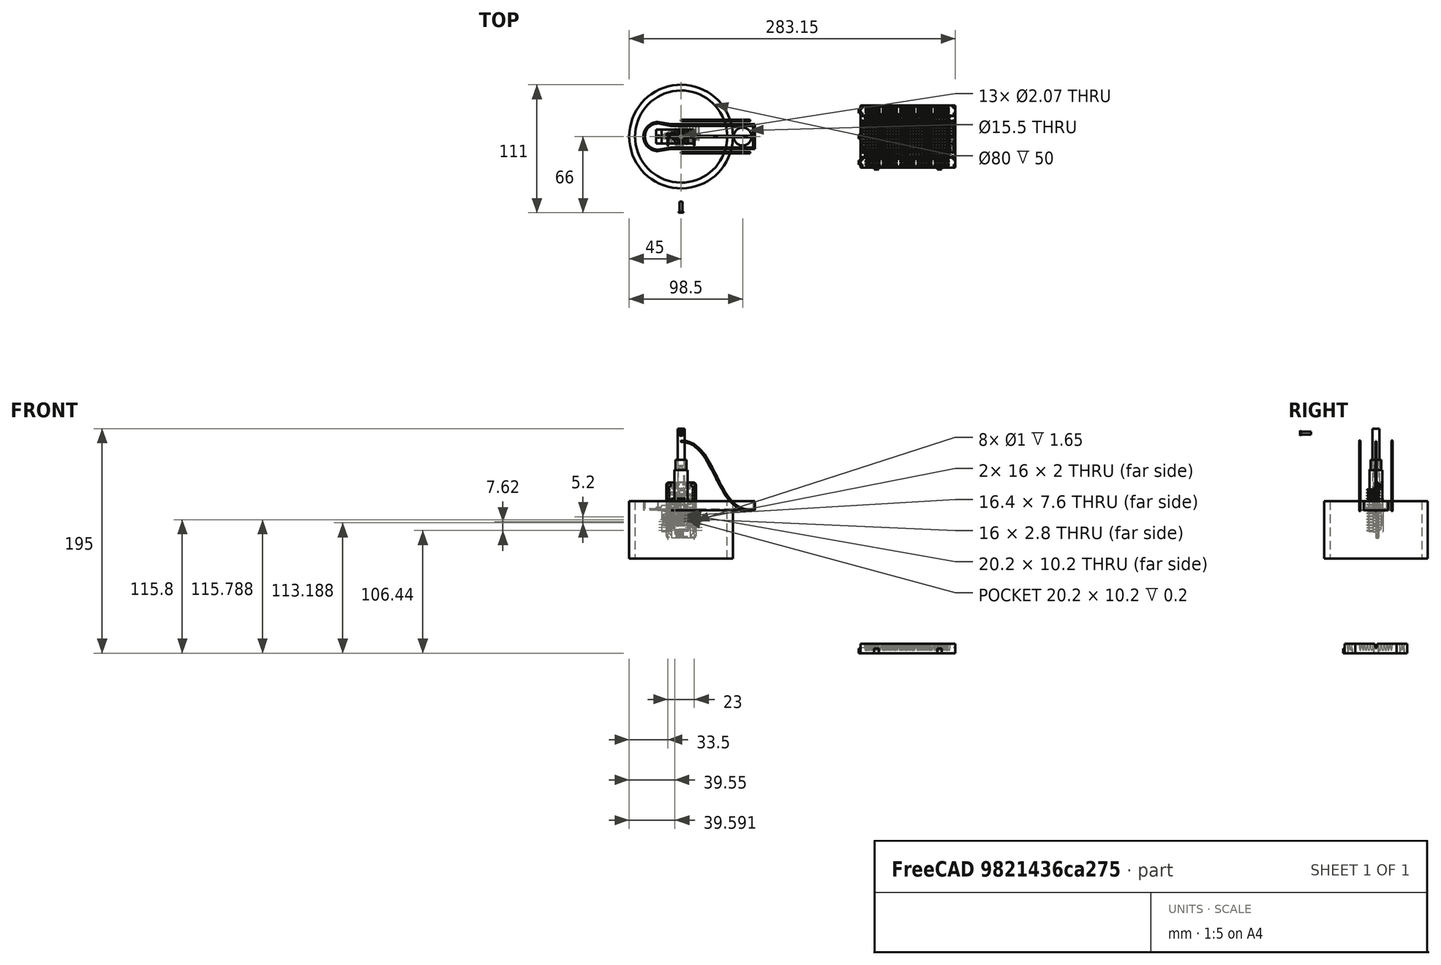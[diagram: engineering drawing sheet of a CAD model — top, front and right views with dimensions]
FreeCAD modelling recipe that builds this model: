
FCSTD DOCUMENT  (FreeCAD 1.0R38641 +678 (Git))
Label: Gems Sorter
License: All rights reserved
LicenseURL: https://en.wikipedia.org/wiki/All_rights_reserved
objects: Part::Feature×123, App::FeaturePython×105, App::Link×104, Sketcher::SketchObject×32, PartDesign::Body×15, PartDesign::Pocket×14, PartDesign::Pad×12, PartDesign::Plane×10, Part::Part2DObjectPython×8, App::Part×5, App::DocumentObjectGroup×5, PartDesign::PolarPattern×3, PartDesign::AdditivePipe×3, Part::FeaturePython×2, App::VarSet×1, PartDesign::Line×1, PartDesign::Thickness×1, PartDesign::Fillet×1, Assembly::JointGroup×1, Assembly::AssemblyObject×1
note: 322 computed .brp shape members not serialized (recipe doc carries the construction recipe); baked Part::Feature solids carry a one-line shape summary decoded from their .brp
EXTERNAL_REF file=Pipe.FCStd obj=Body
EXTERNAL_REF file=Slide Mount.FCStd obj=Cut
EXTERNAL_REF file=Parametric Screw Top Container.FCStd obj=Body001
EXTERNAL_REF file=Parametric Screw Top Container.FCStd obj=Body
EXTERNAL_REF file=testube.FCStd obj=Body
EXTERNAL_REF file=Slide.FCStd obj=Body

FEATURE [App::VarSet] VarSet
  Pipe_thickness = 5
  dowel_dia = 6.2
  fillet_radius = 1.5
  gem_hole_dia = 15.5
  gem_hole_offset = 20
  mdf_thick = 17.5
  mdf_thickness = 7.5
  pipe_OD = 90
  rotation_tolerence = 2.5
  servo_leg_height = 24
  servo_length = 23
  servo_width = 12.3
  shaft_width = 9
  test_tube_dia = 17
  tube_inner_dia = 84.9
FEATURE [Sketcher::SketchObject] Sketch001
  ArcFitTolerance = 1e-06
  AttachmentSupport = -> [XY_Plane001]
  FullyConstrained = true
  MakeInternals = false
  MapMode = 5
  expr: Constraints[2] = VarSet.pipe_OD
  expr: Constraints[3] = VarSet.Pipe_thickness
  sketch-geometry (2):
    g0: Circle CenterX=0 CenterY=0 CenterZ=0 NormalX=0 NormalY=0 NormalZ=1 AngleXU=0 Radius=45
    g1: Circle CenterX=0 CenterY=0 CenterZ=0 NormalX=0 NormalY=0 NormalZ=1 AngleXU=0 Radius=40
  constraints (4):
    c: Coincident(g0,g-1)
    c: Coincident(g1,g0)
    c: Diameter(g0) = 90
    c: Distance(g1,g0) = 5
FEATURE [PartDesign::Pad] Pad001
  Direction = (0,0,1)
  Length = 50
  Length2 = 10
  Profile = -> Sketch001
  ReferenceAxis = -> Sketch001 [N_Axis]
  Refine = true
  Suppressed = false
  Type = 0
FEATURE [PartDesign::Body] Body001  label="Pipe"
  AllowCompound = false
  Group = -> [Sketch001,Pad001]
  Origin = -> Origin001
  Placement = pos=(0,0,-42) rot=(0,0,1;0rad)
  Tip = -> Pad001
FEATURE [Sketcher::SketchObject] Sketch004
  ArcFitTolerance = 1e-06
  AttachmentSupport = -> [XY_Plane002]
  FullyConstrained = true
  MakeInternals = false
  MapMode = 5
  expr: Constraints[0] = VarSet.tube_inner_dia - VarSet.rotation_tolerence
  expr: Constraints[2] = VarSet.gem_hole_offset
  expr: Constraints[3] = VarSet.gem_hole_dia
  sketch-geometry (2):
    g0: Circle CenterX=0 CenterY=0 CenterZ=0 NormalX=0 NormalY=0 NormalZ=1 AngleXU=0 Radius=41.2
    g1: Circle CenterX=0 CenterY=-20 CenterZ=0 NormalX=0 NormalY=0 NormalZ=1 AngleXU=0 Radius=7.75
  constraints (5):
    c: Diameter(g0) = 82.4
    c: PointOnObject(g1,g-2)
    c: Distance(g1,g-1) = 20
    c: Diameter(g1) = 15.5
    c: Coincident(g-1,g0)
FEATURE [PartDesign::Pad] Pad002
  Direction = (0,0,1)
  Length = 7.5
  Length2 = 10
  Profile = -> Sketch004
  ReferenceAxis = -> Sketch004 [N_Axis]
  Refine = true
  Suppressed = false
  Type = 0
  expr: Length = VarSet.mdf_thickness
FEATURE [Sketcher::SketchObject] Sketch006
  ArcFitTolerance = 1e-06
  AttachmentSupport = -> [XY_Plane004]
  FullyConstrained = true
  MakeInternals = false
  MapMode = 5
  expr: Constraints[21] = VarSet.fillet_radius
  expr: Constraints[29] = VarSet.shaft_width
  expr: Constraints[2] = VarSet.gem_hole_dia - 1 mm
  expr: Constraints[3] = VarSet.gem_hole_offset
  expr: Constraints[4] = VarSet.tube_inner_dia - VarSet.rotation_tolerence
  sketch-geometry (13):
    g0: Circle CenterX=0 CenterY=0 CenterZ=0 NormalX=0 NormalY=0 NormalZ=1 AngleXU=0 Radius=41.2
    g1: Circle CenterX=0 CenterY=-20 CenterZ=0 NormalX=0 NormalY=0 NormalZ=1 AngleXU=0 Radius=7.25
    g2: GeomPoint [constr] X=0 Y=0 Z=0
    g3: LineSegment StartX=-7.42462 StartY=-1.06066 StartZ=0 EndX=-1.06066 EndY=-7.42462 EndZ=0
    g4: LineSegment StartX=1.06066 StartY=-7.42462 StartZ=0 EndX=7.42462 EndY=-1.06066 EndZ=0
    g5: LineSegment StartX=7.42462 StartY=1.06066 StartZ=0 EndX=1.06066 EndY=7.42462 EndZ=0
    g6: LineSegment StartX=-1.06066 StartY=7.42462 StartZ=0 EndX=-7.42462 EndY=1.06066 EndZ=0
    g7: ArcOfCircle CenterX=-6.36396 CenterY=0 CenterZ=0 NormalX=0 NormalY=0 NormalZ=1 AngleXU=0 Radius=1.5 StartAngle=2.35619 EndAngle=3.92699
    g8: ArcOfCircle CenterX=0 CenterY=-6.36396 CenterZ=0 NormalX=0 NormalY=0 NormalZ=1 AngleXU=0 Radius=1.5 StartAngle=3.92699 EndAngle=5.49779
    g9: ArcOfCircle CenterX=6.36396 CenterY=1.5e-15 CenterZ=0 NormalX=0 NormalY=0 NormalZ=1 AngleXU=0 Radius=1.5 StartAngle=5.49779 EndAngle=7.06858
    g10: ArcOfCircle CenterX=0 CenterY=6.36396 CenterZ=0 NormalX=0 NormalY=0 NormalZ=1 AngleXU=0 Radius=1.5 StartAngle=0.785398 EndAngle=2.35619
    g11: GeomPoint [constr] X=-8.48528 Y=-5e-16 Z=0
    g12: GeomPoint [constr] X=8.48528 Y=1.3e-15 Z=0
  constraints (30):
    c: Coincident(g0,g-1)
    c: PointOnObject(g1,g-2)
    c: Diameter(g1) = 14.5
    c: Distance(g1,g-1) = 20
    c: Diameter(g0) = 82.4
    c: Coincident(g2,g0)
    c: Tangent(g3,g7) = -1.5708
    c: Tangent(g3,g8) = -1.5708
    c: Tangent(g4,g8) = -1.5708
    c: Tangent(g4,g9) = -1.5708
    c: Tangent(g5,g9) = -1.5708
    c: Tangent(g5,g10) = -1.5708
    c: Tangent(g6,g10) = -1.5708
    c: Tangent(g6,g7) = -1.5708
    c: Equal(g7,g8)
    c: Equal(g8,g9)
    c: Equal(g9,g10)
    c: PointOnObject(g11,g3)
    c: PointOnObject(g11,g6)
    c: PointOnObject(g12,g4)
    c: PointOnObject(g12,g5)
    c: Radius(g8) = 1.5
    c: Equal(g6,g3)
    c: PointOnObject(g10,g-2)
    c: PointOnObject(g8,g-2)
    c: Parallel(g6,g4)
    c: Parallel(g3,g5)
    c: Perpendicular(g5,g6)
    c: PointOnObject(g7,g-1)
    c: Distance(g6,g6) = 9
FEATURE [PartDesign::Pad] Pad004
  Direction = (0,0,1)
  Length = 7.5
  Length2 = 10
  Profile = -> Sketch006
  ReferenceAxis = -> Sketch006 [N_Axis]
  Refine = true
  Suppressed = false
  Type = 0
  expr: Length = VarSet.mdf_thickness
FEATURE [Sketcher::SketchObject] Sketch
  ArcFitTolerance = 1e-06
  AttachmentSupport = -> [XY_Plane]
  FullyConstrained = true
  MakeInternals = false
  MapMode = 5
  expr: Constraints[1] = VarSet.tube_inner_dia
  expr: Constraints[3] = VarSet.dowel_dia + 5 mm
  sketch-geometry (2):
    g0: Circle CenterX=0 CenterY=0 CenterZ=0 NormalX=0 NormalY=0 NormalZ=1 AngleXU=0 Radius=42.45
    g1: Circle CenterX=0 CenterY=0 CenterZ=0 NormalX=0 NormalY=0 NormalZ=1 AngleXU=0 Radius=31.25
  constraints (4):
    c: Coincident(g0,g-1)
    c: Diameter(g0) = 84.9
    c: Coincident(g1,g0)
    c: Distance(g1,g0) = 11.2
FEATURE [PartDesign::Pad] Pad
  Direction = (0,0,1)
  Length = 7.5
  Length2 = 10
  Profile = -> Sketch
  ReferenceAxis = -> Sketch [N_Axis]
  Refine = true
  Suppressed = false
  Type = 0
  expr: Length = VarSet.mdf_thickness
FEATURE [Sketcher::SketchObject] Sketch007
  ArcFitTolerance = 1e-06
  AttachmentSupport = -> [XY_Plane005]
  FullyConstrained = true
  MakeInternals = false
  MapMode = 5
  expr: Constraints[10] = VarSet.gem_hole_offset
  expr: Constraints[5] = VarSet.gem_hole_dia / 2
  expr: Constraints[8] = VarSet.tube_inner_dia / 2
  sketch-geometry (5):
    g0: LineSegment StartX=-33.0518 StartY=-26.638 StartZ=0 EndX=-4 EndY=-26.638 EndZ=0
    g1: LineSegment StartX=33.0518 StartY=-26.638 StartZ=0 EndX=4 EndY=-26.638 EndZ=0
    g2: ArcOfCircle CenterX=1.9e-15 CenterY=-20 CenterZ=0 NormalX=0 NormalY=0 NormalZ=1 AngleXU=0 Radius=7.75 StartAngle=5.25471 EndAngle=10.4532
    g3: ArcOfCircle CenterX=0 CenterY=0 CenterZ=0 NormalX=0 NormalY=0 NormalZ=1 AngleXU=0 Radius=42.45 StartAngle=5.60483 EndAngle=10.1031
    g4: Circle CenterX=0 CenterY=0 CenterZ=0 NormalX=0 NormalY=0 NormalZ=1 AngleXU=0 Radius=9
  constraints (14):
    c: Horizontal(g0)
    c: Horizontal(g1)
    c: Symmetric(g0,g1,g-2)
    c: Coincident(g2,g0)
    c: Coincident(g2,g1)
    c: Radius(g2) = 7.75
    c: Coincident(g3,g-1)
    c: Coincident(g3,g1)
    c: Radius(g3) = 42.45
    c: Coincident(g0,g3)
    c: Distance(g2,g-1) = 20
    c: DistanceX(g0,g1) = 8
    c: Coincident(g4,g3)
    c: Diameter(g4) = 18
FEATURE [PartDesign::Pad] Pad005
  Direction = (0,0,1)
  Length = 17.5
  Length2 = 10
  Profile = -> Sketch007
  ReferenceAxis = -> Sketch007 [N_Axis]
  Refine = true
  Suppressed = false
  Type = 0
  expr: Length = VarSet.mdf_thick
FEATURE [Sketcher::SketchObject] Sketch008
  ArcFitTolerance = 1e-06
  AttachmentSupport = -> [XY_Plane006]
  FullyConstrained = false
  MakeInternals = false
  MapMode = 5
  expr: Constraints[15] = VarSet.gem_hole_offset
  expr: Constraints[16] = VarSet.gem_hole_offset + VarSet.pipe_OD / 2 + VarSet.test_tube_dia + 5 mm
  expr: Constraints[3] = VarSet.tube_inner_dia / 2
  sketch-geometry (6):
    g0: ArcOfCircle CenterX=0 CenterY=0 CenterZ=0 NormalX=0 NormalY=0 NormalZ=1 AngleXU=0 Radius=42.45 StartAngle=1.5708 EndAngle=4.71239
    g1: LineSegment [constr] StartX=2.6e-15 StartY=42.45 StartZ=0 EndX=0 EndY=85.6971 EndZ=0
    g2: LineSegment [constr] StartX=0 StartY=-42.45 StartZ=0 EndX=0 EndY=-85.6971 EndZ=0
    g3: LineSegment StartX=2.6e-15 StartY=42.45 StartZ=0 EndX=27.4414 EndY=72.9268 EndZ=0
    g4: LineSegment StartX=0 StartY=-42.45 StartZ=0 EndX=27.4414 EndY=-72.9268 EndZ=0
    g5: ArcOfCircle CenterX=-20 CenterY=0 CenterZ=0 NormalX=0 NormalY=0 NormalZ=1 AngleXU=0 Radius=87 StartAngle=5.28914 EndAngle=7.27723
  constraints (17):
    c: Coincident(g0,g-1)
    c: PointOnObject(g0,g-2)
    c: PointOnObject(g0,g-2)
    c: Radius(g0) = 42.45
    c: PointOnObject(g1,g-2)
    c: PointOnObject(g2,g-2)
    c: Coincident(g1,g0)
    c: Coincident(g2,g0)
    c: Coincident(g3,g0)
    c: Angle(g3,g1) = 0.733038
    c: Coincident(g4,g0)
    c: Angle(g2,g4) = 0.733038
    c: PointOnObject(g5,g-1)
    c: Coincident(g5,g3)
    c: Coincident(g5,g4)
    c: Distance(g5,g-2) = 20
    c: Radius(g5) = 87
FEATURE [PartDesign::Pad] Pad006
  Direction = (0,0,1)
  Length = 7.5
  Length2 = 10
  Profile = -> Sketch008
  ReferenceAxis = -> Sketch008 [N_Axis]
  Refine = true
  Suppressed = false
  Type = 0
  expr: Length = VarSet.mdf_thickness
FEATURE [PartDesign::Plane] DatumPlane
  AttachmentOffset = pos=(0,0,7.5) rot=(0,0,1;0rad)
  AttachmentSupport = -> [XY_Plane006]
  Length = 134.506
  MapMode = 5
  Placement = pos=(0,0,7.5) rot=(0,0,1;0rad)
  ResizeMode = 0
  Width = 171.101
  expr: .AttachmentOffset.Base.z = VarSet.mdf_thickness
FEATURE [Sketcher::SketchObject] Sketch009
  ArcFitTolerance = 1e-06
  AttachmentSupport = -> [DatumPlane]
  FullyConstrained = true
  MakeInternals = false
  MapMode = 5
  Placement = pos=(0,0,7.5) rot=(0,0,1;0rad)
  expr: Constraints[1] = VarSet.test_tube_dia
  expr: Constraints[2] = VarSet.pipe_OD / 2 + VarSet.test_tube_dia / 2
  sketch-geometry (1):
    g0: Circle CenterX=53.5 CenterY=0 CenterZ=0 NormalX=0 NormalY=0 NormalZ=1 AngleXU=0 Radius=8.5
  constraints (3):
    c: PointOnObject(g0,g-1)
    c: Diameter(g0) = 17
    c: Distance(g0,g-2) = 53.5
FEATURE [PartDesign::Pocket] Pocket
  BaseFeature = -> Pad006
  Direction = (0,0,-1)
  Length = 5
  Length2 = 5
  Profile = -> Sketch009
  ReferenceAxis = -> Sketch009 [N_Axis]
  Refine = true
  Suppressed = false
  Type = 1
FEATURE [PartDesign::Line] DatumLine
  AttacherType = Attacher::AttachEngineLine
  AttachmentOffset = pos=(-20,0,0) rot=(0,0,1;0rad)
  AttachmentSupport = -> [Z_Axis006]
  Length = 20
  MapMode = 29
  Placement = pos=(-20,0,0) rot=(0,0,1;0rad)
  ResizeMode = 0
  expr: .AttachmentOffset.Base.x = -VarSet.gem_hole_offset
FEATURE [PartDesign::PolarPattern] PolarPattern
  Angle = 360
  Axis = -> DatumLine
  BaseFeature = -> Pocket
  Mode = 0
  Occurrences = 22
  Offset = 120
  Originals = -> [Pocket]
  Refine = true
  Suppressed = false
  TransformMode = 0
FEATURE [Sketcher::SketchObject] Sketch010
  ArcFitTolerance = 1e-06
  AttachmentSupport = -> [DatumPlane]
  FullyConstrained = false
  MakeInternals = false
  MapMode = 5
  Placement = pos=(0,0,7.5) rot=(0,0,1;0rad)
  expr: Constraints[1] = VarSet.gem_hole_offset
  expr: Constraints[21] = VarSet.servo_length
  sketch-geometry (9):
    g0: LineSegment [constr] StartX=-20 StartY=14.1317 StartZ=0 EndX=-20 EndY=-18.2085 EndZ=0
    g1: LineSegment StartX=-34 StartY=4.05 StartZ=0 EndX=-34 EndY=-4.05 EndZ=0
    g2: LineSegment StartX=-34 StartY=-4.05 StartZ=0 EndX=-25.9 EndY=-4.05 EndZ=0
    g3: LineSegment StartX=-25.9 StartY=-4.05 StartZ=0 EndX=-25.9 EndY=4.05 EndZ=0
    g4: LineSegment StartX=-25.9 StartY=4.05 StartZ=0 EndX=-34 EndY=4.05 EndZ=0
    g5: LineSegment StartX=-2.9 StartY=4.05 StartZ=0 EndX=-2.9 EndY=-4.05 EndZ=0
    g6: LineSegment StartX=-2.9 StartY=-4.05 StartZ=0 EndX=5.2 EndY=-4.05 EndZ=0
    g7: LineSegment StartX=5.2 StartY=-4.05 StartZ=0 EndX=5.2 EndY=4.05 EndZ=0
    g8: LineSegment StartX=5.2 StartY=4.05 StartZ=0 EndX=-2.9 EndY=4.05 EndZ=0
  constraints (24):
    c: Vertical(g0)
    c: Distance(g-2,g0) = 20
    c: Coincident(g1,g2)
    c: Coincident(g2,g3)
    c: Coincident(g3,g4)
    c: Coincident(g4,g1)
    c: Vertical(g3)
    c: Horizontal(g2)
    c: Horizontal(g4)
    c: Coincident(g5,g6)
    c: Coincident(g6,g7)
    c: Coincident(g7,g8)
    c: Coincident(g8,g5)
    c: Vertical(g7)
    c: Horizontal(g6)
    c: Horizontal(g8)
    c: Equal(g4,g1)
    c: Equal(g1,g8)
    c: Equal(g8,g5)
    c: Symmetric(g1,g1,g-1)
    c: Symmetric(g5,g5,g-1)
    c: Distance(g5,g3) = 23
    c: Distance(g0,g3) = 5.9
    c: DistanceX(g4,g4) = 8.1
FEATURE [PartDesign::Pocket] Pocket001
  BaseFeature = -> PolarPattern
  Direction = (0,0,-1)
  Length = 5
  Length2 = 5
  Profile = -> Sketch010
  ReferenceAxis = -> Sketch010 [N_Axis]
  Refine = true
  Suppressed = false
  Type = 1
FEATURE [PartDesign::Plane] DatumPlane001
  AttachmentOffset = pos=(0,0,7.5) rot=(0,0,1;0rad)
  AttachmentSupport = -> [XY_Plane]
  Length = 101.88
  MapMode = 5
  Placement = pos=(0,0,7.5) rot=(0,0,1;0rad)
  ResizeMode = 0
  Width = 101.88
  expr: .AttachmentOffset.Base.z = VarSet.mdf_thickness
FEATURE [Sketcher::SketchObject] Sketch011
  ArcFitTolerance = 1e-06
  AttachmentSupport = -> [DatumPlane001]
  FullyConstrained = true
  MakeInternals = false
  MapMode = 5
  Placement = pos=(0,0,7.5) rot=(0,0,1;0rad)
  expr: Constraints[17] = VarSet.tube_inner_dia / 2 - 2.5 mm - VarSet.dowel_dia / 2
  expr: Constraints[1] = VarSet.dowel_dia
  expr: Constraints[2] = VarSet.tube_inner_dia / 2 - 2.5 mm - VarSet.dowel_dia / 2
  expr: Constraints[6] = VarSet.tube_inner_dia / 2 - 2.5 mm - VarSet.dowel_dia / 2
  sketch-geometry (8):
    g0: Circle [constr] CenterX=-36.85 CenterY=0 CenterZ=0 NormalX=0 NormalY=0 NormalZ=1 AngleXU=0 Radius=3.1
    g1: Circle CenterX=-31.913 CenterY=18.425 CenterZ=0 NormalX=0 NormalY=0 NormalZ=1 AngleXU=0 Radius=3.1
    g2: Circle CenterX=-31.913 CenterY=-18.425 CenterZ=0 NormalX=0 NormalY=0 NormalZ=1 AngleXU=0 Radius=3.1
    g3: LineSegment [constr] StartX=-31.913 StartY=-18.425 StartZ=0 EndX=0 EndY=0 EndZ=0
    g4: Circle CenterX=-18.425 CenterY=31.913 CenterZ=0 NormalX=0 NormalY=0 NormalZ=1 AngleXU=0 Radius=3.1
    g5: Circle CenterX=-18.425 CenterY=-31.913 CenterZ=0 NormalX=0 NormalY=0 NormalZ=1 AngleXU=0 Radius=3.1
    g6: LineSegment [constr] StartX=-18.425 StartY=31.913 StartZ=0 EndX=0 EndY=-3.6e-15 EndZ=0
    g7: LineSegment [constr] StartX=0 StartY=0 StartZ=0 EndX=-18.425 EndY=-31.913 EndZ=0
  constraints (19):
    c: PointOnObject(g0,g-1)
    c: Diameter(g0) = 6.2
    c: Distance(g0,g-2) = 36.85
    c: Equal(g1,g2)
    c: Equal(g2,g0)
    c: Symmetric(g2,g1,g-1)
    c: Distance(g1,g-1) = 36.85
    c: Coincident(g3,g2)
    c: Coincident(g3,g-1)
    c: Angle(g-1,g3) = 0.523599
    c: Equal(g5,g4)
    c: Equal(g4,g2)
    c: Symmetric(g5,g4,g-1)
    c: Coincident(g6,g4)
    c: Coincident(g6,g3)
    c: Coincident(g7,g3)
    c: Coincident(g7,g5)
    c: Distance(g6,g6) = 36.85
    c: Angle(g6,g-1) = 1.0472
FEATURE [PartDesign::Pocket] Pocket003
  BaseFeature = -> Pad
  Direction = (0,0,-1)
  Length = 5
  Length2 = 5
  Profile = -> Sketch011
  ReferenceAxis = -> Sketch011 [N_Axis]
  Refine = true
  Suppressed = false
  Type = 1
FEATURE [Sketcher::SketchObject] Sketch012
  ArcFitTolerance = 1e-06
  AttachmentSupport = -> [XY_Plane007]
  FullyConstrained = true
  MakeInternals = false
  MapMode = 5
  expr: Constraints[19] = VarSet.mdf_thickness
  expr: Constraints[20] = VarSet.mdf_thickness
  expr: Constraints[21] = VarSet.servo_leg_height
  expr: Constraints[41] = VarSet.fillet_radius
  expr: Constraints[47] = VarSet.mdf_thickness / 2
  sketch-geometry (20):
    g0: LineSegment StartX=0 StartY=0 StartZ=0 EndX=0 EndY=7.5 EndZ=0
    g1: LineSegment StartX=0 StartY=7.5 StartZ=0 EndX=7.5 EndY=7.5 EndZ=0
    g2: LineSegment StartX=7.5 StartY=7.5 StartZ=0 EndX=7.5 EndY=12.0784 EndZ=0
    g3: LineSegment StartX=7.5 StartY=12.0784 StartZ=0 EndX=31.5 EndY=12.0784 EndZ=0
    g4: LineSegment StartX=31.5 StartY=12.0784 StartZ=0 EndX=31.5 EndY=-4.57843 EndZ=0
    g5: LineSegment StartX=31.5 StartY=-4.57843 StartZ=0 EndX=7.5 EndY=-4.57843 EndZ=0
    g6: LineSegment StartX=7.5 StartY=-4.57843 StartZ=0 EndX=7.5 EndY=0 EndZ=0
    g7: LineSegment StartX=7.5 StartY=0 StartZ=0 EndX=0 EndY=0 EndZ=0
    g8: LineSegment StartX=12.5 StartY=6.57843 StartZ=0 EndX=12.5 EndY=0.921573 EndZ=0
    g9: LineSegment StartX=14 StartY=-0.578427 StartZ=0 EndX=19.6569 EndY=-0.578427 EndZ=0
    g10: LineSegment StartX=21.1569 StartY=0.921573 StartZ=0 EndX=21.1569 EndY=6.57843 EndZ=0
    g11: LineSegment StartX=19.6569 StartY=8.07843 StartZ=0 EndX=14 EndY=8.07843 EndZ=0
    g12: ArcOfCircle CenterX=14 CenterY=6.57843 CenterZ=0 NormalX=0 NormalY=0 NormalZ=1 AngleXU=0 Radius=1.5 StartAngle=1.5708 EndAngle=3.14159
    g13: ArcOfCircle CenterX=14 CenterY=0.921573 CenterZ=0 NormalX=0 NormalY=0 NormalZ=1 AngleXU=0 Radius=1.5 StartAngle=3.14159 EndAngle=4.71239
    g14: ArcOfCircle CenterX=19.6569 CenterY=0.921573 CenterZ=0 NormalX=0 NormalY=0 NormalZ=1 AngleXU=0 Radius=1.5 StartAngle=4.71239 EndAngle=6.28319
    g15: ArcOfCircle CenterX=19.6569 CenterY=6.57843 CenterZ=0 NormalX=0 NormalY=0 NormalZ=1 AngleXU=0 Radius=1.5 StartAngle=0 EndAngle=1.5708
    g16: GeomPoint [constr] X=12.5 Y=8.07843 Z=0
    g17: GeomPoint [constr] X=21.1569 Y=-0.578427 Z=0
    g18: LineSegment [constr] StartX=14 StartY=6.57843 StartZ=0 EndX=19.6569 EndY=0.921573 EndZ=0
    g19: LineSegment [constr] StartX=14 StartY=0.921573 StartZ=0 EndX=16.8284 EndY=3.75 EndZ=0
  constraints (51):
    c: Coincident(g0,g-1)
    c: PointOnObject(g0,g-2)
    c: Coincident(g0,g1)
    c: Horizontal(g1)
    c: Coincident(g1,g2)
    c: Vertical(g2)
    c: Coincident(g2,g3)
    c: Coincident(g3,g4)
    c: Vertical(g4)
    c: Coincident(g4,g5)
    c: Horizontal(g5)
    c: Coincident(g5,g6)
    c: PointOnObject(g6,g-1)
    c: Vertical(g6)
    c: Coincident(g6,g7)
    c: Coincident(g7,g0)
    c: Equal(g1,g7)
    c: Equal(g3,g5)
    c: Equal(g2,g6)
    c: DistanceX(g1,g1) = 7.5
    c: Distance(g0,g0) = 7.5
    c: DistanceX(g5,g5) = 24
    c: Tangent(g8,g12) = -1.5708
    c: Tangent(g8,g13) = -1.5708
    c: Tangent(g9,g13) = -1.5708
    c: Tangent(g9,g14) = -1.5708
    c: Tangent(g10,g14) = -1.5708
    c: Tangent(g10,g15) = -1.5708
    c: Tangent(g11,g15) = -1.5708
    c: Tangent(g11,g12) = -1.5708
    c: Vertical(g8)
    c: Vertical(g10)
    c: Horizontal(g9)
    c: Horizontal(g11)
    c: Equal(g12,g13)
    c: Equal(g13,g14)
    c: Equal(g14,g15)
    c: PointOnObject(g16,g8)
    c: PointOnObject(g16,g11)
    c: PointOnObject(g17,g9)
    c: PointOnObject(g17,g10)
    c: Radius(g13) = 1.5
    c: Coincident(g18,g12)
    c: Coincident(g18,g14)
    c: Coincident(g19,g13)
    c: Symmetric(g18,g18,g19)
    c: Equal(g11,g8)
    c: Distance(g19,g-1) = 3.75
    c: Distance(g18,g18) = 8
    c: Distance(g2,g8) = 5
    c: Distance(g5,g9) = 4
FEATURE [PartDesign::Pad] Pad007
  Direction = (0,0,1)
  Length = 7.5
  Length2 = 10
  Profile = -> Sketch012
  ReferenceAxis = -> Sketch012 [N_Axis]
  Refine = true
  Suppressed = false
  Type = 0
  expr: Length = VarSet.mdf_thickness
FEATURE [Sketcher::SketchObject] Sketch013
  ArcFitTolerance = 1e-06
  AttachmentSupport = -> [DatumPlane]
  FullyConstrained = true
  MakeInternals = false
  MapMode = 5
  Placement = pos=(0,0,7.5) rot=(0,0,1;0rad)
  expr: Constraints[5] = VarSet.tube_inner_dia / 2 - 2.5 mm - VarSet.dowel_dia / 2
  expr: Constraints[6] = VarSet.tube_inner_dia / 2 - 2.5 mm - VarSet.dowel_dia / 2
  expr: Constraints[7] = VarSet.dowel_dia
  sketch-geometry (6):
    g0: Circle CenterX=-31.913 CenterY=18.425 CenterZ=0 NormalX=0 NormalY=0 NormalZ=1 AngleXU=0 Radius=3.1
    g1: Circle CenterX=-18.425 CenterY=31.913 CenterZ=0 NormalX=0 NormalY=0 NormalZ=1 AngleXU=0 Radius=3.1
    g2: Circle CenterX=-31.913 CenterY=-18.425 CenterZ=0 NormalX=0 NormalY=0 NormalZ=1 AngleXU=0 Radius=3.1
    g3: Circle CenterX=-18.425 CenterY=-31.913 CenterZ=0 NormalX=0 NormalY=0 NormalZ=1 AngleXU=0 Radius=3.1
    g4: LineSegment [constr] StartX=-31.913 StartY=18.425 StartZ=0 EndX=0 EndY=0 EndZ=0
    g5: LineSegment [constr] StartX=-18.425 StartY=31.913 StartZ=0 EndX=0 EndY=0 EndZ=0
  constraints (14):
    c: Equal(g3,g2)
    c: Equal(g2,g0)
    c: Equal(g0,g1)
    c: Symmetric(g0,g2,g-1)
    c: Symmetric(g1,g3,g-1)
    c: Distance(g2,g-1) = 36.85
    c: Distance(g3,g-1) = 36.85
    c: Diameter(g3) = 6.2
    c: Coincident(g4,g0)
    c: Coincident(g4,g-1)
    c: Coincident(g5,g1)
    c: Coincident(g5,g4)
    c: Angle(g4,g-1) = 0.523599
    c: Angle(g5,g-1) = 1.0472
FEATURE [PartDesign::Pocket] Pocket004
  BaseFeature = -> Pocket001
  Direction = (0,0,-1)
  Length = 5
  Length2 = 5
  Profile = -> Sketch013
  ReferenceAxis = -> Sketch013 [N_Axis]
  Refine = true
  Suppressed = false
  Type = 1
FEATURE [PartDesign::Body] Body006  label="testube_layer"
  AllowCompound = false
  Group = -> [Sketch008,Pad006,DatumPlane,Sketch009,Pocket,DatumLine,PolarPattern,Sketch010,Pocket001,Sketch013,Pocket004]
  Origin = -> Origin006
  Placement = pos=(0,0,-39) rot=(0,0,1;0rad)
  Tip = -> Pocket004
FEATURE [Sketcher::SketchObject] Sketch014
  ArcFitTolerance = 1e-06
  AttachmentSupport = -> [XY_Plane008]
  FullyConstrained = true
  MakeInternals = false
  MapMode = 5
  expr: Constraints[1] = VarSet.dowel_dia - 0.05 mm
  sketch-geometry (1):
    g0: Circle CenterX=0 CenterY=0 CenterZ=0 NormalX=0 NormalY=0 NormalZ=1 AngleXU=0 Radius=3.075
  constraints (2):
    c: Coincident(g0,g-1)
    c: Diameter(g0) = 6.15
FEATURE [PartDesign::Pad] Pad008
  Direction = (0,0,1)
  Length = 71
  Length2 = 10
  Profile = -> Sketch014
  ReferenceAxis = -> Sketch014 [N_Axis]
  Refine = true
  Suppressed = false
  Type = 0
FEATURE [PartDesign::Body] Body008  label="dowel"
  AllowCompound = false
  Group = -> [Sketch014,Pad008]
  Origin = -> Origin008
  Tip = -> Pad008
FEATURE [Sketcher::SketchObject] Sketch015
  ArcFitTolerance = 1e-06
  AttachmentSupport = -> [Pad007]
  ExternalGeometry = -> [Pad007]
  FullyConstrained = false
  MakeInternals = false
  MapMode = 5
  Placement = pos=(31.5,0,0) rot=(0.57735,0.57735,0.57735;2.0944rad)
  sketch-geometry (1):
    g0: Circle CenterX=3.87266 CenterY=2.4 CenterZ=0 NormalX=0 NormalY=0 NormalZ=1 AngleXU=0 Radius=0.75
  constraints (2):
    c: Distance(g0,g-3) = 2.4
    c: Diameter(g0) = 1.5
FEATURE [PartDesign::Pocket] Pocket005
  BaseFeature = -> Pad007
  Direction = (-1,0,0)
  Length = 5
  Length2 = 5
  Profile = -> Sketch015
  ReferenceAxis = -> Sketch015 [N_Axis]
  Refine = true
  Suppressed = false
  Type = 0
FEATURE [PartDesign::Body] Body007  label="sevo_legs"
  AllowCompound = false
  Group = -> [Sketch012,Pad007,Sketch015,Pocket005]
  Origin = -> Origin007
  Placement = pos=(-26,-3,23) rot=(0,1,0;4.71239rad)
  Tip = -> Pocket005
FEATURE [Sketcher::SketchObject] Sketch016
  ArcFitTolerance = 1e-06
  AttachmentSupport = -> [XY_Plane009]
  FullyConstrained = true
  MakeInternals = false
  MapMode = 5
  expr: Constraints[16] = VarSet.gem_hole_dia / 2 + 5 mm
  expr: Constraints[2] = VarSet.gem_hole_dia + 6 mm
  expr: Constraints[5] = VarSet.pipe_OD / 2 + VarSet.test_tube_dia + 2 mm
  expr: Constraints[8] = VarSet.gem_hole_offset
  sketch-geometry (8):
    g0: LineSegment StartX=-8.65743 StartY=10.75 StartZ=0 EndX=64 EndY=10.75 EndZ=0
    g1: LineSegment StartX=64 StartY=10.75 StartZ=0 EndX=64 EndY=-10.75 EndZ=0
    g2: LineSegment StartX=64 StartY=-10.75 StartZ=0 EndX=-8.65743 EndY=-10.75 EndZ=0
    g3: ArcOfCircle CenterX=-20 CenterY=0 CenterZ=0 NormalX=0 NormalY=0 NormalZ=1 AngleXU=0 Radius=12.75 StartAngle=1.5708 EndAngle=4.71239
    g4: LineSegment [constr] StartX=-20 StartY=-12.75 StartZ=0 EndX=-20 EndY=12.75 EndZ=0
    g5: LineSegment StartX=-20 StartY=12.75 StartZ=0 EndX=-8.65743 EndY=10.75 EndZ=0
    g6: LineSegment StartX=-20 StartY=-12.75 StartZ=0 EndX=-8.65743 EndY=-10.75 EndZ=0
    g7: LineSegment [constr] StartX=-8.65743 StartY=10.75 StartZ=0 EndX=-20 EndY=10.75 EndZ=0
  constraints (22):
    c: Coincident(g2,g1)
    c: Coincident(g0,g1)
    c: DistanceY(g1,g1) = 21.5
    c: Symmetric(g0,g1,g-1)
    c: Symmetric(g0,g2,g-1)
    c: Distance(g-2,g1) = 64
    c: Angle(g3) = 3.14159
    c: PointOnObject(g3,g-1)
    c: Distance(g3,g-2) = 20
    c: Coincident(g4,g3)
    c: Coincident(g4,g3)
    c: Vertical(g4)
    c: Coincident(g5,g3)
    c: Coincident(g5,g0)
    c: Coincident(g6,g3)
    c: Coincident(g6,g2)
    c: Radius(g3) = 12.75
    c: Coincident(g7,g0)
    c: PointOnObject(g7,g4)
    c: Horizontal(g7)
    c: Angle(g5,g7) = 0.174533
    c: Horizontal(g0)
FEATURE [PartDesign::Pad] Pad009
  Direction = (0,0,1)
  Length = 8
  Length2 = 10
  Profile = -> Sketch016
  ReferenceAxis = -> Sketch016 [N_Axis]
  Refine = true
  Suppressed = false
  Type = 0
FEATURE [PartDesign::Thickness] Thickness
  Base = -> Pad009 [Face8]
  BaseFeature = -> Pad009
  Intersection = false
  Join = 0
  Mode = 0
  Refine = true
  Reversed = true
  SupportTransform = false
  Suppressed = false
  Value = 1.4
FEATURE [Sketcher::SketchObject] Sketch017
  ArcFitTolerance = 1e-06
  AttachmentSupport = -> [Thickness]
  FullyConstrained = true
  MakeInternals = false
  MapMode = 5
  Placement = pos=(0,0,1.4) rot=(0,0,1;0rad)
  expr: Constraints[1] = VarSet.gem_hole_dia
  expr: Constraints[2] = VarSet.pipe_OD / 2 + VarSet.test_tube_dia / 2
  sketch-geometry (1):
    g0: Circle CenterX=53.5 CenterY=0 CenterZ=0 NormalX=0 NormalY=0 NormalZ=1 AngleXU=0 Radius=7.75
  constraints (3):
    c: PointOnObject(g0,g-1)
    c: Diameter(g0) = 15.5
    c: Distance(g0,g-2) = 53.5
FEATURE [PartDesign::Pocket] Pocket006
  BaseFeature = -> Thickness
  Direction = (0,0,-1)
  Length = 5
  Length2 = 5
  Profile = -> Sketch017
  ReferenceAxis = -> Sketch017 [N_Axis]
  Refine = true
  Suppressed = false
  Type = 1
FEATURE [PartDesign::Body] Body009  label="slide"
  AllowCompound = false
  Group = -> [Sketch016,Pad009,Thickness,Sketch017,Pocket006]
  Origin = -> Origin009
  Tip = -> Pocket006
FEATURE [PartDesign::Fillet] Fillet
  Base = -> Pad005 [Edge5,Edge8,Edge2,Edge1]
  BaseFeature = -> Pad005
  Radius = 1.5
  Refine = true
  SupportTransform = false
  Suppressed = false
  UseAllEdges = false
  expr: Radius = VarSet.fillet_radius
FEATURE [Part::Feature] Part__Feature002  label="shaft"
  shape: bbox 11.25 x 11.25 x 44 mm, 27 faces (baked)
FEATURE [Sketcher::SketchObject] Sketch018
  ArcFitTolerance = 1e-06
  AttachmentSupport = -> [Pad002]
  ExternalGeometry = -> [Pad002]
  FullyConstrained = true
  MakeInternals = false
  MapMode = 5
  Placement = pos=(0,0,7.5) rot=(0,0,1;0rad)
  sketch-geometry (4):
    g0: LineSegment StartX=-1.5 StartY=-33.1727 StartZ=0 EndX=-1.5 EndY=-41.1727 EndZ=0
    g1: LineSegment StartX=1.5 StartY=-41.1727 StartZ=0 EndX=1.5 EndY=-33.1727 EndZ=0
    g2: LineSegment StartX=1.5 StartY=-33.1727 StartZ=0 EndX=-1.5 EndY=-33.1727 EndZ=0
    g3: ArcOfCircle CenterX=0 CenterY=0 CenterZ=0 NormalX=0 NormalY=0 NormalZ=1 AngleXU=0 Radius=41.2 StartAngle=4.67597 EndAngle=4.7488
  constraints (11):
    c: Coincident(g1,g2)
    c: Coincident(g2,g0)
    c: Vertical(g0)
    c: Vertical(g1)
    c: Coincident(g3,g-1)
    c: Coincident(g3,g0)
    c: Coincident(g3,g1)
    c: PointOnObject(g0,g-3)
    c: Symmetric(g0,g1,g-2)
    c: Distance(g2,g2) = 3
    c: DistanceY(g1,g1) = 8
FEATURE [PartDesign::Pocket] Pocket007
  BaseFeature = -> Pad002
  Direction = (0,0,-1)
  Length = 2
  Length2 = 5
  Profile = -> Sketch018
  ReferenceAxis = -> Sketch018 [N_Axis]
  Refine = true
  Suppressed = false
  Type = 0
FEATURE [Sketcher::SketchObject] Sketch019
  ArcFitTolerance = 1e-06
  AttachmentSupport = -> [Pocket007]
  FullyConstrained = true
  MakeInternals = false
  MapMode = 5
  Placement = pos=(0,0,7.5) rot=(0,0,1;0rad)
  sketch-geometry (12):
    g0: LineSegment StartX=-6 StartY=4.5 StartZ=0 EndX=-6 EndY=-4.5 EndZ=0
    g1: LineSegment StartX=-4.5 StartY=-6 StartZ=0 EndX=4.5 EndY=-6 EndZ=0
    g2: LineSegment StartX=6 StartY=-4.5 StartZ=0 EndX=6 EndY=4.5 EndZ=0
    g3: LineSegment StartX=4.5 StartY=6 StartZ=0 EndX=-4.5 EndY=6 EndZ=0
    g4: ArcOfCircle CenterX=-4.5 CenterY=4.5 CenterZ=0 NormalX=0 NormalY=0 NormalZ=1 AngleXU=0 Radius=1.5 StartAngle=1.5708 EndAngle=3.14159
    g5: ArcOfCircle CenterX=-4.5 CenterY=-4.5 CenterZ=0 NormalX=0 NormalY=0 NormalZ=1 AngleXU=0 Radius=1.5 StartAngle=3.14159 EndAngle=4.71239
    g6: ArcOfCircle CenterX=4.5 CenterY=-4.5 CenterZ=0 NormalX=0 NormalY=0 NormalZ=1 AngleXU=0 Radius=1.5 StartAngle=4.71239 EndAngle=6.28319
    g7: ArcOfCircle CenterX=4.5 CenterY=4.5 CenterZ=0 NormalX=0 NormalY=0 NormalZ=1 AngleXU=0 Radius=1.5 StartAngle=0 EndAngle=1.5708
    g8: GeomPoint [constr] X=-6 Y=6 Z=0
    g9: GeomPoint [constr] X=6 Y=-6 Z=0
    g10: LineSegment [constr] StartX=-4.5 StartY=4.5 StartZ=0 EndX=4.5 EndY=-4.5 EndZ=0
    g11: LineSegment [constr] StartX=4.5 StartY=4.5 StartZ=0 EndX=0 EndY=0 EndZ=0
  constraints (27):
    c: Tangent(g0,g4) = -1.5708
    c: Tangent(g0,g5) = -1.5708
    c: Tangent(g1,g5) = -1.5708
    c: Tangent(g1,g6) = -1.5708
    c: Tangent(g2,g6) = -1.5708
    c: Tangent(g2,g7) = -1.5708
    c: Tangent(g3,g7) = -1.5708
    c: Tangent(g3,g4) = -1.5708
    c: Vertical(g0)
    c: Vertical(g2)
    c: Horizontal(g1)
    c: Horizontal(g3)
    c: Equal(g4,g5)
    c: Equal(g5,g6)
    c: Equal(g6,g7)
    c: PointOnObject(g8,g0)
    c: PointOnObject(g8,g3)
    c: PointOnObject(g9,g1)
    c: PointOnObject(g9,g2)
    c: Radius(g4) = 1.5
    c: Distance(g3,g3) = 9
    c: Equal(g3,g2)
    c: Coincident(g10,g4)
    c: Coincident(g10,g6)
    c: Coincident(g11,g7)
    c: Symmetric(g10,g10,g11)
    c: Coincident(g11,g-1)
FEATURE [PartDesign::Pocket] Pocket008
  BaseFeature = -> Pocket007
  Direction = (0,0,-1)
  Length = 4
  Length2 = 5
  Profile = -> Sketch019
  ReferenceAxis = -> Sketch019 [N_Axis]
  Refine = true
  Suppressed = false
  Type = 0
FEATURE [PartDesign::Body] Body002  label="second_layer"
  AllowCompound = false
  Group = -> [Sketch004,Pad002,Sketch018,Pocket007,Sketch019,Pocket008]
  Origin = -> Origin002
  Placement = pos=(0,0,-3) rot=(0,0,1;1.5708rad)
  Tip = -> Pocket008
FEATURE [Sketcher::SketchObject] Sketch020
  ArcFitTolerance = 1e-06
  AttachmentSupport = -> [Pad004]
  ExternalGeometry = -> [Pad004]
  FullyConstrained = true
  MakeInternals = false
  MapMode = 5
  Placement = pos=(0,0,7.5) rot=(0,0,1;0rad)
  sketch-geometry (4):
    g0: LineSegment StartX=22.396 StartY=-24.5173 StartZ=0 EndX=28.0528 EndY=-30.1741 EndZ=0
    g1: LineSegment StartX=24.5173 StartY=-22.396 StartZ=0 EndX=30.1741 EndY=-28.0528 EndZ=0
    g2: LineSegment StartX=24.5173 StartY=-22.396 StartZ=0 EndX=22.396 EndY=-24.5173 EndZ=0
    g3: ArcOfCircle CenterX=0 CenterY=0 CenterZ=0 NormalX=0 NormalY=0 NormalZ=1 AngleXU=0 Radius=41.2 StartAngle=5.46137 EndAngle=5.5342
  constraints (12):
    c: Coincident(g2,g1)
    c: Coincident(g2,g0)
    c: Coincident(g3,g-1)
    c: Coincident(g3,g0)
    c: Parallel(g0,g1)
    c: Equal(g0,g1)
    c: Perpendicular(g0,g2)
    c: PointOnObject(g0,g-3)
    c: Coincident(g1,g3)
    c: Distance(g2,g2) = 3
    c: Distance(g1,g1) = 8
    c: Parallel(g2,g-4)
FEATURE [PartDesign::Pocket] Pocket009
  BaseFeature = -> Pad004
  Direction = (0,0,-1)
  Length = 2
  Length2 = 5
  Profile = -> Sketch020
  ReferenceAxis = -> Sketch020 [N_Axis]
  Refine = true
  Suppressed = false
  Type = 0
FEATURE [PartDesign::Body] Body004  label="first_layer"
  AllowCompound = false
  Group = -> [Sketch006,Pad004,Sketch020,Pocket009]
  Origin = -> Origin004
  Placement = pos=(0,0,23) rot=(0,0,1;0rad)
  Tip = -> Pocket009
FEATURE [Sketcher::SketchObject] Sketch021
  ArcFitTolerance = 1e-06
  AttachmentSupport = -> [XY_Plane012]
  FullyConstrained = true
  MakeInternals = false
  MapMode = 5
  expr: Constraints[1] = VarSet.tube_inner_dia
  expr: Constraints[40] = 12.3 mm + 0.5 mm
  sketch-geometry (18):
    g0: Circle CenterX=0 CenterY=0 CenterZ=0 NormalX=0 NormalY=0 NormalZ=1 AngleXU=0 Radius=42.45
    g1: LineSegment [constr] StartX=0 StartY=0 StartZ=0 EndX=17.475 EndY=30.2676 EndZ=0
    g2: LineSegment [constr] StartX=0 StartY=0 StartZ=0 EndX=17.475 EndY=-30.2676 EndZ=0
    g3: ArcOfCircle CenterX=0 CenterY=0 CenterZ=0 NormalX=0 NormalY=0 NormalZ=1 AngleXU=0 Radius=12.5 StartAngle=5.23599 EndAngle=7.33038
    g4: ArcOfCircle CenterX=0 CenterY=0 CenterZ=0 NormalX=0 NormalY=0 NormalZ=1 AngleXU=0 Radius=34.95 StartAngle=5.23599 EndAngle=7.33038
    g5: LineSegment StartX=6.25 StartY=-10.8253 StartZ=0 EndX=4.07179 EndY=-23.0526 EndZ=0
    g6: LineSegment StartX=17.475 StartY=-30.2676 StartZ=0 EndX=4.07179 EndY=-23.0526 EndZ=0
    g7: LineSegment StartX=17.475 StartY=30.2676 StartZ=0 EndX=4.0718 EndY=23.0526 EndZ=0
    g8: LineSegment StartX=4.0718 StartY=23.0526 StartZ=0 EndX=6.25 EndY=10.8253 EndZ=0
    g9: LineSegment [constr] StartX=11 StartY=-19.0526 StartZ=0 EndX=4.07179 EndY=-23.0526 EndZ=0
    g10: LineSegment [constr] StartX=11 StartY=19.0526 StartZ=0 EndX=4.0718 EndY=23.0526 EndZ=0
    g11: LineSegment StartX=-17.65 StartY=6.4 StartZ=0 EndX=-17.65 EndY=-6.4 EndZ=0
    g12: LineSegment StartX=-17.65 StartY=-6.4 StartZ=0 EndX=5.85 EndY=-6.4 EndZ=0
    g13: LineSegment StartX=5.85 StartY=-6.4 StartZ=0 EndX=5.85 EndY=6.4 EndZ=0
    g14: LineSegment StartX=5.85 StartY=6.4 StartZ=0 EndX=-17.65 EndY=6.4 EndZ=0
    g15: GeomPoint [constr] X=-5.9 Y=0 Z=0
    g16: Circle CenterX=8.25 CenterY=0 CenterZ=0 NormalX=0 NormalY=0 NormalZ=1 AngleXU=0 Radius=0.75
    g17: Circle CenterX=-20.05 CenterY=0 CenterZ=0 NormalX=0 NormalY=0 NormalZ=1 AngleXU=0 Radius=0.75
  constraints (49):
    c: Coincident(g0,g-1)
    c: Diameter(g0) = 84.9
    c: Coincident(g1,g0)
    c: Coincident(g2,g0)
    c: Distance(g2,g2) = 34.95
    c: Angle(g2,g1) = 2.0944
    c: Angle(g1,g-2) = 0.523599
    c: Coincident(g3,g0)
    c: PointOnObject(g3,g1)
    c: PointOnObject(g3,g2)
    c: Diameter(g3) = 25
    c: Coincident(g4,g0)
    c: Coincident(g4,g2)
    c: Coincident(g1,g4)
    c: Coincident(g5,g3)
    c: Coincident(g6,g2)
    c: Coincident(g6,g5)
    c: Coincident(g7,g1)
    c: Coincident(g8,g7)
    c: Coincident(g8,g3)
    c: PointOnObject(g9,g2)
    c: Coincident(g9,g5)
    c: Perpendicular(g2,g9)
    c: PointOnObject(g10,g1)
    c: Coincident(g10,g7)
    c: Distance(g9,g-1) = 22
    c: Distance(g9,g5) = 8
    c: Distance(g10,g7) = 8
    c: Perpendicular(g1,g10)
    c: Distance(g10,g-1) = 22
    c: Coincident(g11,g12)
    c: Coincident(g12,g13)
    c: Coincident(g13,g14)
    c: Coincident(g14,g11)
    c: Vertical(g11)
    c: Vertical(g13)
    c: Horizontal(g12)
    c: Horizontal(g14)
    c: Symmetric(g13,g11,g15)
    c: PointOnObject(g15,g-1)
    c: DistanceY(g11,g11) = 12.8
    c: DistanceX(g14,g14) = 23.5
    c: DistanceX(g15,g-1) = 5.9
    c: Diameter(g16) = 1.5
    c: PointOnObject(g16,g-1)
    c: Diameter(g17) = 1.5
    c: PointOnObject(g17,g-1)
    c: Distance(g17,g11) = 2.4
    c: Distance(g16,g13) = 2.4
FEATURE [PartDesign::Pad] Pad010
  Direction = (0,0,1)
  Length = 17.5
  Length2 = 10
  Profile = -> Sketch021
  ReferenceAxis = -> Sketch021 [N_Axis]
  Refine = true
  Suppressed = false
  Type = 0
  expr: Length = VarSet.mdf_thick
FEATURE [PartDesign::Plane] DatumPlane002
  AttachmentOffset = pos=(0,0,42.45) rot=(0,0,1;0rad)
  AttachmentSupport = -> [YZ_Plane005]
  Length = 80.8428
  MapMode = 5
  Placement = pos=(42.45,0,0) rot=(0.57735,0.57735,0.57735;2.0944rad)
  ResizeMode = 0
  Width = 61.7548
  expr: .AttachmentOffset.Base.z = VarSet.tube_inner_dia / 2
FEATURE [Sketcher::SketchObject] Sketch022
  ArcFitTolerance = 1e-06
  AttachmentSupport = -> [DatumPlane002]
  FullyConstrained = true
  MakeInternals = false
  MapMode = 5
  Placement = pos=(42.45,0,0) rot=(0.57735,0.57735,0.57735;2.0944rad)
  expr: Constraints[2] = VarSet.mdf_thick / 2
  sketch-geometry (1):
    g0: Circle CenterX=0 CenterY=8.75 CenterZ=0 NormalX=0 NormalY=0 NormalZ=1 AngleXU=0 Radius=1.5
  constraints (3):
    c: PointOnObject(g0,g-2)
    c: Diameter(g0) = 3
    c: DistanceY(g-1,g0) = 8.75
FEATURE [PartDesign::Pocket] Pocket010
  BaseFeature = -> Fillet
  Direction = (-1,0,0)
  Length = 5
  Length2 = 5
  Profile = -> Sketch022
  ReferenceAxis = -> Sketch022 [N_Axis]
  Refine = true
  Suppressed = false
  Type = 0
FEATURE [Part::Part2DObjectPython] Shape2DView001  label="testtube-layer-7.3mm"  # Draft 2D object (typed FeaturePython)
  AutoUpdate = true
  Base = -> Body006
  Clip = false
  FuseArch = false
  HiddenLines = false
  InPlace = true
  OnlySolids = false
  Projection = (0,0,1)
  ProjectionMode = 0
  SegmentLength = 0.05
  Tessellation = false
  VisibleOnly = false
FEATURE [Part::Part2DObjectPython] Shape2DView003  label="servo-leg-2-7.3mm"  # Draft 2D object (typed FeaturePython)
  AutoUpdate = true
  Base = -> Body007
  Clip = false
  FuseArch = false
  HiddenLines = false
  InPlace = true
  OnlySolids = false
  Placement = pos=(-75,-9,0) rot=(0,0,1;0rad)
  Projection = (1,0,0)
  ProjectionMode = 0
  SegmentLength = 0.05
  Tessellation = false
  VisibleOnly = false
FEATURE [Part::Part2DObjectPython] Shape2DView005  label="second-layer-7.3mm"  # Draft 2D object (typed FeaturePython)
  AutoUpdate = true
  Base = -> Body002
  Clip = false
  FuseArch = false
  HiddenLines = false
  InPlace = true
  OnlySolids = false
  Placement = pos=(-29,88,0) rot=(0,0,1;0rad)
  Projection = (0,0,1)
  ProjectionMode = 0
  SegmentLength = 0.05
  Tessellation = false
  VisibleOnly = false
FEATURE [Part::Part2DObjectPython] Shape2DView007  label="first-layer-7.3mm"  # Draft 2D object (typed FeaturePython)
  AutoUpdate = true
  Base = -> Body004
  Clip = false
  FuseArch = false
  HiddenLines = false
  InPlace = true
  OnlySolids = false
  Placement = pos=(-117,88,0) rot=(0,0,1;0rad)
  Projection = (0,0,1)
  ProjectionMode = 0
  SegmentLength = 0.05
  Tessellation = false
  VisibleOnly = false
FEATURE [Part::Part2DObjectPython] Shape2DView008  label="servo-leg-1-7.3mm"  # Draft 2D object (typed FeaturePython)
  AutoUpdate = true
  Base = -> Body007
  Clip = false
  FuseArch = false
  HiddenLines = false
  InPlace = true
  OnlySolids = false
  Placement = pos=(-75,13,0) rot=(0,0,1;0rad)
  Projection = (1,0,0)
  ProjectionMode = 0
  SegmentLength = 0.05
  Tessellation = false
  VisibleOnly = false
FEATURE [PartDesign::Plane] DatumPlane003
  AttachmentOffset = pos=(0,0,26.7) rot=(0,0,1;0rad)
  AttachmentSupport = -> [XZ_Plane005]
  Length = 97.9307
  MapMode = 5
  Placement = pos=(0,-26.7,5.9e-15) rot=(1,0,0;1.5708rad)
  ResizeMode = 0
  Width = 63.0307
FEATURE [Sketcher::SketchObject] Sketch023
  ArcFitTolerance = 1e-06
  AttachmentSupport = -> [DatumPlane003]
  FullyConstrained = true
  MakeInternals = false
  MapMode = 5
  Placement = pos=(0,-26.7,5.9e-15) rot=(1,0,0;1.5708rad)
  sketch-geometry (2):
    g0: Circle CenterX=12.5 CenterY=6 CenterZ=0 NormalX=0 NormalY=0 NormalZ=1 AngleXU=0 Radius=0.75
    g1: Circle CenterX=-12.5 CenterY=6 CenterZ=0 NormalX=0 NormalY=0 NormalZ=1 AngleXU=0 Radius=0.75
  constraints (5):
    c: Diameter(g0) = 1.5
    c: Equal(g1,g0)
    c: Symmetric(g1,g0,g-2)
    c: DistanceX(g1,g0) = 25
    c: Distance(g1,g-1) = 6
FEATURE [PartDesign::Pocket] Pocket011
  BaseFeature = -> Pocket010
  Direction = (0,1,-2e-16)
  Length = 10
  Length2 = 5
  Profile = -> Sketch023
  ReferenceAxis = -> Sketch023 [N_Axis]
  Refine = true
  Suppressed = false
  Type = 0
FEATURE [Part::Feature] Part__Feature003  label="3472 v5"
  shape: bbox 31.4 x 11 x 1.6 mm, 71 faces (baked)
FEATURE [Part::Feature] Part__Feature004  label="3472 v006"
  shape: bbox 4 x 4 x 1.6 mm, 4 faces (baked)
FEATURE [Part::Feature] Part__Feature005  label="3472 v007"
  shape: bbox 4 x 4 x 1.6 mm, 4 faces (baked)
FEATURE [Part::Feature] Part__Feature006  label="3472 v008"
  shape: bbox 2 x 3 x 1.3 mm, 10 faces (baked)
FEATURE [Part::Feature] Part__Feature007  label="3472 v009"
  shape: bbox 2 x 3 x 1.3 mm, 10 faces (baked)
FEATURE [Part::Feature] Part__Feature008  label="3472 v010"
  shape: bbox 3 x 2.4 x 1 mm, 30 faces (baked)
FEATURE [Part::Feature] Part__Feature009  label="3472 v011"
  shape: bbox 1.25 x 1.25 x 1.6 mm, 4 faces (baked)
FEATURE [Part::Feature] Part__Feature010  label="3472 v012"
  shape: bbox 1.25 x 1.25 x 1.6 mm, 4 faces (baked)
FEATURE [Part::Feature] Part__Feature011  label="3472 v013"
  shape: bbox 1.25 x 1.25 x 1.6 mm, 4 faces (baked)
FEATURE [Part::Feature] Part__Feature012  label="3472 v014"
  shape: bbox 1.25 x 1.25 x 1.6 mm, 4 faces (baked)
FEATURE [Part::Feature] Part__Feature013  label="3472 v015"
  shape: bbox 1.25 x 1.25 x 1.6 mm, 4 faces (baked)
FEATURE [Part::Feature] Part__Feature014  label="3472 v016"
  shape: bbox 1.25 x 1.25 x 1.6 mm, 4 faces (baked)
FEATURE [Part::Feature] Part__Feature015  label="3472 v017"
  shape: bbox 1.25 x 1.25 x 1.6 mm, 4 faces (baked)
FEATURE [Part::Feature] Part__Feature016  label="3472 v018"
  shape: bbox 0.5894 x 0.95 x 0.05 mm, 8 faces (baked)
FEATURE [Part::Feature] Part__Feature017  label="3472 v019"
  shape: bbox 0.7473 x 0.95 x 0.05 mm, 10 faces (baked)
FEATURE [Part::Feature] Part__Feature018  label="3472 v020"
  shape: bbox 0.5938 x 0.95 x 0.05 mm, 14 faces (baked)
FEATURE [Part::Feature] Part__Feature019  label="3472 v021"
  shape: bbox 0.6806 x 0.9848 x 0.05 mm, 42 faces (baked)
FEATURE [Part::Feature] Part__Feature020  label="3472 v022"
  shape: bbox 0.5894 x 0.95 x 0.05 mm, 8 faces (baked)
FEATURE [Part::Feature] Part__Feature021  label="3472 v023"
  shape: bbox 0.6806 x 0.9848 x 0.05 mm, 42 faces (baked)
FEATURE [Part::Feature] Part__Feature022  label="3472 v024"
  shape: bbox 0.7444 x 0.95 x 0.05 mm, 16 faces (baked)
FEATURE [Part::Feature] Part__Feature023  label="3472 v025"
  shape: bbox 0.6864 x 0.95 x 0.05 mm, 18 faces (baked)
FEATURE [Part::Feature] Part__Feature024  label="3472 v026"
  shape: bbox 0.6763 x 0.95 x 0.05 mm, 20 faces (baked)
FEATURE [Part::Feature] Part__Feature025  label="3472 v027"
  shape: bbox 0.1202 x 0.95 x 0.05 mm, 6 faces (baked)
FEATURE [Part::Feature] Part__Feature026  label="3472 v028"
  shape: bbox 0.7458 x 0.95 x 0.05 mm, 14 faces (baked)
FEATURE [Part::Feature] Part__Feature027  label="3472 v029"
  shape: bbox 0.6763 x 0.95 x 0.05 mm, 20 faces (baked)
FEATURE [Part::Feature] Part__Feature028  label="3472 v030"
  shape: bbox 0.7212 x 0.9848 x 0.05 mm, 34 faces (baked)
FEATURE [Part::Feature] Part__Feature029  label="3472 v031"
  shape: bbox 0.6676 x 0.9587 x 0.05 mm, 42 faces (baked)
FEATURE [Part::Feature] Part__Feature030  label="3472 v032"
  shape: bbox 0.6676 x 0.9587 x 0.05 mm, 42 faces (baked)
FEATURE [Part::Feature] Part__Feature031  label="3472 v033"
  shape: bbox 0.7082 x 0.9848 x 0.05 mm, 28 faces (baked)
FEATURE [Part::Feature] Part__Feature032  label="3472 v034"
  shape: bbox 0.6748 x 0.95 x 0.05 mm, 16 faces (baked)
FEATURE [Part::Feature] Part__Feature033  label="3472 v035"
  shape: bbox 0.7762 x 0.95 x 0.05 mm, 18 faces (baked)
FEATURE [Part::Feature] Part__Feature034  label="3472 v036"
  shape: bbox 0.6314 x 0.95 x 0.05 mm, 20 faces (baked)
FEATURE [Part::Feature] Part__Feature035  label="3472 v037"
  shape: bbox 0.6024 x 0.95 x 0.05 mm, 14 faces (baked)
FEATURE [Part::Feature] Part__Feature036  label="3472 v038"
  shape: bbox 0.6748 x 0.95 x 0.05 mm, 16 faces (baked)
FEATURE [Part::Feature] Part__Feature037  label="3472 v039"
  shape: bbox 0.6951 x 0.7386 x 0.05 mm, 34 faces (baked)
FEATURE [Part::Feature] Part__Feature038  label="3472 v040"
  shape: bbox 0.6227 x 0.7212 x 0.05 mm, 21 faces (baked)
FEATURE [Part::Feature] Part__Feature039  label="3472 v041"
  shape: bbox 0.6806 x 0.9848 x 0.05 mm, 42 faces (baked)
FEATURE [Part::Feature] Part__Feature040  label="3472 v042"
  shape: bbox 0.6198 x 0.7212 x 0.05 mm, 19 faces (baked)
FEATURE [Part::Feature] Part__Feature041  label="3472 v043"
  shape: bbox 0.7473 x 0.95 x 0.05 mm, 10 faces (baked)
FEATURE [Part::Feature] Part__Feature042  label="3472 v044"
  shape: bbox 0.6951 x 0.7386 x 0.05 mm, 34 faces (baked)
FEATURE [Part::Feature] Part__Feature043  label="3472 v045"
  shape: bbox 0.656 x 0.9413 x 0.05 mm, 27 faces (baked)
FEATURE [Part::Feature] Part__Feature044  label="3472 v046"
  shape: bbox 0.7328 x 0.9239 x 0.05 mm, 21 faces (baked)
FEATURE [Part::Feature] Part__Feature045  label="3472 v047"
  shape: bbox 0.6806 x 0.9848 x 0.05 mm, 42 faces (baked)
FEATURE [Part::Feature] Part__Feature046  label="3472 v048"
  shape: bbox 0.7082 x 0.9848 x 0.05 mm, 28 faces (baked)
FEATURE [Part::Feature] Part__Feature047  label="3472 v049"
  shape: bbox 0.6676 x 0.9587 x 0.05 mm, 42 faces (baked)
FEATURE [Part::Feature] Part__Feature048  label="3472 v050"
  shape: bbox 0.6691 x 0.9239 x 0.05 mm, 15 faces (baked)
FEATURE [Part::Feature] Part__Feature049  label="3472 v051"
  shape: bbox 0.7082 x 0.9848 x 0.05 mm, 28 faces (baked)
FEATURE [Part::Feature] Part__Feature050  label="3472 v052"
  shape: bbox 0.6705 x 1.048 x 0.05 mm, 15 faces (baked)
FEATURE [Part::Feature] Part__Feature051  label="3472 v053"
  shape: bbox 0.6951 x 0.7386 x 0.05 mm, 34 faces (baked)
FEATURE [Part::Feature] Part__Feature052  label="3472 v054"
  shape: bbox 0.5662 x 0.7212 x 0.05 mm, 17 faces (baked)
FEATURE [Part::Feature] Part__Feature053  label="3472 v055"
  shape: bbox 0.6806 x 0.7386 x 0.05 mm, 31 faces (baked)
FEATURE [Part::Feature] Part__Feature054  label="3472 v056"
  shape: bbox 0.6589 x 0.7386 x 0.05 mm, 36 faces (baked)
FEATURE [Part::Feature] Part__Feature055  label="3472 v057"
  shape: bbox 0.5662 x 0.7212 x 0.05 mm, 17 faces (baked)
FEATURE [Part::Feature] Part__Feature056  label="3472 v058"
  shape: bbox 0.121 x 0.0995 x 0.01 mm, 6 faces (baked)
FEATURE [Part::Feature] Part__Feature057  label="3472 v059"
  shape: bbox 0.121 x 0.0995 x 0.01 mm, 6 faces (baked)
FEATURE [Part::Feature] Part__Feature058  label="3472 v060"
  shape: bbox 0.121 x 0.0995 x 0.01 mm, 6 faces (baked)
FEATURE [Part::Feature] Part__Feature059  label="3472 v061"
  shape: bbox 0.123 x 0.1015 x 0.01 mm, 6 faces (baked)
FEATURE [Part::Feature] Part__Feature060  label="3472 v062"
  shape: bbox 0.121 x 0.0995 x 0.01 mm, 6 faces (baked)
FEATURE [Part::Feature] Part__Feature061  label="3472 v063"
  shape: bbox 0.121 x 0.0995 x 0.01 mm, 6 faces (baked)
FEATURE [Part::Feature] Part__Feature062  label="3472 v064"
  shape: bbox 0.121 x 0.0995 x 0.01 mm, 6 faces (baked)
FEATURE [Part::Feature] Part__Feature063  label="3472 v065"
  shape: bbox 0.121 x 0.0995 x 0.01 mm, 6 faces (baked)
FEATURE [Part::Feature] Part__Feature064  label="3472 v066"
  shape: bbox 0.121 x 0.0995 x 0.01 mm, 6 faces (baked)
FEATURE [Part::Feature] Part__Feature065  label="3472 v067"
  shape: bbox 0.121 x 0.0995 x 0.01 mm, 6 faces (baked)
FEATURE [Part::Feature] Part__Feature066  label="3472 v068"
  shape: bbox 0.121 x 0.0995 x 0.01 mm, 6 faces (baked)
FEATURE [Part::Feature] Part__Feature067  label="3472 v069"
  shape: bbox 0.121 x 0.0995 x 0.01 mm, 6 faces (baked)
FEATURE [Part::Feature] Part__Feature068  label="3472 v070"
  shape: bbox 0.5938 x 0.95 x 0.05 mm, 14 faces (baked)
FEATURE [Part::Feature] Part__Feature069  label="3472 v071"
  shape: bbox 0.6748 x 0.95 x 0.05 mm, 16 faces (baked)
FEATURE [Part::Feature] Part__Feature070  label="3472 v072"
  shape: bbox 0.6314 x 0.95 x 0.05 mm, 20 faces (baked)
FEATURE [Part::Feature] Part__Feature071  label="3472 v073"
  shape: bbox 0.7444 x 0.95 x 0.05 mm, 16 faces (baked)
FEATURE [Part::Feature] Part__Feature072  label="3472 v074"
  shape: bbox 0.5894 x 0.95 x 0.05 mm, 8 faces (baked)
FEATURE [Part::Feature] Part__Feature073  label="3472 v075"
  shape: bbox 0.6806 x 0.9848 x 0.05 mm, 42 faces (baked)
FEATURE [Part::Feature] Part__Feature074  label="3472 v076"
  shape: bbox 0.6806 x 0.9848 x 0.05 mm, 42 faces (baked)
FEATURE [Part::Feature] Part__Feature075  label="3472 v077"
  shape: bbox 0.7473 x 0.95 x 0.05 mm, 10 faces (baked)
FEATURE [Part::Feature] Part__Feature076  label="3472 v078"
  shape: bbox 0.5938 x 0.95 x 0.05 mm, 14 faces (baked)
FEATURE [Part::Feature] Part__Feature077  label="3472 v079"
  shape: bbox 0.5894 x 0.95 x 0.05 mm, 8 faces (baked)
FEATURE [Part::Feature] Part__Feature078  label="3472 v080"
  shape: bbox 0.6024 x 0.95 x 0.05 mm, 14 faces (baked)
FEATURE [Part::Feature] Part__Feature079  label="3472 v081"
  shape: bbox 0.6748 x 0.95 x 0.05 mm, 16 faces (baked)
FEATURE [Part::Feature] Part__Feature080  label="3472 v082"
  shape: bbox 0.6314 x 0.95 x 0.05 mm, 20 faces (baked)
FEATURE [Part::Feature] Part__Feature081  label="3472 v083"
  shape: bbox 0.6748 x 0.95 x 0.05 mm, 16 faces (baked)
FEATURE [Part::Feature] Part__Feature082  label="3472 v084"
  shape: bbox 0.7762 x 0.95 x 0.05 mm, 18 faces (baked)
FEATURE [Part::Feature] Part__Feature083  label="3472 v085"
  shape: bbox 0.7082 x 0.9848 x 0.05 mm, 28 faces (baked)
FEATURE [Part::Feature] Part__Feature084  label="3472 v086"
  shape: bbox 0.6676 x 0.9587 x 0.05 mm, 42 faces (baked)
FEATURE [Part::Feature] Part__Feature085  label="3472 v087"
  shape: bbox 0.6676 x 0.9587 x 0.05 mm, 42 faces (baked)
FEATURE [Part::Feature] Part__Feature086  label="3472 v088"
  shape: bbox 0.6951 x 0.9848 x 0.05 mm, 34 faces (baked)
FEATURE [Part::Feature] Part__Feature087  label="3472 v089"
  shape: bbox 0.7444 x 0.95 x 0.05 mm, 16 faces (baked)
FEATURE [Part::Feature] Part__Feature088  label="3472 v090"
  shape: bbox 0.6314 x 0.95 x 0.05 mm, 20 faces (baked)
FEATURE [Part::Feature] Part__Feature089  label="3472 v091"
  shape: bbox 0.8 x 1.6 x 0.65 mm, 10 faces (baked)
FEATURE [Part::Feature] Part__Feature090  label="3472 v092"
  shape: bbox 0.8 x 1.6 x 0.65 mm, 10 faces (baked)
FEATURE [Part::Feature] Part__Feature091  label="3472 v093"
  shape: bbox 1.6 x 0.8 x 0.65 mm, 10 faces (baked)
FEATURE [Part::Feature] Part__Feature092  label="3472 v094"
  shape: bbox 0.8 x 1.6 x 0.65 mm, 10 faces (baked)
FEATURE [Part::Feature] Part__Feature093  label="3472 v095"
  shape: bbox 2.7 x 3 x 1 mm, 22 faces (baked)
FEATURE [Part::Feature] Part__Feature094  label="3472 v096"
  shape: bbox 3 x 2.5 x 1 mm, 22 faces (baked)
FEATURE [Part::Feature] Part__Feature095  label="3472 v097"
  shape: bbox 1.6 x 0.8 x 0.65 mm, 10 faces (baked)
FEATURE [Part::Feature] Part__Feature096  label="3472 v098"
  shape: bbox 1.6 x 0.8 x 0.65 mm, 10 faces (baked)
FEATURE [Part::Feature] Part__Feature097  label="3472 v099"
  shape: bbox 0.8 x 1.6 x 0.65 mm, 10 faces (baked)
FEATURE [Part::Feature] Part__Feature098  label="3472 v100"
  shape: bbox 2 x 0.8 x 1.05 mm, 10 faces (baked)
FEATURE [Part::Feature] Part__Feature099  label="3472 v101"
  shape: bbox 2 x 0.8 x 1.05 mm, 10 faces (baked)
FEATURE [Part::Feature] Part__Feature100  label="3472 v102"
  shape: bbox 3.45 x 3 x 1 mm, 30 faces (baked)
FEATURE [Part::Feature] Part__Feature101  label="3472 v103"
  shape: bbox 3 x 2.5 x 1 mm, 22 faces (baked)
FEATURE [Part::Feature] Part__Feature102  label="3472 v104"
  shape: bbox 2 x 0.8 x 1.05 mm, 10 faces (baked)
FEATURE [App::Part] _472_v5  label="color-sensor"
  Group = -> [Part__Feature003,Part__Feature004,Part__Feature005,Part__Feature006,Part__Feature007,Part__Feature008,Part__Feature009,Part__Feature010,Part__Feature011,Part__Feature012,Part__Feature013,Part__Feature014,Part__Feature015,Part__Feature016,Part__Feature017,Part__Feature018,Part__Feature019,Part__Feature020,Part__Feature021,Part__Feature022,Part__Feature023,Part__Feature024,Part__Feature025,+77 more]
  Origin = -> Origin013
FEATURE [PartDesign::Plane] DatumPlane004
  AttachmentOffset = pos=(0,0,42.45) rot=(0,0,1;0rad)
  AttachmentSupport = -> [XZ_Plane]
  Length = 97.9307
  MapMode = 5
  Placement = pos=(0,-42.45,9.4e-15) rot=(1,0,0;1.5708rad)
  ResizeMode = 0
  Width = 63.0307
  expr: .AttachmentOffset.Base.z = VarSet.tube_inner_dia / 2
FEATURE [Sketcher::SketchObject] Sketch024
  ArcFitTolerance = 1e-06
  AttachmentSupport = -> [DatumPlane004]
  FullyConstrained = true
  MakeInternals = false
  MapMode = 5
  Placement = pos=(0,-42.45,9.4e-15) rot=(1,0,0;1.5708rad)
  expr: Constraints[2] = VarSet.mdf_thickness / 2
  sketch-geometry (1):
    g0: Circle CenterX=0 CenterY=3.75 CenterZ=0 NormalX=0 NormalY=0 NormalZ=1 AngleXU=0 Radius=1
  constraints (3):
    c: Diameter(g0) = 2
    c: PointOnObject(g0,g-2)
    c: Distance(g0,g-1) = 3.75
FEATURE [PartDesign::Pocket] Pocket012
  BaseFeature = -> Pocket003
  Direction = (0,1,-2e-16)
  Length = 6
  Length2 = 5
  Profile = -> Sketch024
  ReferenceAxis = -> Sketch024 [N_Axis]
  Refine = true
  Suppressed = false
  Type = 0
FEATURE [PartDesign::PolarPattern] PolarPattern001
  Angle = 180
  Axis = -> Z_Axis
  BaseFeature = -> Pocket012
  Mode = 0
  Occurrences = 3
  Offset = 120
  Originals = -> [Pocket012]
  Refine = true
  Reversed = true
  Suppressed = false
  TransformMode = 0
FEATURE [PartDesign::Body] Body  label="ring_spacer"
  AllowCompound = false
  Group = -> [Sketch,Pad,DatumPlane001,Sketch011,Pocket003,DatumPlane004,Sketch024,Pocket012,PolarPattern001]
  Origin = -> Origin
  Placement = pos=(0,0,-12) rot=(0,0,1;0rad)
  Tip = -> PolarPattern001
FEATURE [Part::Part2DObjectPython] Shape2DView004  label="ring-spacer-7.3mm"  # Draft 2D object (typed FeaturePython)
  AutoUpdate = true
  Base = -> Body
  Clip = false
  FuseArch = false
  HiddenLines = false
  InPlace = true
  OnlySolids = false
  Placement = pos=(-89,0,0) rot=(0,0,1;0rad)
  Projection = (0,0,1)
  ProjectionMode = 0
  SegmentLength = 0.05
  Tessellation = false
  VisibleOnly = false
FEATURE [App::DocumentObjectGroup] Group001  label="7.3mm"
  Group = -> [Shape2DView003,Shape2DView004,Shape2DView005,Shape2DView007,Shape2DView001,Shape2DView008]
FEATURE [PartDesign::Plane] DatumPlane005
  AttachmentOffset = pos=(0,0,42.45) rot=(0,0,1;0rad)
  AttachmentSupport = -> [YZ_Plane012]
  Length = 97.8895
  MapMode = 5
  Placement = pos=(42.45,0,0) rot=(0.57735,0.57735,0.57735;2.0944rad)
  ResizeMode = 0
  Width = 63.0278
  expr: .AttachmentOffset.Base.z = VarSet.tube_inner_dia / 2
FEATURE [Sketcher::SketchObject] Sketch025
  ArcFitTolerance = 1e-06
  AttachmentSupport = -> [DatumPlane005]
  FullyConstrained = true
  MakeInternals = false
  MapMode = 5
  Placement = pos=(42.45,0,0) rot=(0.57735,0.57735,0.57735;2.0944rad)
  expr: Constraints[2] = VarSet.mdf_thick / 2
  sketch-geometry (1):
    g0: Circle CenterX=0 CenterY=8.75 CenterZ=0 NormalX=0 NormalY=0 NormalZ=1 AngleXU=0 Radius=1
  constraints (3):
    c: Diameter(g0) = 2
    c: PointOnObject(g0,g-2)
    c: Distance(g0,g-1) = 8.75
FEATURE [PartDesign::Pocket] Pocket013
  BaseFeature = -> Pad010
  Direction = (-1,0,0)
  Length = 5
  Length2 = 5
  Profile = -> Sketch025
  ReferenceAxis = -> Sketch025 [N_Axis]
  Refine = true
  Suppressed = false
  Type = 0
FEATURE [PartDesign::PolarPattern] PolarPattern002
  Angle = 180
  Axis = -> Z_Axis012
  BaseFeature = -> Pocket013
  Mode = 0
  Occurrences = 3
  Offset = 120
  Originals = -> [Pocket013]
  Refine = true
  Suppressed = false
  TransformMode = 0
FEATURE [PartDesign::Body] Body010  label="top_layer"
  AllowCompound = false
  Group = -> [Sketch021,Pad010,DatumPlane005,Sketch025,Pocket013,PolarPattern002]
  Origin = -> Origin012
  Tip = -> PolarPattern002
FEATURE [Part::Part2DObjectPython] Shape2DView  label="top-layer-17mm"  # Draft 2D object (typed FeaturePython)
  AutoUpdate = true
  Base = -> Body010
  Clip = false
  FuseArch = false
  HiddenLines = false
  InPlace = true
  OnlySolids = false
  Projection = (0,0,1)
  ProjectionMode = 0
  SegmentLength = 0.05
  Tessellation = false
  VisibleOnly = false
FEATURE [Part::FeaturePython] Screw001  label="#3x3/8in-Screw"  # WARN: FeaturePython — macro-defined, semantics opaque (R4)
  Diameter = 4
  Invert = false
  LeftHanded = false
  Length = 4
  LengthCustom = 9.525
  MatchOuter = false
  OffsetAngle = 0
  Placement = pos=(0,-66,67) rot=(1,0,0;1.5708rad)
  Thread = false
  Type = 25
FEATURE [Part::FeaturePython] Screw  label="#2x1/4in-Screw"  # WARN: FeaturePython — macro-defined, semantics opaque (R4)
  Diameter = 3
  Invert = false
  LeftHanded = false
  Length = 0
  LengthCustom = 6.35
  MatchOuter = false
  OffsetAngle = 0
  Thread = false
  Type = 15
FEATURE [App::DocumentObjectGroup] Group004  label="Screws"
  Group = -> [Screw,Screw001]
FEATURE [Part::Feature] Part__Feature114  label="1x7 Male Pin Header"
  shape: bbox 0.64 x 13.54 x 0.64 mm, 14 faces (baked)
FEATURE [Part::Feature] Part__Feature115  label="1x7 Male Pin Header001"
  shape: bbox 0.64 x 13.54 x 0.64 mm, 14 faces (baked)
FEATURE [Part::Feature] Part__Feature116  label="1x7 Male Pin Header002"
  shape: bbox 0.64 x 13.54 x 0.64 mm, 14 faces (baked)
FEATURE [Part::Feature] Part__Feature117  label="1x7 Male Pin Header003"
  shape: bbox 0.64 x 13.54 x 0.64 mm, 14 faces (baked)
FEATURE [Part::Feature] Part__Feature118  label="1x7 Male Pin Header004"
  shape: bbox 0.64 x 13.54 x 0.64 mm, 14 faces (baked)
FEATURE [Part::Feature] Part__Feature119  label="1x7 Male Pin Header005"
  shape: bbox 0.64 x 13.54 x 0.64 mm, 14 faces (baked)
FEATURE [Part::Feature] Part__Feature120  label="1x7 Male Pin Header006"
  shape: bbox 0.64 x 13.54 x 0.64 mm, 14 faces (baked)
FEATURE [Part::Feature] Part__Feature121  label="1x7 Male Pin Header007"
  shape: bbox 17.79 x 2.54 x 2.5 mm, 176 faces (baked)
FEATURE [App::Part] _x7_Male_Pin_Header  label="1x7 Male Pin Header008"
  Group = -> [Part__Feature114,Part__Feature115,Part__Feature116,Part__Feature117,Part__Feature118,Part__Feature119,Part__Feature120,Part__Feature121]
  Origin = -> Origin015
FEATURE [Part::Feature] Part__Feature122  label="axe"
  shape: bbox 4.9 x 4.9 x 14.45 mm, 124 faces (baked)
FEATURE [Part::Feature] Part__Feature123  label="base001"
  shape: bbox 32.3 x 12.2 x 28.5 mm, 43 faces (baked)
FEATURE [Part::Feature] Part__Feature124  label="etiquette"
  shape: bbox 20 x 0.2 x 10 mm, 340 faces (baked)
FEATURE [Part::Feature] Part__Feature125  label="Tube"
  Placement = pos=(5.4,0,-13.3) rot=(0,1,0;1.5708rad)
  shape: bbox 3 x 1.2 x 1.2 mm, 4 faces (baked)
FEATURE [Part::Feature] Part__Feature126  label="Cylindre"
  Placement = pos=(5.4,0,-13.3) rot=(0,1,0;1.5708rad)
  shape: bbox 4 x 0.4 x 0.4 mm, 3 faces (baked)
FEATURE [Part::Feature] Part__Feature127  label="Tube001"
  Placement = pos=(5.4,-1.2,-13.3) rot=(0,1,0;1.5708rad)
  shape: bbox 3 x 1.2 x 1.2 mm, 4 faces (baked)
FEATURE [Part::Feature] Part__Feature128  label="Tube002"
  Placement = pos=(5.4,1.2,-13.3) rot=(0,1,0;1.5708rad)
  shape: bbox 3 x 1.2 x 1.2 mm, 4 faces (baked)
FEATURE [Part::Feature] Part__Feature129  label="etiquette001"
  Placement = pos=(-10.8,1e-15,0) rot=(0,0,1;3.14159rad)
  shape: bbox 20 x 0.2 x 10 mm, 340 faces (baked)
FEATURE [Part::Feature] Part__Feature130  label="Cylindre001"
  Placement = pos=(5.4,1.2,-13.3) rot=(0,1,0;1.5708rad)
  shape: bbox 4 x 0.4 x 0.4 mm, 3 faces (baked)
FEATURE [Part::Feature] Part__Feature131  label="Cylindre002"
  Placement = pos=(5.4,-1.2,-13.3) rot=(0,1,0;1.5708rad)
  shape: bbox 4 x 0.4 x 0.4 mm, 3 faces (baked)
FEATURE [App::Part] M90S_ali
  Group = -> [Part__Feature122,Part__Feature123,Part__Feature124,Part__Feature125,Part__Feature126,Part__Feature127,Part__Feature128,Part__Feature129,Part__Feature130,Part__Feature131]
  Origin = -> Origin017
FEATURE [App::Link] Body011  label="001_Body"
  LinkPlacement = pos=(0,0,0) rot=(1,0,0;3.14159rad)
  LinkedObject = -> <external Pipe.FCStd>#Body
  Placement = pos=(0,0,0) rot=(1,0,0;3.14159rad)
FEATURE [App::FeaturePython] GroundedJoint  # Assembly grounded joint (typed FeaturePython)
  ObjectToGround = -> Body011
  Placement = pos=(0,0,0) rot=(1,0,0;3.14159rad)
FEATURE [App::Link] ring_spacer  label="002_ring_spacer001"
  LinkPlacement = pos=(0,0,-60) rot=(0,0,1;3.14159rad)
  LinkedObject = -> Body
  Placement = pos=(0,0,-60) rot=(0,0,1;3.14159rad)
FEATURE [App::FeaturePython] Joint  label="Fixed"  # Assembly joint (typed FeaturePython)
  Activated = true
  AngleMax = 0
  AngleMin = 0
  Detach1 = false
  Detach2 = false
  Distance = 0
  Distance2 = 0
  EnableAngleMax = false
  EnableAngleMin = false
  EnableLengthMax = false
  EnableLengthMin = false
  JointType = 0 (Fixed)
  LengthMax = 0
  LengthMin = 0
  Offset2 = pos=(0,0,0) rot=(0,0,1;3.14159rad)
  Placement2 = pos=(0,0,60) rot=(0,0,1;3.14159rad)
  Reference1 = -> Assembly [ring_spacer.Edge3,ring_spacer.Edge3]
  Reference2 = -> Assembly [Body011.Edge11,Body011.Edge11]
FEATURE [App::Link] _3x3_8in_Screw  label="003_#3x3/8in-Screw001"
  LinkPlacement = pos=(6.6e-15,-45.975,-56.25) rot=(0.57735,-0.57735,0.57735;2.0944rad)
  LinkedObject = -> Screw001
  Placement = pos=(6.6e-15,-45.975,-56.25) rot=(0.57735,-0.57735,0.57735;2.0944rad)
FEATURE [App::Link] _3x3_8in_Screw001  label="004_#3x3/8in-Screw002"
  LinkPlacement = pos=(45.975,6.3e-15,-56.25) rot=(0.707107,0,0.707107;3.14159rad)
  LinkedObject = -> Screw001
  Placement = pos=(45.975,6.3e-15,-56.25) rot=(0.707107,0,0.707107;3.14159rad)
FEATURE [App::Link] _3x3_8in_Screw002  label="005_#3x3/8in-Screw003"
  LinkPlacement = pos=(-5.9e-15,45.975,-56.25) rot=(-0.57735,-0.57735,-0.57735;2.0944rad)
  LinkedObject = -> Screw001
  Placement = pos=(-5.9e-15,45.975,-56.25) rot=(-0.57735,-0.57735,-0.57735;2.0944rad)
FEATURE [App::FeaturePython] Joint001  label="Fixed001"  # Assembly joint (typed FeaturePython)
  Activated = true
  AngleMax = 0
  AngleMin = 0
  Detach1 = false
  Detach2 = false
  Distance = 0
  Distance2 = 0
  EnableAngleMax = false
  EnableAngleMin = false
  EnableLengthMax = false
  EnableLengthMin = false
  JointType = 0 (Fixed)
  LengthMax = 0
  LengthMin = 0
  Placement1 = pos=(0,3.2e-15,-9.525) rot=(0,0,1;0rad)
  Placement2 = pos=(-4e-16,36.45,3.75) rot=(0.57735,-0.57735,0.57735;2.0944rad)
  Reference1 = -> Assembly [_3x3_8in_Screw.Edge1,_3x3_8in_Screw.Edge1]
  Reference2 = -> Assembly [ring_spacer.Face12,ring_spacer.Face12]
FEATURE [App::FeaturePython] Joint002  label="Fixed002"  # Assembly joint (typed FeaturePython)
  Activated = true
  AngleMax = 0
  AngleMin = 0
  Detach1 = false
  Detach2 = false
  Distance = 0
  Distance2 = 0
  EnableAngleMax = false
  EnableAngleMin = false
  EnableLengthMax = false
  EnableLengthMin = false
  JointType = 0 (Fixed)
  LengthMax = 0
  LengthMin = 0
  Placement1 = pos=(0,0,-9.525) rot=(0,0,1;0rad)
  Placement2 = pos=(-36.45,-6e-16,3.75) rot=(-0.707107,0,-0.707107;3.14159rad)
  Reference1 = -> Assembly [_3x3_8in_Screw001.Edge1,_3x3_8in_Screw001.Edge1]
  Reference2 = -> Assembly [ring_spacer.Face13,ring_spacer.Face13]
FEATURE [App::FeaturePython] Joint003  label="Fixed003"  # Assembly joint (typed FeaturePython)
  Activated = true
  AngleMax = 0
  AngleMin = 0
  Detach1 = false
  Detach2 = false
  Distance = 0
  Distance2 = 0
  EnableAngleMax = false
  EnableAngleMin = false
  EnableLengthMax = false
  EnableLengthMin = false
  JointType = 0 (Fixed)
  LengthMax = 0
  LengthMin = 0
  Placement1 = pos=(0,-36.45,3.75) rot=(-0.57735,-0.57735,-0.57735;2.0944rad)
  Placement2 = pos=(0,-1.1e-15,-9.525) rot=(0,0,1;0rad)
  Reference1 = -> Assembly [ring_spacer.Face14,ring_spacer.Edge1]
  Reference2 = -> Assembly [_3x3_8in_Screw002.Edge1,_3x3_8in_Screw002.Edge1]
FEATURE [App::Link] second_layer  label="006_second_layer001"
  LinkPlacement = pos=(0,0,-52.5) rot=(0,0,1;1.5708rad)
  LinkedObject = -> Body002
  Placement = pos=(0,0,-52.5) rot=(0,0,1;1.5708rad)
FEATURE [App::FeaturePython] Joint004  label="Fixed004"  # Assembly joint (typed FeaturePython)
  Activated = true
  AngleMax = 0
  AngleMin = 0
  Detach1 = false
  Detach2 = false
  Distance = 0
  Distance2 = 0
  EnableAngleMax = false
  EnableAngleMin = false
  EnableLengthMax = false
  EnableLengthMin = false
  JointType = 0 (Fixed)
  LengthMax = 0
  LengthMin = 0
  Offset2 = pos=(0,0,-7.5) rot=(0,0,-1;1.5708rad)
  Placement2 = pos=(0,0,52.5) rot=(0,0,-1;1.5708rad)
  Reference1 = -> Assembly [second_layer.Edge1,second_layer.Edge1]
  Reference2 = -> Assembly [Body011.Edge11,Body011.Edge11]
FEATURE [PartDesign::Plane] DatumPlane006
  AttachmentOffset = pos=(0,0,-42.45) rot=(0,0,1;0rad)
  AttachmentSupport = -> [YZ_Plane005]
  Length = 80.8428
  MapMode = 5
  Placement = pos=(-42.45,0,0) rot=(0.57735,0.57735,0.57735;2.0944rad)
  ResizeMode = 0
  Width = 61.7548
FEATURE [Sketcher::SketchObject] Sketch026
  ArcFitTolerance = 1e-06
  AttachmentSupport = -> [DatumPlane006]
  FullyConstrained = true
  MakeInternals = false
  MapMode = 5
  Placement = pos=(-42.45,0,0) rot=(0.57735,0.57735,0.57735;2.0944rad)
  expr: Constraints[2] = VarSet.mdf_thick / 2
  sketch-geometry (1):
    g0: Circle CenterX=0 CenterY=8.75 CenterZ=0 NormalX=0 NormalY=0 NormalZ=1 AngleXU=0 Radius=1.5
  constraints (3):
    c: PointOnObject(g0,g-2)
    c: Diameter(g0) = 3
    c: Distance(g0,g-1) = 8.75
FEATURE [PartDesign::Pocket] Pocket014
  BaseFeature = -> Pocket011
  Direction = (-1,0,0)
  Length = 5
  Length2 = 5
  Profile = -> Sketch026
  ReferenceAxis = -> Sketch026 [N_Axis]
  Refine = true
  Reversed = true
  Suppressed = false
  Type = 0
FEATURE [PartDesign::Body] Body005  label="color_sensor_layer"
  AllowCompound = false
  Group = -> [Sketch007,Pad005,Fillet,DatumPlane002,Sketch022,Pocket010,DatumPlane003,Sketch023,Pocket011,DatumPlane006,Sketch026,Pocket014]
  Origin = -> Origin005
  Placement = pos=(0,0,8) rot=(0,0,1;0rad)
  Tip = -> Pocket014
FEATURE [Part::Part2DObjectPython] Shape2DView006  label="color-sensor-layer-17mm"  # Draft 2D object (typed FeaturePython)
  AutoUpdate = true
  Base = -> Body005
  Clip = false
  FuseArch = false
  HiddenLines = false
  InPlace = true
  OnlySolids = false
  Placement = pos=(0,74,0) rot=(0,0,1;0rad)
  Projection = (0,0,1)
  ProjectionMode = 0
  SegmentLength = 0.05
  Tessellation = false
  VisibleOnly = false
FEATURE [App::DocumentObjectGroup] Group002  label="17mm"
  Group = -> [Shape2DView006,Shape2DView]
FEATURE [App::DocumentObjectGroup] Group  label="mdf-cuts"
  Group = -> [Group001,Group002]
FEATURE [App::Link] color_sensor_layer  label="007_color_sensor_layer001"
  LinkPlacement = pos=(0,0,-44) rot=(0,0,1;1.5708rad)
  LinkedObject = -> Body005
  Placement = pos=(0,0,-44) rot=(0,0,1;1.5708rad)
FEATURE [App::FeaturePython] Joint005  label="Fixed005"  # Assembly joint (typed FeaturePython)
  Activated = true
  AngleMax = 0
  AngleMin = 0
  Detach1 = false
  Detach2 = false
  Distance = 0
  Distance2 = 0
  EnableAngleMax = false
  EnableAngleMin = false
  EnableLengthMax = false
  EnableLengthMin = false
  JointType = 0 (Fixed)
  LengthMax = 0
  LengthMin = 0
  Offset2 = pos=(0,0,-16) rot=(0,0,-1;1.5708rad)
  Placement2 = pos=(0,0,44) rot=(0,0,-1;1.5708rad)
  Reference1 = -> Assembly [color_sensor_layer.Edge1,color_sensor_layer.Edge1]
  Reference2 = -> Assembly [Body011.Edge11,Body011.Edge11]
FEATURE [App::Link] color_sensor  label="008_color-sensor001"
  LinkPlacement = pos=(27.438,-0.2,-38) rot=(-0.57735,0.57735,0.57735;4.18879rad)
  LinkedObject = -> _472_v5
  Placement = pos=(27.438,-0.2,-38) rot=(-0.57735,0.57735,0.57735;4.18879rad)
FEATURE [App::Link] _x7_Male_Pin_Header008  label="009_1x7 Male Pin Header009"
  LinkPlacement = pos=(28.238,-7.82,-42) rot=(0.707107,0.707107,0;3.14159rad)
  LinkedObject = -> _x7_Male_Pin_Header
  Placement = pos=(28.238,-7.82,-42) rot=(0.707107,0.707107,0;3.14159rad)
FEATURE [App::Link] _3x3_8in_Screw003  label="010_#3x3/8in-Screw004"
  LinkPlacement = pos=(29.225,-12.5,-38) rot=(0.707107,0,0.707107;3.14159rad)
  LinkedObject = -> Screw001
  Placement = pos=(29.225,-12.5,-38) rot=(0.707107,0,0.707107;3.14159rad)
FEATURE [App::Link] _3x3_8in_Screw004  label="011_#3x3/8in-Screw005"
  LinkPlacement = pos=(29.225,12.5,-38) rot=(0.707107,0,0.707107;3.14159rad)
  LinkedObject = -> Screw001
  Placement = pos=(29.225,12.5,-38) rot=(0.707107,0,0.707107;3.14159rad)
FEATURE [App::Link] _3x3_8in_Screw005  label="012_#3x3/8in-Screw006"
  LinkPlacement = pos=(-1.08e-14,-46.975,-35.25) rot=(-0.57735,0.57735,-0.57735;4.18879rad)
  LinkedObject = -> Screw001
  Placement = pos=(-1.08e-14,-46.975,-35.25) rot=(-0.57735,0.57735,-0.57735;4.18879rad)
FEATURE [App::FeaturePython] Joint006  label="Fixed006"  # Assembly joint (typed FeaturePython)
  Activated = true
  AngleMax = 0
  AngleMin = 0
  Detach1 = false
  Detach2 = false
  Distance = 0
  Distance2 = 0
  EnableAngleMax = false
  EnableAngleMin = false
  EnableLengthMax = false
  EnableLengthMin = false
  JointType = 0 (Fixed)
  LengthMax = 0
  LengthMin = 0
  Offset2 = pos=(0,0,0) rot=(0,0,1;3.14159rad)
  Placement1 = pos=(-12.7,0,0.8) rot=(1,0,0;3.14159rad)
  Placement2 = pos=(12.5,-26.638,6) rot=(0,-0.707107,0.707107;3.14159rad)
  Reference1 = -> Assembly [color_sensor.Part__Feature004.Edge4,color_sensor.Part__Feature004.Edge4]
  Reference2 = -> Assembly [color_sensor_layer.Edge34,color_sensor_layer.Edge34]
FEATURE [App::FeaturePython] Joint007  label="Fixed007"  # Assembly joint (typed FeaturePython)
  Activated = true
  AngleMax = 0
  AngleMin = 0
  Detach1 = false
  Detach2 = false
  Distance = 0
  Distance2 = 0
  EnableAngleMax = false
  EnableAngleMin = false
  EnableLengthMax = false
  EnableLengthMin = false
  JointType = 0 (Fixed)
  LengthMax = 0
  LengthMin = 0
  Offset2 = pos=(0,0,-3) rot=(0,0,1;0rad)
  Placement1 = pos=(0,-1.8e-15,-9.525) rot=(0,0,1;0rad)
  Placement2 = pos=(-12.5,-19.7,6) rot=(-0.57735,-0.57735,-0.57735;2.0944rad)
  Reference1 = -> Assembly [_3x3_8in_Screw003.Edge1,_3x3_8in_Screw003.Edge1]
  Reference2 = -> Assembly [color_sensor_layer.Face19,color_sensor_layer.Face19]
FEATURE [App::FeaturePython] Joint008  label="Fixed008"  # Assembly joint (typed FeaturePython)
  Activated = true
  AngleMax = 0
  AngleMin = 0
  Detach1 = false
  Detach2 = false
  Distance = 0
  Distance2 = 0
  EnableAngleMax = false
  EnableAngleMin = false
  EnableLengthMax = false
  EnableLengthMin = false
  JointType = 0 (Fixed)
  LengthMax = 0
  LengthMin = 0
  Offset2 = pos=(0,0,-3) rot=(0,0,1;0rad)
  Placement1 = pos=(7.1e-15,-1.8e-15,-9.525) rot=(0,0,1;0rad)
  Placement2 = pos=(12.5,-19.7,6) rot=(-0.57735,-0.57735,-0.57735;2.0944rad)
  Reference1 = -> Assembly [_3x3_8in_Screw004.Edge1,_3x3_8in_Screw004.Edge1]
  Reference2 = -> Assembly [color_sensor_layer.Face18,color_sensor_layer.Face18]
FEATURE [App::FeaturePython] Joint009  label="Fixed009"  # Assembly joint (typed FeaturePython)
  Activated = true
  AngleMax = 0
  AngleMin = 0
  Detach1 = false
  Detach2 = false
  Distance = 0
  Distance2 = 0
  EnableAngleMax = false
  EnableAngleMin = false
  EnableLengthMax = false
  EnableLengthMin = false
  JointType = 0 (Fixed)
  LengthMax = 0
  LengthMin = 0
  Offset2 = pos=(0,0,3) rot=(0,0,1;1.5708rad)
  Placement1 = pos=(7.62,-3,1e-16) rot=(0.57735,0.57735,0.57735;4.18879rad)
  Placement2 = pos=(1.1e-15,-4,2.2) rot=(0,0,1;4.71239rad)
  Reference1 = -> Assembly [_x7_Male_Pin_Header008.Part__Feature117.Face6,_x7_Male_Pin_Header008.Part__Feature117.Face6]
  Reference2 = -> Assembly [color_sensor.Part__Feature011.Edge3,color_sensor.Part__Feature011.Edge3]
FEATURE [App::FeaturePython] Joint010  label="Fixed010"  # Assembly joint (typed FeaturePython)
  Activated = true
  AngleMax = 0
  AngleMin = 0
  Detach1 = false
  Detach2 = false
  Distance = 0
  Distance2 = 0
  EnableAngleMax = false
  EnableAngleMin = false
  EnableLengthMax = false
  EnableLengthMin = false
  JointType = 0 (Fixed)
  LengthMax = 0
  LengthMin = 0
  Placement1 = pos=(0,2.1e-15,-9.525) rot=(0,0,1;0rad)
  Placement2 = pos=(-37.45,3e-16,8.75) rot=(0.707107,0,0.707107;3.14159rad)
  Reference1 = -> Assembly [_3x3_8in_Screw005.Edge1,_3x3_8in_Screw005.Edge1]
  Reference2 = -> Assembly [color_sensor_layer.Face15,color_sensor_layer.Face15]
FEATURE [App::Link] _3x3_8in_Screw006  label="013_#3x3/8in-Screw007"
  LinkPlacement = pos=(1.03e-14,46.975,-35.25) rot=(0.57735,0.57735,0.57735;4.18879rad)
  LinkedObject = -> Screw001
  Placement = pos=(1.03e-14,46.975,-35.25) rot=(0.57735,0.57735,0.57735;4.18879rad)
FEATURE [App::FeaturePython] Joint011  label="Fixed011"  # Assembly joint (typed FeaturePython)
  Activated = true
  AngleMax = 0
  AngleMin = 0
  Detach1 = false
  Detach2 = false
  Distance = 0
  Distance2 = 0
  EnableAngleMax = false
  EnableAngleMin = false
  EnableLengthMax = false
  EnableLengthMin = false
  JointType = 0 (Fixed)
  LengthMax = 0
  LengthMin = 0
  Placement1 = pos=(0,-2.1e-15,-9.525) rot=(0,0,1;0rad)
  Placement2 = pos=(37.45,1e-16,8.75) rot=(0.707107,0,0.707107;3.14159rad)
  Reference1 = -> Assembly [_3x3_8in_Screw006.Edge1,_3x3_8in_Screw006.Edge1]
  Reference2 = -> Assembly [color_sensor_layer.Face14,color_sensor_layer.Face14]
FEATURE [App::Link] first_layer  label="014_first_layer001"
  LinkPlacement = pos=(0,0,-26) rot=(0,0,1;0.785398rad)
  LinkedObject = -> Body004
  Placement = pos=(0,0,-26) rot=(0,0,1;0.785398rad)
FEATURE [App::FeaturePython] Joint012  label="Fixed012"  # Assembly joint (typed FeaturePython)
  Activated = true
  AngleMax = 0
  AngleMin = 0
  Detach1 = false
  Detach2 = false
  Distance = 0
  Distance2 = 0
  EnableAngleMax = false
  EnableAngleMin = false
  EnableLengthMax = false
  EnableLengthMin = false
  JointType = 0 (Fixed)
  LengthMax = 0
  LengthMin = 0
  Offset2 = pos=(0,0,-34) rot=(0,0,-1;0.785398rad)
  Placement2 = pos=(0,0,26) rot=(0,0,-1;0.785398rad)
  Reference1 = -> Assembly [first_layer.Edge1,first_layer.Edge1]
  Reference2 = -> Assembly [Body011.Edge11,Body011.Edge11]
FEATURE [App::Link] shaft  label="015_shaft001"
  LinkPlacement = pos=(-3.57e-14,2.714e-13,-49) rot=(0,0,1;1.5708rad)
  LinkedObject = -> Part__Feature002
  Placement = pos=(-3.57e-14,2.714e-13,-49) rot=(0,0,1;1.5708rad)
FEATURE [App::Link] M90S_ali001  label="016_M90S_ali001"
  LinkPlacement = pos=(-3.57e-14,2.714e-13,5.2) rot=(-0.707107,0.707107,0;3.14159rad)
  LinkedObject = -> M90S_ali
  Placement = pos=(-3.57e-14,2.714e-13,5.2) rot=(-0.707107,0.707107,0;3.14159rad)
FEATURE [App::FeaturePython] Joint013  label="Fixed013"  # Assembly joint (typed FeaturePython)
  Activated = true
  AngleMax = 0
  AngleMin = 0
  Detach1 = false
  Detach2 = false
  Distance = 0
  Distance2 = 0
  EnableAngleMax = false
  EnableAngleMin = false
  EnableLengthMax = false
  EnableLengthMin = false
  JointType = 0 (Fixed)
  LengthMax = 0
  LengthMin = 0
  Placement1 = pos=(0,0,0) rot=(1,0,0;3.14159rad)
  Placement2 = pos=(2.714e-13,3.57e-14,3.5) rot=(0,0,1;0rad)
  Reference1 = -> Assembly [shaft.Edge3,shaft.Edge3]
  Reference2 = -> Assembly [second_layer.Face17,second_layer.Face17]
FEATURE [App::FeaturePython] Joint014  label="Fixed014"  # Assembly joint (typed FeaturePython)
  Activated = true
  AngleMax = 0
  AngleMin = 0
  Detach1 = false
  Detach2 = false
  Distance = 0
  Distance2 = 0
  EnableAngleMax = false
  EnableAngleMin = false
  EnableLengthMax = false
  EnableLengthMin = false
  JointType = 0 (Fixed)
  LengthMax = 0
  LengthMin = 0
  Offset2 = pos=(0,0,0) rot=(0,0,1;3.14159rad)
  Placement1 = pos=(0,0,10.2) rot=(0,0,1;0rad)
  Placement2 = pos=(0,0,44) rot=(0,0,1;3.14159rad)
  Reference1 = -> Assembly [M90S_ali001.Part__Feature123.Edge60,M90S_ali001.Part__Feature123.Edge60]
  Reference2 = -> Assembly [shaft.Edge54,shaft.Edge54]
FEATURE [App::Link] top_layer  label="017_top_layer001"
  LinkPlacement = pos=(-3.58e-14,-0.3,-15) rot=(0,0,1;4.71239rad)
  LinkedObject = -> Body010
  Placement = pos=(-3.58e-14,-0.3,-15) rot=(0,0,1;4.71239rad)
FEATURE [App::FeaturePython] Joint015  label="Fixed015"  # Assembly joint (typed FeaturePython)
  Activated = true
  AngleMax = 0
  AngleMin = 0
  Detach1 = false
  Detach2 = false
  Distance = 0
  Distance2 = 0
  EnableAngleMax = false
  EnableAngleMin = false
  EnableLengthMax = false
  EnableLengthMin = false
  JointType = 0 (Fixed)
  LengthMax = 0
  LengthMin = 0
  Placement1 = pos=(8.55,0,2.7) rot=(0,0,1;0rad)
  Placement2 = pos=(8.25,0,17.5) rot=(0,0,1;0rad)
  Reference1 = -> Assembly [M90S_ali001.Part__Feature123.Edge7,M90S_ali001.Part__Feature123.Edge7]
  Reference2 = -> Assembly [top_layer.Edge27,top_layer.Edge27]
FEATURE [App::Link] _3x3_8in_Screw007  label="018_#3x3/8in-Screw008"
  LinkPlacement = pos=(-1.95e-14,46.675,-6.25) rot=(0.57735,0.57735,0.57735;4.18879rad)
  LinkedObject = -> Screw001
  Placement = pos=(-1.95e-14,46.675,-6.25) rot=(0.57735,0.57735,0.57735;4.18879rad)
FEATURE [App::Link] _3x3_8in_Screw008  label="019_#3x3/8in-Screw009"
  LinkPlacement = pos=(46.975,-0.3,-6.25) rot=(0.707107,0,0.707107;3.14159rad)
  LinkedObject = -> Screw001
  Placement = pos=(46.975,-0.3,-6.25) rot=(0.707107,0,0.707107;3.14159rad)
FEATURE [App::Link] _2x1_4in_Screw  label="020_#2x1/4in-Screw001"
  LinkPlacement = pos=(-3.87e-14,-8.55,6.69239) rot=(0,0,1;4.71239rad)
  LinkedObject = -> Screw
  Placement = pos=(-3.87e-14,-8.55,6.69239) rot=(0,0,1;4.71239rad)
FEATURE [App::Link] _2x1_4in_Screw001  label="021_#2x1/4in-Screw002"
  LinkPlacement = pos=(-2.9e-14,19.45,6.69239) rot=(0,0,1;4.71239rad)
  LinkedObject = -> Screw
  Placement = pos=(-2.9e-14,19.45,6.69239) rot=(0,0,1;4.71239rad)
FEATURE [App::FeaturePython] Joint016  label="Fixed016"  # Assembly joint (typed FeaturePython)
  Activated = true
  AngleMax = 0
  AngleMin = 0
  Detach1 = false
  Detach2 = false
  Distance = 0
  Distance2 = 0
  EnableAngleMax = false
  EnableAngleMin = false
  EnableLengthMax = false
  EnableLengthMin = false
  JointType = 0 (Fixed)
  LengthMax = 0
  LengthMin = 0
  Placement1 = pos=(0,0,-1.49239) rot=(0,0,1;0rad)
  Placement2 = pos=(8.55,0,0) rot=(0,0,1;0rad)
  Reference1 = -> Assembly [_2x1_4in_Screw.Edge6,_2x1_4in_Screw.Edge6]
  Reference2 = -> Assembly [M90S_ali001.Part__Feature123.Edge5,M90S_ali001.Part__Feature123.Edge5]
FEATURE [App::FeaturePython] Joint017  label="Fixed017"  # Assembly joint (typed FeaturePython)
  Activated = true
  AngleMax = 0
  AngleMin = 0
  Detach1 = false
  Detach2 = false
  Distance = 0
  Distance2 = 0
  EnableAngleMax = false
  EnableAngleMin = false
  EnableLengthMax = false
  EnableLengthMin = false
  JointType = 0 (Fixed)
  LengthMax = 0
  LengthMin = 0
  Placement1 = pos=(0,0,-1.49239) rot=(0,0,1;0rad)
  Placement2 = pos=(-19.45,0,0) rot=(0,0,1;0rad)
  Reference1 = -> Assembly [_2x1_4in_Screw001.Edge6,_2x1_4in_Screw001.Edge6]
  Reference2 = -> Assembly [M90S_ali001.Part__Feature123.Edge66,M90S_ali001.Part__Feature123.Edge66]
FEATURE [App::FeaturePython] Joint018  label="Fixed018"  # Assembly joint (typed FeaturePython)
  Activated = true
  AngleMax = 0
  AngleMin = 0
  Detach1 = false
  Detach2 = false
  Distance = 0
  Distance2 = 0
  EnableAngleMax = false
  EnableAngleMin = false
  EnableLengthMax = false
  EnableLengthMin = false
  JointType = 0 (Fixed)
  LengthMax = 0
  LengthMin = 0
  Placement1 = pos=(-9e-16,0,-9.525) rot=(0,0,1;0rad)
  Placement2 = pos=(1e-16,37.45,8.75) rot=(-0.57735,-0.57735,-0.57735;2.0944rad)
  Reference1 = -> Assembly [_3x3_8in_Screw008.Edge1,_3x3_8in_Screw008.Edge1]
  Reference2 = -> Assembly [top_layer.Face20,top_layer.Face20]
FEATURE [App::FeaturePython] Joint019  label="Fixed019"  # Assembly joint (typed FeaturePython)
  Activated = true
  AngleMax = 0
  AngleMin = 0
  Detach1 = false
  Detach2 = false
  Distance = 0
  Distance2 = 0
  EnableAngleMax = false
  EnableAngleMin = false
  EnableLengthMax = false
  EnableLengthMin = false
  JointType = 0 (Fixed)
  LengthMax = 0
  LengthMin = 0
  Placement1 = pos=(0,0,-9.525) rot=(0,0,1;0rad)
  Placement2 = pos=(-37.45,0,8.75) rot=(0,-1,0;1.5708rad)
  Reference1 = -> Assembly [_3x3_8in_Screw007.Edge1,_3x3_8in_Screw007.Edge1]
  Reference2 = -> Assembly [top_layer.Face21,top_layer.Face21]
FEATURE [App::Link] dowel  label="022_dowel001"
  LinkPlacement = pos=(18.425,-31.913,-123.5) rot=(0,0,1;3.14159rad)
  LinkedObject = -> Body008
  Placement = pos=(18.425,-31.913,-123.5) rot=(0,0,1;3.14159rad)
FEATURE [App::Link] dowel001  label="023_dowel002"
  LinkPlacement = pos=(31.913,-18.425,-123.5) rot=(0,0,1;3.14159rad)
  LinkedObject = -> Body008
  Placement = pos=(31.913,-18.425,-123.5) rot=(0,0,1;3.14159rad)
FEATURE [App::Link] dowel002  label="024_dowel003"
  LinkPlacement = pos=(31.913,18.425,-123.5) rot=(0,0,1;3.14159rad)
  LinkedObject = -> Body008
  Placement = pos=(31.913,18.425,-123.5) rot=(0,0,1;3.14159rad)
FEATURE [App::Link] dowel003  label="025_dowel004"
  LinkPlacement = pos=(18.425,31.913,-123.5) rot=(0,0,1;3.14159rad)
  LinkedObject = -> Body008
  Placement = pos=(18.425,31.913,-123.5) rot=(0,0,1;3.14159rad)
FEATURE [App::Link] testube_layer  label="026_testube_layer001"
  LinkPlacement = pos=(1.42e-14,-1.61e-14,-123.5) rot=(0,0,1;3.14159rad)
  LinkedObject = -> Body006
  Placement = pos=(1.42e-14,-1.61e-14,-123.5) rot=(0,0,1;3.14159rad)
FEATURE [App::Link] sevo_legs  label="027_sevo_legs001"
  LinkPlacement = pos=(26.25,3.75,-123) rot=(0.707107,0,0.707107;3.14159rad)
  LinkedObject = -> Body007
  Placement = pos=(26.25,3.75,-123) rot=(0.707107,0,0.707107;3.14159rad)
FEATURE [App::Link] sevo_legs001  label="028_sevo_legs002"
  LinkPlacement = pos=(2.75,-3.75,-123) rot=(0,-1,0;1.5708rad)
  LinkedObject = -> Body007
  Placement = pos=(2.75,-3.75,-123) rot=(0,-1,0;1.5708rad)
FEATURE [App::Link] M90S_ali002  label="029_M90S_ali002"
  LinkPlacement = pos=(20.1,-0.122661,-91.5) rot=(0,0,1;0rad)
  LinkedObject = -> M90S_ali
  Placement = pos=(20.1,-0.122661,-91.5) rot=(0,0,1;0rad)
FEATURE [App::FeaturePython] Joint020  label="Fixed020"  # Assembly joint (typed FeaturePython)
  Activated = true
  AngleMax = 0
  AngleMin = 0
  Detach1 = false
  Detach2 = false
  Distance = 0
  Distance2 = 0
  EnableAngleMax = false
  EnableAngleMin = false
  EnableLengthMax = false
  EnableLengthMin = false
  JointType = 0 (Fixed)
  LengthMax = 0
  LengthMin = 0
  Placement1 = pos=(0,0,71) rot=(0,0,1;0rad)
  Placement2 = pos=(-18.425,31.913,7.5) rot=(0,0,1;0rad)
  Reference1 = -> Assembly [dowel.Edge3,dowel.Edge3]
  Reference2 = -> Assembly [ring_spacer.Edge16,ring_spacer.Edge16]
FEATURE [App::FeaturePython] Joint021  label="Fixed021"  # Assembly joint (typed FeaturePython)
  Activated = true
  AngleMax = 0
  AngleMin = 0
  Detach1 = false
  Detach2 = false
  Distance = 0
  Distance2 = 0
  EnableAngleMax = false
  EnableAngleMin = false
  EnableLengthMax = false
  EnableLengthMin = false
  JointType = 0 (Fixed)
  LengthMax = 0
  LengthMin = 0
  Placement1 = pos=(0,0,71) rot=(0,0,1;0rad)
  Placement2 = pos=(-31.913,18.425,7.5) rot=(0,0,1;0rad)
  Reference1 = -> Assembly [dowel001.Edge3,dowel001.Edge3]
  Reference2 = -> Assembly [ring_spacer.Edge15,ring_spacer.Edge15]
FEATURE [App::FeaturePython] Joint022  label="Fixed022"  # Assembly joint (typed FeaturePython)
  Activated = true
  AngleMax = 0
  AngleMin = 0
  Detach1 = false
  Detach2 = false
  Distance = 0
  Distance2 = 0
  EnableAngleMax = false
  EnableAngleMin = false
  EnableLengthMax = false
  EnableLengthMin = false
  JointType = 0 (Fixed)
  LengthMax = 0
  LengthMin = 0
  Placement1 = pos=(0,0,71) rot=(0,0,1;0rad)
  Placement2 = pos=(-31.913,-18.425,7.5) rot=(0,0,1;0rad)
  Reference1 = -> Assembly [dowel002.Edge3,dowel002.Edge3]
  Reference2 = -> Assembly [ring_spacer.Edge13,ring_spacer.Edge13]
FEATURE [App::FeaturePython] Joint023  label="Fixed023"  # Assembly joint (typed FeaturePython)
  Activated = true
  AngleMax = 0
  AngleMin = 0
  Detach1 = false
  Detach2 = false
  Distance = 0
  Distance2 = 0
  EnableAngleMax = false
  EnableAngleMin = false
  EnableLengthMax = false
  EnableLengthMin = false
  JointType = 0 (Fixed)
  LengthMax = 0
  LengthMin = 0
  Placement1 = pos=(0,0,71) rot=(0,0,1;0rad)
  Placement2 = pos=(-18.425,-31.913,7.5) rot=(0,0,1;0rad)
  Reference1 = -> Assembly [dowel003.Edge3,dowel003.Edge3]
  Reference2 = -> Assembly [ring_spacer.Edge14,ring_spacer.Edge14]
FEATURE [App::FeaturePython] Joint024  label="Fixed024"  # Assembly joint (typed FeaturePython)
  Activated = true
  AngleMax = 0
  AngleMin = 0
  Detach1 = false
  Detach2 = false
  Distance = 0
  Distance2 = 0
  EnableAngleMax = false
  EnableAngleMin = false
  EnableLengthMax = false
  EnableLengthMin = false
  JointType = 0 (Fixed)
  LengthMax = 0
  LengthMin = 0
  Placement2 = pos=(-18.425,-31.913,0) rot=(0,0,1;0rad)
  Reference1 = -> Assembly [dowel003.Edge2,dowel003.Edge2]
  Reference2 = -> Assembly [testube_layer.Edge13,testube_layer.Edge13]
FEATURE [App::FeaturePython] Joint025  label="Fixed025"  # Assembly joint (typed FeaturePython)
  Activated = true
  AngleMax = 0
  AngleMin = 0
  Detach1 = false
  Detach2 = false
  Distance = 0
  Distance2 = 0
  EnableAngleMax = false
  EnableAngleMin = false
  EnableLengthMax = false
  EnableLengthMin = false
  JointType = 0 (Fixed)
  LengthMax = 0
  LengthMin = 0
  Offset1 = pos=(0,30,0) rot=(0,0,1;0rad)
  Offset2 = pos=(0,0,-7) rot=(0,0,1;1.5708rad)
  Placement1 = pos=(0,3.75,-26.25) rot=(0.57735,0.57735,-0.57735;4.18879rad)
  Placement2 = pos=(0,0,0.5) rot=(0,0,1;1.5708rad)
  Reference1 = -> Assembly [sevo_legs.Face1,sevo_legs.Face1]
  Reference2 = -> Assembly [testube_layer.Edge4,testube_layer.Edge4]
FEATURE [App::FeaturePython] Joint026  label="Fixed026"  # Assembly joint (typed FeaturePython)
  Activated = true
  AngleMax = 0
  AngleMin = 0
  Detach1 = false
  Detach2 = false
  Distance = 0
  Distance2 = 0
  EnableAngleMax = false
  EnableAngleMin = false
  EnableLengthMax = false
  EnableLengthMin = false
  JointType = 0 (Fixed)
  LengthMax = 0
  LengthMin = 0
  Offset1 = pos=(0,1,0) rot=(0,0,1;0rad)
  Offset2 = pos=(0,0,-7) rot=(0,0,-1;1.5708rad)
  Placement1 = pos=(0,3.75,2.75) rot=(0.57735,0.57735,-0.57735;4.18879rad)
  Placement2 = pos=(0,0,0.5) rot=(0,0,-1;1.5708rad)
  Reference1 = -> Assembly [sevo_legs001.Face1,sevo_legs001.Face1]
  Reference2 = -> Assembly [testube_layer.Edge4,testube_layer.Edge4]
FEATURE [App::FeaturePython] Joint027  label="Fixed027"  # Assembly joint (typed FeaturePython)
  Activated = true
  AngleMax = 0
  AngleMin = 0
  Detach1 = false
  Detach2 = false
  Distance = 0
  Distance2 = 0
  EnableAngleMax = false
  EnableAngleMin = false
  EnableLengthMax = false
  EnableLengthMin = false
  JointType = 0 (Fixed)
  LengthMax = 0
  LengthMin = 0
  Offset2 = pos=(0,0,0) rot=(0,0,1;1.5708rad)
  Placement1 = pos=(8.55,0,0) rot=(0,0,1;0rad)
  Placement2 = pos=(31.5,3.87266,2.4) rot=(-0.707107,0,-0.707107;3.14159rad)
  Reference1 = -> Assembly [M90S_ali002.Part__Feature123.Edge5,M90S_ali002.Part__Feature123.Edge5]
  Reference2 = -> Assembly [sevo_legs.Edge41,sevo_legs.Edge41]
FEATURE [App::Link] _2x1_4in_Screw002  label="030_#2x1/4in-Screw003"
  LinkPlacement = pos=(28.65,-0.122661,-87.3076) rot=(0,0,1;0rad)
  LinkedObject = -> Screw
  Placement = pos=(28.65,-0.122661,-87.3076) rot=(0,0,1;0rad)
FEATURE [App::Link] _2x1_4in_Screw003  label="031_#2x1/4in-Screw004"
  LinkPlacement = pos=(0.65,-0.122661,-87.3076) rot=(0,0,1;0rad)
  LinkedObject = -> Screw
  Placement = pos=(0.65,-0.122661,-87.3076) rot=(0,0,1;0rad)
FEATURE [App::FeaturePython] Joint028  label="Fixed028"  # Assembly joint (typed FeaturePython)
  Activated = true
  AngleMax = 0
  AngleMin = 0
  Detach1 = false
  Detach2 = false
  Distance = 0
  Distance2 = 0
  EnableAngleMax = false
  EnableAngleMin = false
  EnableLengthMax = false
  EnableLengthMin = false
  JointType = 0 (Fixed)
  LengthMax = 0
  LengthMin = 0
  Placement1 = pos=(0,0,-1.49239) rot=(0,0,1;0rad)
  Placement2 = pos=(8.55,0,2.7) rot=(0,0,1;0rad)
  Reference1 = -> Assembly [_2x1_4in_Screw002.Edge6,_2x1_4in_Screw002.Edge6]
  Reference2 = -> Assembly [M90S_ali002.Part__Feature123.Edge7,M90S_ali002.Part__Feature123.Edge7]
FEATURE [App::FeaturePython] Joint029  label="Fixed029"  # Assembly joint (typed FeaturePython)
  Activated = true
  AngleMax = 0
  AngleMin = 0
  Detach1 = false
  Detach2 = false
  Distance = 0
  Distance2 = 0
  EnableAngleMax = false
  EnableAngleMin = false
  EnableLengthMax = false
  EnableLengthMin = false
  JointType = 0 (Fixed)
  LengthMax = 0
  LengthMin = 0
  Placement1 = pos=(0,0,-1.49239) rot=(0,0,1;0rad)
  Placement2 = pos=(-19.45,0,2.7) rot=(0,0,1;0rad)
  Reference1 = -> Assembly [_2x1_4in_Screw003.Edge6,_2x1_4in_Screw003.Edge6]
  Reference2 = -> Assembly [M90S_ali002.Part__Feature123.Edge75,M90S_ali002.Part__Feature123.Edge75]
FEATURE [App::Link] Cut  label="032_Cut"
  LinkPlacement = pos=(20.1,-8.12266,-78.3) rot=(0,0.707107,0.707107;3.14159rad)
  LinkedObject = -> <external Slide Mount.FCStd>#Cut
  Placement = pos=(20.1,-8.12266,-78.3) rot=(0,0.707107,0.707107;3.14159rad)
FEATURE [App::FeaturePython] Joint030  label="Fixed030"  # Assembly joint (typed FeaturePython)
  Activated = true
  AngleMax = 0
  AngleMin = 0
  Detach1 = false
  Detach2 = false
  Distance = 0
  Distance2 = 0
  EnableAngleMax = false
  EnableAngleMin = false
  EnableLengthMax = false
  EnableLengthMin = false
  JointType = 0 (Fixed)
  LengthMax = 0
  LengthMin = 0
  Offset2 = pos=(0,0,4) rot=(0,0,1;3.14159rad)
  Placement1 = pos=(0,1,8) rot=(1,0,0;1.5708rad)
  Placement2 = pos=(0,0,14.2) rot=(0,0,1;3.14159rad)
  Reference1 = -> Assembly [Cut.Edge18,Cut.Edge18]
  Reference2 = -> Assembly [M90S_ali002.Part__Feature123.Edge60,M90S_ali002.Part__Feature123.Edge60]
FEATURE [Sketcher::SketchObject] Sketch027
  ArcFitTolerance = 1e-06
  AttachmentSupport = -> [XY_Plane018]
  FullyConstrained = true
  MakeInternals = false
  MapMode = 5
  sketch-geometry (5):
    g0: LineSegment StartX=-5 StartY=-7.5 StartZ=0 EndX=5 EndY=-7.5 EndZ=0
    g1: LineSegment StartX=5 StartY=-7.5 StartZ=0 EndX=5 EndY=7.5 EndZ=0
    g2: LineSegment StartX=5 StartY=7.5 StartZ=0 EndX=-5 EndY=7.5 EndZ=0
    g3: LineSegment StartX=-5 StartY=7.5 StartZ=0 EndX=-5 EndY=-7.5 EndZ=0
    g4: GeomPoint [constr] X=0 Y=0 Z=0
  constraints (12):
    c: Coincident(g0,g1)
    c: Coincident(g1,g2)
    c: Coincident(g2,g3)
    c: Coincident(g3,g0)
    c: Horizontal(g0)
    c: Horizontal(g2)
    c: Vertical(g1)
    c: Vertical(g3)
    c: Symmetric(g2,g0,g4)
    c: Distance(g1,g3) = 10
    c: Distance(g0,g2) = 15
    c: Coincident(g4,g-1)
FEATURE [PartDesign::Pad] Pad011
  Direction = (0,0,1)
  Length = 1
  Length2 = 10
  Profile = -> Sketch027
  ReferenceAxis = -> Sketch027 [N_Axis]
  Refine = true
  Suppressed = false
  Type = 0
FEATURE [PartDesign::Body] Body012  label="3m-foam"
  AllowCompound = false
  Group = -> [Sketch027,Pad011]
  Origin = -> Origin018
  Tip = -> Pad011
FEATURE [Sketcher::SketchObject] Sketch028
  ArcFitTolerance = 1e-06
  AttachmentSupport = -> [XY_Plane019]
  FullyConstrained = true
  MakeInternals = false
  MapMode = 5
  sketch-geometry (5):
    g0: LineSegment StartX=-5 StartY=-7.5 StartZ=0 EndX=5 EndY=-7.5 EndZ=0
    g1: LineSegment StartX=5 StartY=-7.5 StartZ=0 EndX=5 EndY=7.5 EndZ=0
    g2: LineSegment StartX=5 StartY=7.5 StartZ=0 EndX=-5 EndY=7.5 EndZ=0
    g3: LineSegment StartX=-5 StartY=7.5 StartZ=0 EndX=-5 EndY=-7.5 EndZ=0
    g4: GeomPoint [constr] X=0 Y=0 Z=0
  constraints (12):
    c: Coincident(g0,g1)
    c: Coincident(g1,g2)
    c: Coincident(g2,g3)
    c: Coincident(g3,g0)
    c: Horizontal(g0)
    c: Horizontal(g2)
    c: Vertical(g1)
    c: Vertical(g3)
    c: Symmetric(g2,g0,g4)
    c: Distance(g1,g3) = 10
    c: Distance(g0,g2) = 15
    c: Coincident(g4,g-1)
FEATURE [PartDesign::Pad] Pad012
  Direction = (0,0,1)
  Length = 0.2
  Length2 = 10
  Profile = -> Sketch028
  ReferenceAxis = -> Sketch028 [N_Axis]
  Refine = true
  Suppressed = false
  Type = 0
FEATURE [PartDesign::Body] Body013  label="3m-sticker"
  AllowCompound = false
  Group = -> [Sketch028,Pad012]
  Origin = -> Origin019
  Tip = -> Pad012
FEATURE [App::FeaturePython] Joint033  label="Fixed033"  # Assembly joint (typed FeaturePython)
  Activated = true
  AngleMax = 0
  AngleMin = 0
  Detach1 = false
  Detach2 = false
  Distance = 0
  Distance2 = 0
  EnableAngleMax = false
  EnableAngleMin = false
  EnableLengthMax = false
  EnableLengthMin = false
  JointType = 0 (Fixed)
  LengthMax = 0
  LengthMin = 0
FEATURE [App::Link] _m_sticker  label="033_3m-sticker001"
  LinkPlacement = pos=(3.30094,-0.122661,-78.0842) rot=(0.701112,-0.701112,0.129943;3.40003rad)
  LinkedObject = -> Body013
  Placement = pos=(3.30094,-0.122661,-78.0842) rot=(0.701112,-0.701112,0.129943;3.40003rad)
FEATURE [App::Link] _m_foam  label="034_3m-foam001"
  LinkPlacement = pos=(3.37262,-0.122661,-78.2709) rot=(0.701112,-0.701112,0.129943;3.40003rad)
  LinkedObject = -> Body012
  Placement = pos=(3.37262,-0.122661,-78.2709) rot=(0.701112,-0.701112,0.129943;3.40003rad)
FEATURE [App::FeaturePython] Joint034  label="Fixed034"  # Assembly joint (typed FeaturePython)
  Activated = true
  AngleMax = 0
  AngleMin = 0
  Detach1 = false
  Detach2 = false
  Distance = 0
  Distance2 = 0
  EnableAngleMax = false
  EnableAngleMin = false
  EnableLengthMax = false
  EnableLengthMin = false
  JointType = 0 (Fixed)
  LengthMax = 0
  LengthMin = 0
  Offset2 = pos=(0,0,0) rot=(0,0,1;1.5708rad)
  Placement1 = pos=(0,0,1) rot=(0,0,1;0rad)
  Placement2 = pos=(16.369,-0.904496,8) rot=(-0.492841,0.717088,0.492841;1.89739rad)
  Reference1 = -> Assembly [_m_foam.Face6,_m_foam.Face6]
  Reference2 = -> Assembly [Cut.Face2,Cut.Face2]
FEATURE [App::FeaturePython] Joint035  label="Fixed035"  # Assembly joint (typed FeaturePython)
  Activated = true
  AngleMax = 0
  AngleMin = 0
  Detach1 = false
  Detach2 = false
  Distance = 0
  Distance2 = 0
  EnableAngleMax = false
  EnableAngleMin = false
  EnableLengthMax = false
  EnableLengthMin = false
  JointType = 0 (Fixed)
  LengthMax = 0
  LengthMin = 0
  Placement1 = pos=(0,-3.6e-15,0.2) rot=(0,0,1;0rad)
  Reference1 = -> Assembly [_m_sticker.Face6,_m_sticker.Face6]
  Reference2 = -> Assembly [_m_foam.Face5,_m_foam.Face5]
FEATURE [App::Link] _m_sticker001  label="035_3m-sticker002"
  LinkPlacement = pos=(1.59e-14,-1.18e-14,-123.7) rot=(0,0,1;4.71239rad)
  LinkedObject = -> Body013
  Placement = pos=(1.59e-14,-1.18e-14,-123.7) rot=(0,0,1;4.71239rad)
FEATURE [App::Link] _m_foam001  label="036_3m-foam002"
  LinkPlacement = pos=(1.59e-14,-1.16e-14,-124.7) rot=(0,0,1;4.71239rad)
  LinkedObject = -> Body012
  Placement = pos=(1.59e-14,-1.16e-14,-124.7) rot=(0,0,1;4.71239rad)
FEATURE [App::Link] Cap  label="037_Cap"
  LinkPlacement = pos=(1.58e-14,-1.17e-14,-228.7) rot=(0,0,1;1.5708rad)
  LinkedObject = -> <external Parametric Screw Top Container.FCStd>#Body001
  Placement = pos=(1.58e-14,-1.17e-14,-228.7) rot=(0,0,1;1.5708rad)
FEATURE [App::Link] Base  label="038_Base"
  LinkPlacement = pos=(1.56e-14,-1.17e-14,-228.7) rot=(0,0,1;1.5708rad)
  LinkedObject = -> <external Parametric Screw Top Container.FCStd>#Body
  Placement = pos=(1.56e-14,-1.17e-14,-228.7) rot=(0,0,1;1.5708rad)
FEATURE [App::FeaturePython] Joint036  label="Fixed036"  # Assembly joint (typed FeaturePython)
  Activated = true
  AngleMax = 0
  AngleMin = 0
  Detach1 = false
  Detach2 = false
  Distance = 0
  Distance2 = 0
  EnableAngleMax = false
  EnableAngleMin = false
  EnableLengthMax = false
  EnableLengthMin = false
  JointType = 0 (Fixed)
  LengthMax = 0
  LengthMin = 0
  Offset1 = pos=(0,20,0) rot=(0,0,1;0rad)
  Offset2 = pos=(0,0,0) rot=(0,0,1;1.5708rad)
  Placement1 = pos=(1e-16,20,0.2) rot=(0,0,1;0rad)
  Placement2 = pos=(-20,0,0) rot=(0,0,1;1.5708rad)
  Reference1 = -> Assembly [_m_sticker001.Face6,_m_sticker001.Face6]
  Reference2 = -> Assembly [testube_layer.Face4,testube_layer.Edge4]
FEATURE [App::FeaturePython] Joint037  label="Fixed037"  # Assembly joint (typed FeaturePython)
  Activated = true
  AngleMax = 0
  AngleMin = 0
  Detach1 = false
  Detach2 = false
  Distance = 0
  Distance2 = 0
  EnableAngleMax = false
  EnableAngleMin = false
  EnableLengthMax = false
  EnableLengthMin = false
  JointType = 0 (Fixed)
  LengthMax = 0
  LengthMin = 0
  Placement1 = pos=(0,-3e-16,1) rot=(0,0,1;0rad)
  Placement2 = pos=(1e-16,-3e-16,0) rot=(0,0,1;0rad)
  Reference1 = -> Assembly [_m_foam001.Face6,_m_foam001.Face6]
  Reference2 = -> Assembly [_m_sticker001.Face5,_m_sticker001.Face5]
FEATURE [App::FeaturePython] Joint038  label="Fixed038"  # Assembly joint (typed FeaturePython)
  Activated = true
  AngleMax = 0
  AngleMin = 0
  Detach1 = false
  Detach2 = false
  Distance = 0
  Distance2 = 0
  EnableAngleMax = false
  EnableAngleMin = false
  EnableLengthMax = false
  EnableLengthMin = false
  JointType = 0 (Fixed)
  LengthMax = 0
  LengthMin = 0
  Placement1 = pos=(0,2.31e-14,104) rot=(0,0,-1;3.14159rad)
  Placement2 = pos=(0,-3e-16,0) rot=(0,0,1;0rad)
  Reference1 = -> Assembly [Cap.Face68,Cap.Edge1]
  Reference2 = -> Assembly [_m_foam001.Face5,_m_foam001.Face5]
FEATURE [App::FeaturePython] Joint039  label="Fixed039"  # Assembly joint (typed FeaturePython)
  Activated = true
  AngleMax = 0
  AngleMin = 0
  Detach1 = false
  Detach2 = false
  Distance = 0
  Distance2 = 0
  EnableAngleMax = false
  EnableAngleMin = false
  EnableLengthMax = false
  EnableLengthMin = false
  JointType = 0 (Fixed)
  LengthMax = 0
  LengthMin = 0
  Placement1 = pos=(0,0,102) rot=(0,0,1;0rad)
  Placement2 = pos=(0,2.27e-14,102) rot=(1,0,0;3.14159rad)
  Reference1 = -> Assembly [Base.Edge179,Base.Edge179]
  Reference2 = -> Assembly [Cap.Face1,Cap.Edge1]
FEATURE [App::Link] testube  label="039_testube"
  LinkPlacement = pos=(-28.1323,-55.5476,-210) rot=(0,0,1;3.99839rad)
  LinkedObject = -> <external testube.FCStd>#Body
  Placement = pos=(-28.1323,-55.5476,-210) rot=(0,0,1;3.99839rad)
FEATURE [App::Link] testube001  label="040_testube001"
  LinkPlacement = pos=(-41.8321,-39.7371,-210) rot=(0,0,1;3.71279rad)
  LinkedObject = -> <external testube.FCStd>#Body
  Placement = pos=(-41.8321,-39.7371,-210) rot=(0,0,1;3.71279rad)
FEATURE [App::Link] testube002  label="041_testube002"
  LinkPlacement = pos=(-50.5227,-20.7073,-210) rot=(0,0,1;3.42719rad)
  LinkedObject = -> <external testube.FCStd>#Body
  Placement = pos=(-50.5227,-20.7073,-210) rot=(0,0,1;3.42719rad)
FEATURE [App::Link] testube003  label="042_testube003"
  LinkPlacement = pos=(-53.5,-2.25e-14,-210) rot=(0,0,1;3.14159rad)
  LinkedObject = -> <external testube.FCStd>#Body
  Placement = pos=(-53.5,-2.25e-14,-210) rot=(0,0,1;3.14159rad)
FEATURE [App::Link] testube004  label="043_testube004"
  LinkPlacement = pos=(-50.5227,20.7073,-210) rot=(0,0,1;2.85599rad)
  LinkedObject = -> <external testube.FCStd>#Body
  Placement = pos=(-50.5227,20.7073,-210) rot=(0,0,1;2.85599rad)
FEATURE [App::Link] testube005  label="044_testube005"
  LinkPlacement = pos=(-41.8321,39.7371,-210) rot=(0,0,1;2.57039rad)
  LinkedObject = -> <external testube.FCStd>#Body
  Placement = pos=(-41.8321,39.7371,-210) rot=(0,0,1;2.57039rad)
FEATURE [App::Link] testube006  label="045_testube006"
  LinkPlacement = pos=(-28.1323,55.5476,-210) rot=(0,0,1;2.28479rad)
  LinkedObject = -> <external testube.FCStd>#Body
  Placement = pos=(-28.1323,55.5476,-210) rot=(0,0,1;2.28479rad)
FEATURE [App::FeaturePython] Joint040  label="Fixed040"  # Assembly joint (typed FeaturePython)
  Activated = true
  AngleMax = 0
  AngleMin = 0
  Detach1 = false
  Detach2 = false
  Distance = 0
  Distance2 = 0
  EnableAngleMax = false
  EnableAngleMin = false
  EnableLengthMax = false
  EnableLengthMin = false
  JointType = 0 (Fixed)
  LengthMax = 0
  LengthMin = 0
  Placement1 = pos=(28.1323,55.5476,7.5) rot=(0,0,1;0.856798rad)
  Placement2 = pos=(7.1e-15,2.49e-14,94) rot=(1,0,0;3.14159rad)
  Reference1 = -> Assembly [testube_layer.Edge49,testube_layer.Edge49]
  Reference2 = -> Assembly [testube.Edge11,testube.Edge11]
FEATURE [App::FeaturePython] Joint041  label="Fixed041"  # Assembly joint (typed FeaturePython)
  Activated = true
  AngleMax = 0
  AngleMin = 0
  Detach1 = false
  Detach2 = false
  Distance = 0
  Distance2 = 0
  EnableAngleMax = false
  EnableAngleMin = false
  EnableLengthMax = false
  EnableLengthMin = false
  JointType = 0 (Fixed)
  LengthMax = 0
  LengthMin = 0
  Placement1 = pos=(0,2.49e-14,94) rot=(1,0,0;3.14159rad)
  Placement2 = pos=(41.8321,39.7371,7.5) rot=(0,0,1;0.571199rad)
  Reference1 = -> Assembly [testube001.Edge11,testube001.Edge11]
  Reference2 = -> Assembly [testube_layer.Edge50,testube_layer.Edge50]
FEATURE [App::FeaturePython] Joint042  label="Fixed042"  # Assembly joint (typed FeaturePython)
  Activated = true
  AngleMax = 0
  AngleMin = 0
  Detach1 = false
  Detach2 = false
  Distance = 0
  Distance2 = 0
  EnableAngleMax = false
  EnableAngleMin = false
  EnableLengthMax = false
  EnableLengthMin = false
  JointType = 0 (Fixed)
  LengthMax = 0
  LengthMin = 0
  Placement1 = pos=(50.5227,20.7073,7.5) rot=(0,0,1;0.285599rad)
  Placement2 = pos=(7.1e-15,2.49e-14,94) rot=(1,0,0;3.14159rad)
  Reference1 = -> Assembly [testube_layer.Edge48,testube_layer.Edge48]
  Reference2 = -> Assembly [testube002.Edge11,testube002.Edge11]
FEATURE [App::FeaturePython] Joint043  label="Fixed043"  # Assembly joint (typed FeaturePython)
  Activated = true
  AngleMax = 0
  AngleMin = 0
  Detach1 = false
  Detach2 = false
  Distance = 0
  Distance2 = 0
  EnableAngleMax = false
  EnableAngleMin = false
  EnableLengthMax = false
  EnableLengthMin = false
  JointType = 0 (Fixed)
  LengthMax = 0
  LengthMin = 0
  Placement1 = pos=(0,2.09e-14,94) rot=(1,0,0;3.14159rad)
  Placement2 = pos=(53.5,0,7.5) rot=(0,0,1;0rad)
  Reference1 = -> Assembly [testube003.Edge11,testube003.Edge11]
  Reference2 = -> Assembly [testube_layer.Edge47,testube_layer.Edge47]
FEATURE [App::FeaturePython] Joint044  label="Fixed044"  # Assembly joint (typed FeaturePython)
  Activated = true
  AngleMax = 0
  AngleMin = 0
  Detach1 = false
  Detach2 = false
  Distance = 0
  Distance2 = 0
  EnableAngleMax = false
  EnableAngleMin = false
  EnableLengthMax = false
  EnableLengthMin = false
  JointType = 0 (Fixed)
  LengthMax = 0
  LengthMin = 0
  Placement1 = pos=(50.5227,-20.7073,7.5) rot=(0,0,-1;0.285599rad)
  Placement2 = pos=(7.1e-15,2.31e-14,94) rot=(1,0,0;3.14159rad)
  Reference1 = -> Assembly [testube_layer.Edge36,testube_layer.Edge36]
  Reference2 = -> Assembly [testube004.Edge11,testube004.Edge11]
FEATURE [App::FeaturePython] Joint045  label="Fixed045"  # Assembly joint (typed FeaturePython)
  Activated = true
  AngleMax = 0
  AngleMin = 0
  Detach1 = false
  Detach2 = false
  Distance = 0
  Distance2 = 0
  EnableAngleMax = false
  EnableAngleMin = false
  EnableLengthMax = false
  EnableLengthMin = false
  JointType = 0 (Fixed)
  LengthMax = 0
  LengthMin = 0
  Placement1 = pos=(7.1e-15,2.13e-14,94) rot=(1,0,0;3.14159rad)
  Placement2 = pos=(41.8321,-39.7371,7.5) rot=(0,0,-1;0.571199rad)
  Reference1 = -> Assembly [testube005.Edge11,testube005.Edge11]
  Reference2 = -> Assembly [testube_layer.Edge35,testube_layer.Edge35]
FEATURE [App::FeaturePython] Joint046  label="Fixed046"  # Assembly joint (typed FeaturePython)
  Activated = true
  AngleMax = 0
  AngleMin = 0
  Detach1 = false
  Detach2 = false
  Distance = 0
  Distance2 = 0
  EnableAngleMax = false
  EnableAngleMin = false
  EnableLengthMax = false
  EnableLengthMin = false
  JointType = 0 (Fixed)
  LengthMax = 0
  LengthMin = 0
  Placement1 = pos=(28.1323,-55.5476,7.5) rot=(0,0,-1;0.856798rad)
  Placement2 = pos=(0,2.49e-14,94) rot=(1,0,0;3.14159rad)
  Reference1 = -> Assembly [testube_layer.Edge34,testube_layer.Edge34]
  Reference2 = -> Assembly [testube006.Edge11,testube006.Edge11]
FEATURE [App::Link] Body014  label="046_Body014"
  LinkPlacement = pos=(-53.0325,-0.122661,-99.7086) rot=(-0.182236,0,0.983255;3.14159rad)
  LinkedObject = -> <external Slide.FCStd>#Body
  Placement = pos=(-53.0325,-0.122661,-99.7086) rot=(-0.182236,0,0.983255;3.14159rad)
FEATURE [App::FeaturePython] Joint047  label="Fixed047"  # Assembly joint (typed FeaturePython)
  Activated = true
  AngleMax = 0
  AngleMin = 0
  Detach1 = false
  Detach2 = false
  Distance = 0
  Distance2 = 0
  EnableAngleMax = false
  EnableAngleMin = false
  EnableLengthMax = false
  EnableLengthMin = false
  JointType = 0 (Fixed)
  LengthMax = 0
  LengthMin = 0
  Offset1 = pos=(0,10,0) rot=(0,0,1;0rad)
  Offset2 = pos=(0,0,0) rot=(0,0,1;1.5708rad)
  Placement1 = pos=(0,10,-3e-16) rot=(0,0,1;0rad)
  Placement2 = pos=(-50.3413,-4.8e-15,-1.42e-14) rot=(0,0,1;1.5708rad)
  Reference1 = -> Assembly [_m_sticker.Face5,_m_sticker.Face5]
  Reference2 = -> Assembly [Body014.Face5,Body014.Face5]
FEATURE [Part::Feature] Part__Feature177  label="Default"
  shape: bbox 0.65 x 18.8 x 0.65 mm, 14 faces (baked)
FEATURE [App::Part] Pin
  Group = -> [Part__Feature177]
  Origin = -> Origin024
FEATURE [Part::Feature] Part__Feature178  label="Header"
  shape: bbox 2.5 x 14.1 x 2.5 mm, 42 faces (baked)
FEATURE [App::Part] Socket
  Group = -> [Part__Feature178]
  Origin = -> Origin025
FEATURE [Part::Feature] Part__Feature179  label="BreadBoard"
  Placement = pos=(197,-2.75e-14,-124) rot=(1,0,0;1.5708rad)
  shape: bbox 83.8 x 55.5 x 8.01 mm, 3672 faces, 3 solids (baked)
FEATURE [Part::Feature] Part__Feature  label="+++ ESP8266 NodeMCU Board +++"
  shape: bbox 25.71 x 12.52 x 48.5 mm, 4079 faces, 35 solids (baked)
FEATURE [App::DocumentObjectGroup] Group003  label="STL-parts"
  Group = -> [_472_v5,_x7_Male_Pin_Header,M90S_ali,Pin,Socket,Part__Feature179,Part__Feature]
FEATURE [Sketcher::SketchObject] Sketch029
  ArcFitTolerance = 1e-06
  AttachmentSupport = -> [XZ_Plane027]
  FullyConstrained = true
  MakeInternals = false
  MapMode = 5
  Placement = pos=(0,0,0) rot=(1,0,0;1.5708rad)
  sketch-geometry (7):
    g0-g3: Circle [constr] x4 (B-spline internal-alignment scaffolding for g4; pole/knot coordinates omitted)
    g4: BSplineCurve PolesCount=4 KnotsCount=2 Degree=3 IsPeriodic=0
    g5: GeomPoint [constr] X=0 Y=60 Z=0
    g6: GeomPoint [constr] X=60 Y=0 Z=0
  constraints (14):
    c: Weight(g0) = 1
    c: Equal(g0,g1)
    c: Equal(g0,g2)
    c: Equal(g0,g3)
    c: InternalAlignment(g0-g3 -> g4) x4
    c: InternalAlignment(g5,g4)
    c: InternalAlignment(g6,g4)
    c: PointOnObject(g0,g-2)
    c: PointOnObject(g2,g-1)
    c: DistanceX(g-1,g4) = 60
    c: Symmetric(g-1,g4,g2)
    c: Vertical(g1,g2)
    c: DistanceY(g-1,g4) = 60
    c: Horizontal(g1,g4)
FEATURE [PartDesign::Plane] DatumPlane007
  AttachmentOffset = pos=(0,0,60) rot=(0,0,1;0rad)
  AttachmentSupport = -> [YZ_Plane027]
  Length = 63.084
  MapMode = 5
  Placement = pos=(60,0,0) rot=(0.57735,0.57735,0.57735;2.0944rad)
  ResizeMode = 0
  Width = 98.6796
FEATURE [Sketcher::SketchObject] Sketch030
  ArcFitTolerance = 1e-06
  AttachmentSupport = -> [DatumPlane007]
  FullyConstrained = true
  MakeInternals = false
  MapMode = 5
  Placement = pos=(60,0,0) rot=(0.57735,0.57735,0.57735;2.0944rad)
  sketch-geometry (1):
    g0: Circle CenterX=0 CenterY=0 CenterZ=0 NormalX=0 NormalY=0 NormalZ=1 AngleXU=0 Radius=0.6
  constraints (2):
    c: Coincident(g0,g-1)
    c: Diameter(g0) = 1.2
FEATURE [PartDesign::AdditivePipe] AdditivePipe
  AuxilleryCurvelinear = true
  AuxillerySpineTangent = false
  Binormal = (0,0,0)
  Mode = 0
  Placement = pos=(60,0,0) rot=(0.57735,0.57735,0.57735;2.0944rad)
  Profile = -> Sketch030
  Refine = true
  Spine = -> Sketch029 [Edge1]
  SpineTangent = false
  Suppressed = false
  Transformation = 0
  Transition = 0
FEATURE [PartDesign::Body] Body016  label="wire-red"
  AllowCompound = false
  Group = -> [Sketch029,DatumPlane007,Sketch030,AdditivePipe]
  Origin = -> Origin027
  Placement = pos=(0,-14,0) rot=(0,0,1;0rad)
  Tip = -> AdditivePipe
FEATURE [PartDesign::Plane] DatumPlane008
  AttachmentOffset = pos=(0,0,60) rot=(0,0,1;0rad)
  AttachmentSupport = -> [YZ_Plane028]
  Length = 63.084
  MapMode = 5
  Placement = pos=(60,0,0) rot=(0.57735,0.57735,0.57735;2.0944rad)
  ResizeMode = 0
  Width = 98.6796
FEATURE [Sketcher::SketchObject] Sketch031
  ArcFitTolerance = 1e-06
  AttachmentSupport = -> [XZ_Plane028]
  FullyConstrained = true
  MakeInternals = false
  MapMode = 5
  Placement = pos=(0,0,0) rot=(1,0,0;1.5708rad)
  sketch-geometry (7):
    g0-g3: Circle [constr] x4 (B-spline internal-alignment scaffolding for g4; pole/knot coordinates omitted)
    g4: BSplineCurve PolesCount=4 KnotsCount=2 Degree=3 IsPeriodic=0
    g5: GeomPoint [constr] X=0 Y=60 Z=0
    g6: GeomPoint [constr] X=60 Y=0 Z=0
  constraints (14):
    c: Weight(g0) = 1
    c: Equal(g0,g1)
    c: Equal(g0,g2)
    c: Equal(g0,g3)
    c: InternalAlignment(g0-g3 -> g4) x4
    c: InternalAlignment(g5,g4)
    c: InternalAlignment(g6,g4)
    c: PointOnObject(g0,g-2)
    c: PointOnObject(g2,g-1)
    c: DistanceX(g-1,g4) = 60
    c: Symmetric(g-1,g4,g2)
    c: Vertical(g1,g2)
    c: DistanceY(g-1,g4) = 60
    c: Horizontal(g1,g4)
FEATURE [Sketcher::SketchObject] Sketch032
  ArcFitTolerance = 1e-06
  AttachmentSupport = -> [DatumPlane008]
  FullyConstrained = true
  MakeInternals = false
  MapMode = 5
  Placement = pos=(60,0,0) rot=(0.57735,0.57735,0.57735;2.0944rad)
  sketch-geometry (1):
    g0: Circle CenterX=0 CenterY=0 CenterZ=0 NormalX=0 NormalY=0 NormalZ=1 AngleXU=0 Radius=0.6
  constraints (2):
    c: Coincident(g0,g-1)
    c: Diameter(g0) = 1.2
FEATURE [PartDesign::AdditivePipe] AdditivePipe001
  AuxilleryCurvelinear = true
  AuxillerySpineTangent = false
  Binormal = (0,0,0)
  Mode = 0
  Placement = pos=(60,0,0) rot=(0.57735,0.57735,0.57735;2.0944rad)
  Profile = -> Sketch032
  Refine = true
  Spine = -> Sketch031 [Edge1]
  SpineTangent = false
  Suppressed = false
  Transformation = 0
  Transition = 0
FEATURE [PartDesign::Body] Body017  label="wire-brown"
  AllowCompound = false
  Group = -> [Sketch031,DatumPlane008,Sketch032,AdditivePipe001]
  Origin = -> Origin028
  Tip = -> AdditivePipe001
FEATURE [PartDesign::Plane] DatumPlane009
  AttachmentOffset = pos=(0,0,60) rot=(0,0,1;0rad)
  AttachmentSupport = -> [YZ_Plane029]
  Length = 63.084
  MapMode = 5
  Placement = pos=(60,0,0) rot=(0.57735,0.57735,0.57735;2.0944rad)
  ResizeMode = 0
  Width = 98.6796
FEATURE [Sketcher::SketchObject] Sketch033
  ArcFitTolerance = 1e-06
  AttachmentSupport = -> [XZ_Plane029]
  FullyConstrained = true
  MakeInternals = false
  MapMode = 5
  Placement = pos=(0,0,0) rot=(1,0,0;1.5708rad)
  sketch-geometry (7):
    g0-g3: Circle [constr] x4 (B-spline internal-alignment scaffolding for g4; pole/knot coordinates omitted)
    g4: BSplineCurve PolesCount=4 KnotsCount=2 Degree=3 IsPeriodic=0
    g5: GeomPoint [constr] X=0 Y=60 Z=0
    g6: GeomPoint [constr] X=60 Y=0 Z=0
  constraints (14):
    c: Weight(g0) = 1
    c: Equal(g0,g1)
    c: Equal(g0,g2)
    c: Equal(g0,g3)
    c: InternalAlignment(g0-g3 -> g4) x4
    c: InternalAlignment(g5,g4)
    c: InternalAlignment(g6,g4)
    c: PointOnObject(g0,g-2)
    c: PointOnObject(g2,g-1)
    c: DistanceX(g-1,g4) = 60
    c: Symmetric(g-1,g4,g2)
    c: Vertical(g1,g2)
    c: DistanceY(g-1,g4) = 60
    c: Horizontal(g1,g4)
FEATURE [Sketcher::SketchObject] Sketch034
  ArcFitTolerance = 1e-06
  AttachmentSupport = -> [DatumPlane009]
  FullyConstrained = true
  MakeInternals = false
  MapMode = 5
  Placement = pos=(60,0,0) rot=(0.57735,0.57735,0.57735;2.0944rad)
  sketch-geometry (1):
    g0: Circle CenterX=0 CenterY=0 CenterZ=0 NormalX=0 NormalY=0 NormalZ=1 AngleXU=0 Radius=0.6
  constraints (2):
    c: Coincident(g0,g-1)
    c: Diameter(g0) = 1.2
FEATURE [PartDesign::AdditivePipe] AdditivePipe002
  AuxilleryCurvelinear = true
  AuxillerySpineTangent = false
  Binormal = (0,0,0)
  Mode = 0
  Placement = pos=(60,0,0) rot=(0.57735,0.57735,0.57735;2.0944rad)
  Profile = -> Sketch034
  Refine = true
  Spine = -> Sketch033 [Edge1]
  SpineTangent = false
  Suppressed = false
  Transformation = 0
  Transition = 0
FEATURE [PartDesign::Body] Body018  label="wire-orange"
  AllowCompound = false
  Group = -> [Sketch033,DatumPlane009,Sketch034,AdditivePipe002]
  Origin = -> Origin029
  Placement = pos=(0,14,0) rot=(0,0,1;0rad)
  Tip = -> AdditivePipe002
FEATURE [App::Link] wire_orange  label="047_wire-orange001"
  LinkPlacement = pos=(88.5,1.07734,-104.8) rot=(0,1,0;3.14159rad)
  LinkedObject = -> Body018
  Placement = pos=(88.5,1.07734,-104.8) rot=(0,1,0;3.14159rad)
FEATURE [App::Link] wire_red  label="048_wire-red001"
  LinkPlacement = pos=(28.5,-0.122661,-164.8) rot=(0,0,1;0rad)
  LinkedObject = -> Body016
  Placement = pos=(28.5,-0.122661,-164.8) rot=(0,0,1;0rad)
FEATURE [App::Link] wire_brown  label="049_wire-brown001"
  LinkPlacement = pos=(28.5,-1.32266,-164.8) rot=(0,0,1;0rad)
  LinkedObject = -> Body017
  Placement = pos=(28.5,-1.32266,-164.8) rot=(0,0,1;0rad)
FEATURE [App::Link] Socket001  label="050_Socket001"
  LinkPlacement = pos=(91.55,-2.64766,-164.475) rot=(0,0,-1;1.5708rad)
  LinkedObject = -> Socket
  Placement = pos=(91.55,-2.64766,-164.475) rot=(0,0,-1;1.5708rad)
FEATURE [App::Link] Socket002  label="051_Socket002"
  LinkPlacement = pos=(91.55,-0.447661,-164.475) rot=(0,0,1;4.71239rad)
  LinkedObject = -> Socket
  Placement = pos=(91.55,-0.447661,-164.475) rot=(0,0,1;4.71239rad)
FEATURE [App::Link] Socket003  label="052_Socket003"
  LinkPlacement = pos=(91.55,1.75234,-164.475) rot=(0,0,1;4.71239rad)
  LinkedObject = -> Socket
  Placement = pos=(91.55,1.75234,-164.475) rot=(0,0,1;4.71239rad)
FEATURE [App::FeaturePython] Joint048  label="Fixed048"  # Assembly joint (typed FeaturePython)
  Activated = true
  AngleMax = 0
  AngleMin = 0
  Detach1 = false
  Detach2 = false
  Distance = 0
  Distance2 = 0
  EnableAngleMax = false
  EnableAngleMin = false
  EnableLengthMax = false
  EnableLengthMin = false
  JointType = 0 (Fixed)
  LengthMax = 0
  LengthMin = 0
  Offset2 = pos=(0,0,0) rot=(0,0,1;1.5708rad)
  Placement1 = pos=(60,0,0) rot=(0.57735,0.57735,0.57735;2.0944rad)
  Placement2 = pos=(0,0,3) rot=(0,0,1;1.5708rad)
  Reference1 = -> Assembly [wire_orange.Edge3,wire_orange.Edge3]
  Reference2 = -> Assembly [M90S_ali002.Part__Feature128.Edge1,M90S_ali002.Part__Feature128.Edge1]
FEATURE [App::FeaturePython] Joint049  label="Fixed049"  # Assembly joint (typed FeaturePython)
  Activated = true
  AngleMax = 0
  AngleMin = 0
  Detach1 = false
  Detach2 = false
  Distance = 0
  Distance2 = 0
  EnableAngleMax = false
  EnableAngleMin = false
  EnableLengthMax = false
  EnableLengthMin = false
  JointType = 0 (Fixed)
  LengthMax = 0
  LengthMin = 0
  Offset2 = pos=(0,0,0) rot=(0,0,1;1.5708rad)
  Placement1 = pos=(7.1e-15,2e-14,60) rot=(0.57735,0.57735,0.57735;2.0944rad)
  Placement2 = pos=(0,0,3) rot=(0,0,1;1.5708rad)
  Reference1 = -> Assembly [wire_red.Edge1,wire_red.Edge1]
  Reference2 = -> Assembly [M90S_ali002.Part__Feature125.Edge1,M90S_ali002.Part__Feature125.Edge1]
FEATURE [App::FeaturePython] Joint050  label="Fixed050"  # Assembly joint (typed FeaturePython)
  Activated = true
  AngleMax = 0
  AngleMin = 0
  Detach1 = false
  Detach2 = false
  Distance = 0
  Distance2 = 0
  EnableAngleMax = false
  EnableAngleMin = false
  EnableLengthMax = false
  EnableLengthMin = false
  JointType = 0 (Fixed)
  LengthMax = 0
  LengthMin = 0
  Offset2 = pos=(0,0,0) rot=(0,0,-1;1.5708rad)
  Placement1 = pos=(0,0,3) rot=(0,0,1;0rad)
  Placement2 = pos=(7.1e-15,2e-14,60) rot=(0,1,0;1.5708rad)
  Reference1 = -> Assembly [M90S_ali002.Part__Feature127.Edge1,M90S_ali002.Part__Feature127.Edge1]
  Reference2 = -> Assembly [wire_brown.Edge1,wire_brown.Edge1]
FEATURE [App::FeaturePython] Joint051  label="Fixed051"  # Assembly joint (typed FeaturePython)
  Activated = true
  AngleMax = 0
  AngleMin = 0
  Detach1 = false
  Detach2 = false
  Distance = 0
  Distance2 = 0
  EnableAngleMax = false
  EnableAngleMin = false
  EnableLengthMax = false
  EnableLengthMin = false
  JointType = 0 (Fixed)
  LengthMax = 0
  LengthMin = 0
  Offset1 = pos=(0,-1,0) rot=(0,0,1;0rad)
  Offset2 = pos=(0,0,0) rot=(0,0,1;1.5708rad)
  Placement1 = pos=(-1.325,-3.05,-0.325) rot=(0.57735,0.57735,0.57735;4.18879rad)
  Placement2 = pos=(60,0,0) rot=(0.707107,0,0.707107;3.14159rad)
  Reference1 = -> Assembly [Socket001.Part__Feature178.Edge16,Socket001.Part__Feature178.Vertex6]
  Reference2 = -> Assembly [wire_brown.Edge3,wire_brown.Edge3]
FEATURE [App::FeaturePython] Joint052  label="Fixed052"  # Assembly joint (typed FeaturePython)
  Activated = true
  AngleMax = 0
  AngleMin = 0
  Detach1 = false
  Detach2 = false
  Distance = 0
  Distance2 = 0
  EnableAngleMax = false
  EnableAngleMin = false
  EnableLengthMax = false
  EnableLengthMin = false
  JointType = 0 (Fixed)
  LengthMax = 0
  LengthMin = 0
  Offset2 = pos=(0,0,0) rot=(0,0,1;1.5708rad)
  Placement1 = pos=(-0.325,-3.05,-0.325) rot=(0.57735,0.57735,0.57735;4.18879rad)
  Placement2 = pos=(60,0,0) rot=(0.707107,0,0.707107;3.14159rad)
  Reference1 = -> Assembly [Socket002.Part__Feature178.Edge16,Socket002.Part__Feature178.Vertex6]
  Reference2 = -> Assembly [wire_red.Edge3,wire_red.Edge3]
FEATURE [App::FeaturePython] Joint053  label="Fixed053"  # Assembly joint (typed FeaturePython)
  Activated = true
  AngleMax = 0
  AngleMin = 0
  Detach1 = false
  Detach2 = false
  Distance = 0
  Distance2 = 0
  EnableAngleMax = false
  EnableAngleMin = false
  EnableLengthMax = false
  EnableLengthMin = false
  JointType = 0 (Fixed)
  LengthMax = 0
  LengthMin = 0
  Offset1 = pos=(1,0,0) rot=(0,0,1;0rad)
  Offset2 = pos=(0,0,0) rot=(0,0,-1;1.5708rad)
  Placement1 = pos=(-1e-16,1,60) rot=(0.57735,0.57735,0.57735;2.0944rad)
  Placement2 = pos=(-0.325,-3.05,-0.325) rot=(0,0.707107,0.707107;3.14159rad)
  Reference1 = -> Assembly [wire_orange.Edge1,wire_orange.Edge1]
  Reference2 = -> Assembly [Socket003.Part__Feature178.Edge16,Socket003.Part__Feature178.Vertex6]
FEATURE [App::Link] wire_orange001  label="053_wire-orange002"
  LinkPlacement = pos=(58.8,-8.4,18.5) rot=(-0.57735,0.57735,0.57735;4.18879rad)
  LinkedObject = -> Body018
  Placement = pos=(58.8,-8.4,18.5) rot=(-0.57735,0.57735,0.57735;4.18879rad)
FEATURE [App::Link] wire_red001  label="054_wire-red002"
  LinkPlacement = pos=(60,-8.4,18.5) rot=(-0.57735,0.57735,0.57735;4.18879rad)
  LinkedObject = -> Body016
  Placement = pos=(60,-8.4,18.5) rot=(-0.57735,0.57735,0.57735;4.18879rad)
FEATURE [App::Link] wire_brown001  label="055_wire-brown002"
  LinkPlacement = pos=(61.2,-8.4,18.5) rot=(-0.57735,0.57735,0.57735;4.18879rad)
  LinkedObject = -> Body017
  Placement = pos=(61.2,-8.4,18.5) rot=(-0.57735,0.57735,0.57735;4.18879rad)
FEATURE [App::FeaturePython] Joint054  label="Fixed054"  # Assembly joint (typed FeaturePython)
  Activated = true
  AngleMax = 0
  AngleMin = 0
  Detach1 = false
  Detach2 = false
  Distance = 0
  Distance2 = 0
  EnableAngleMax = false
  EnableAngleMin = false
  EnableLengthMax = false
  EnableLengthMin = false
  JointType = 0 (Fixed)
  LengthMax = 0
  LengthMin = 0
  Placement1 = pos=(1.07e-14,2.13e-14,60) rot=(-0.57735,-0.57735,-0.57735;4.18879rad)
  Placement2 = pos=(0,0,3) rot=(0,0,1;0rad)
  Reference1 = -> Assembly [wire_orange001.Edge1,wire_orange001.Edge1]
  Reference2 = -> Assembly [M90S_ali001.Part__Feature128.Edge1,M90S_ali001.Part__Feature128.Edge1]
FEATURE [App::FeaturePython] Joint055  label="Fixed055"  # Assembly joint (typed FeaturePython)
  Activated = true
  AngleMax = 0
  AngleMin = 0
  Detach1 = false
  Detach2 = false
  Distance = 0
  Distance2 = 0
  EnableAngleMax = false
  EnableAngleMin = false
  EnableLengthMax = false
  EnableLengthMin = false
  JointType = 0 (Fixed)
  LengthMax = 0
  LengthMin = 0
  Placement1 = pos=(0,0,3) rot=(0,0,1;0rad)
  Placement2 = pos=(1.07e-14,2.13e-14,60) rot=(-0.57735,-0.57735,-0.57735;4.18879rad)
  Reference1 = -> Assembly [M90S_ali001.Part__Feature125.Edge1,M90S_ali001.Part__Feature125.Edge1]
  Reference2 = -> Assembly [wire_red001.Edge1,wire_red001.Edge1]
FEATURE [App::FeaturePython] Joint056  label="Fixed056"  # Assembly joint (typed FeaturePython)
  Activated = true
  AngleMax = 0
  AngleMin = 0
  Detach1 = false
  Detach2 = false
  Distance = 0
  Distance2 = 0
  EnableAngleMax = false
  EnableAngleMin = false
  EnableLengthMax = false
  EnableLengthMin = false
  JointType = 0 (Fixed)
  LengthMax = 0
  LengthMin = 0
  Placement1 = pos=(0,0,3) rot=(0,0,1;0rad)
  Placement2 = pos=(1.24e-14,2.13e-14,60) rot=(-0.57735,-0.57735,-0.57735;4.18879rad)
  Reference1 = -> Assembly [M90S_ali001.Part__Feature127.Edge1,M90S_ali001.Part__Feature127.Edge1]
  Reference2 = -> Assembly [wire_brown001.Edge1,wire_brown001.Edge1]
FEATURE [App::Link] Socket004  label="056_Socket004"
  LinkPlacement = pos=(57.475,-71.45,18.825) rot=(0,0,1;3.14159rad)
  LinkedObject = -> Socket
  Placement = pos=(57.475,-71.45,18.825) rot=(0,0,1;3.14159rad)
FEATURE [App::Link] Socket005  label="057_Socket005"
  LinkPlacement = pos=(59.675,-71.45,18.825) rot=(0,0,1;3.14159rad)
  LinkedObject = -> Socket
  Placement = pos=(59.675,-71.45,18.825) rot=(0,0,1;3.14159rad)
FEATURE [App::Link] Socket006  label="058_Socket006"
  LinkPlacement = pos=(61.875,-71.45,18.825) rot=(0,0,1;3.14159rad)
  LinkedObject = -> Socket
  Placement = pos=(61.875,-71.45,18.825) rot=(0,0,1;3.14159rad)
FEATURE [App::FeaturePython] Joint057  label="Fixed057"  # Assembly joint (typed FeaturePython)
  Activated = true
  AngleMax = 0
  AngleMin = 0
  Detach1 = false
  Detach2 = false
  Distance = 0
  Distance2 = 0
  EnableAngleMax = false
  EnableAngleMin = false
  EnableLengthMax = false
  EnableLengthMin = false
  JointType = 0 (Fixed)
  LengthMax = 0
  LengthMin = 0
  Offset1 = pos=(0,1,0) rot=(0,0,1;0rad)
  Placement1 = pos=(60,1e-16,1) rot=(-0.57735,-0.57735,-0.57735;4.18879rad)
  Placement2 = pos=(-0.325,-3.05,-0.325) rot=(0.57735,0.57735,0.57735;4.18879rad)
  Reference1 = -> Assembly [wire_orange001.Edge3,wire_orange001.Edge3]
  Reference2 = -> Assembly [Socket004.Part__Feature178.Edge16,Socket004.Part__Feature178.Vertex6]
FEATURE [App::FeaturePython] Joint058  label="Fixed058"  # Assembly joint (typed FeaturePython)
  Activated = true
  AngleMax = 0
  AngleMin = 0
  Detach1 = false
  Detach2 = false
  Distance = 0
  Distance2 = 0
  EnableAngleMax = false
  EnableAngleMin = false
  EnableLengthMax = false
  EnableLengthMin = false
  JointType = 0 (Fixed)
  LengthMax = 0
  LengthMin = 0
  Placement1 = pos=(60,0,-7.1e-15) rot=(-0.57735,-0.57735,-0.57735;4.18879rad)
  Placement2 = pos=(-0.325,-3.05,-0.325) rot=(0.57735,0.57735,0.57735;4.18879rad)
  Reference1 = -> Assembly [wire_red001.Edge3,wire_red001.Edge3]
  Reference2 = -> Assembly [Socket005.Part__Feature178.Edge16,Socket005.Part__Feature178.Vertex6]
FEATURE [App::FeaturePython] Joint059  label="Fixed059"  # Assembly joint (typed FeaturePython)
  Activated = true
  AngleMax = 0
  AngleMin = 0
  Detach1 = false
  Detach2 = false
  Distance = 0
  Distance2 = 0
  EnableAngleMax = false
  EnableAngleMin = false
  EnableLengthMax = false
  EnableLengthMin = false
  JointType = 0 (Fixed)
  LengthMax = 0
  LengthMin = 0
  Offset1 = pos=(0,-1,0) rot=(0,0,1;0rad)
  Placement1 = pos=(60,0,-1) rot=(-0.57735,-0.57735,-0.57735;4.18879rad)
  Placement2 = pos=(-0.325,-3.05,-0.325) rot=(0.57735,0.57735,0.57735;4.18879rad)
  Reference1 = -> Assembly [wire_brown001.Edge3,wire_brown001.Edge3]
  Reference2 = -> Assembly [Socket006.Part__Feature178.Edge16,Socket006.Part__Feature178.Vertex6]
FEATURE [App::Link] BreadBoard  label="059_BreadBoard001"
  LinkPlacement = pos=(150,-0.0800073,-228.7) rot=(-0.57735,0.57735,0.57735;4.18879rad)
  LinkedObject = -> Part__Feature179
  Placement = pos=(150,-0.0800073,-228.7) rot=(-0.57735,0.57735,0.57735;4.18879rad)
FEATURE [App::Link] ____ESP8266_NodeMCU_Board____  label="060_+++ ESP8266 NodeMCU Board +++001"
  LinkPlacement = pos=(150,-18.21,-218.3) rot=(1,0,0;1.5708rad)
  LinkedObject = -> Part__Feature
  Placement = pos=(150,-18.21,-218.3) rot=(1,0,0;1.5708rad)
FEATURE [App::Link] Pin001  label="061_Pin001"
  LinkPlacement = pos=(163.5,-3.43001,-216.8) rot=(-0.57735,0.57735,0.57735;4.18879rad)
  LinkedObject = -> Pin
  Placement = pos=(163.5,-3.43001,-216.8) rot=(-0.57735,0.57735,0.57735;4.18879rad)
FEATURE [App::Link] Socket007  label="062_Socket007"
  LinkPlacement = pos=(163.5,-3.43001,-213.85) rot=(0.57735,-0.57735,0.57735;4.18879rad)
  LinkedObject = -> Socket
  Placement = pos=(163.5,-3.43001,-213.85) rot=(0.57735,-0.57735,0.57735;4.18879rad)
FEATURE [App::Link] Socket008  label="063_Socket008"
  LinkPlacement = pos=(163.5,-5.93001,-213.85) rot=(-0.57735,0.57735,-0.57735;2.0944rad)
  LinkedObject = -> Socket
  Placement = pos=(163.5,-5.93001,-213.85) rot=(-0.57735,0.57735,-0.57735;2.0944rad)
FEATURE [App::Link] Pin002  label="064_Pin002"
  LinkPlacement = pos=(163.5,-5.93001,-216.8) rot=(0.57735,-0.57735,-0.57735;2.0944rad)
  LinkedObject = -> Pin
  Placement = pos=(163.5,-5.93001,-216.8) rot=(0.57735,-0.57735,-0.57735;2.0944rad)
FEATURE [App::Link] Socket009  label="065_Socket009"
  LinkPlacement = pos=(163.5,-20.93,-213.85) rot=(-0.57735,0.57735,-0.57735;2.0944rad)
  LinkedObject = -> Socket
  Placement = pos=(163.5,-20.93,-213.85) rot=(-0.57735,0.57735,-0.57735;2.0944rad)
FEATURE [App::Link] Pin003  label="066_Pin003"
  LinkPlacement = pos=(163.5,-20.93,-216.8) rot=(0.57735,-0.57735,-0.57735;2.0944rad)
  LinkedObject = -> Pin
  Placement = pos=(163.5,-20.93,-216.8) rot=(0.57735,-0.57735,-0.57735;2.0944rad)
FEATURE [App::FeaturePython] Joint060  label="Fixed060"  # Assembly joint (typed FeaturePython)
  Activated = true
  AngleMax = 0
  AngleMin = 0
  Detach1 = false
  Detach2 = false
  Distance = 0
  Distance2 = 0
  EnableAngleMax = false
  EnableAngleMin = false
  EnableLengthMax = false
  EnableLengthMin = false
  JointType = 0 (Fixed)
  LengthMax = 0
  LengthMin = 0
  Offset1 = pos=(150,0,0) rot=(0,0,1;0rad)
  Offset2 = pos=(0,0,0) rot=(0,0,1;1.5708rad)
  Placement1 = pos=(-0.0800073,1.67e-14,150) rot=(-0.57735,-0.57735,-0.57735;2.0944rad)
  Placement2 = pos=(0,-2e-16,0) rot=(0,0,1;1.5708rad)
  Reference1 = -> Assembly [BreadBoard.Face2130,BreadBoard.Face2130]
  Reference2 = -> Assembly [Base.Face13,Base.Face13]
FEATURE [App::FeaturePython] Joint061  label="Fixed061"  # Assembly joint (typed FeaturePython)
  Activated = true
  AngleMax = 0
  AngleMin = 0
  Detach1 = false
  Detach2 = false
  Distance = 0
  Distance2 = 0
  EnableAngleMax = false
  EnableAngleMin = false
  EnableLengthMax = false
  EnableLengthMin = false
  JointType = 0 (Fixed)
  LengthMax = 0
  LengthMin = 0
  Offset1 = pos=(0.5,0,0) rot=(0,0,1;0rad)
  Placement1 = pos=(35.85,2.5,11.5) rot=(-0.57735,-0.57735,-0.57735;2.0944rad)
  Placement2 = pos=(-11.5,-7.9,17.72) rot=(0,0.707107,0.707107;3.14159rad)
  Reference1 = -> Assembly [BreadBoard.Face899,BreadBoard.Face899]
  Reference2 = -> Assembly [____ESP8266_NodeMCU_Board____.Face959,____ESP8266_NodeMCU_Board____.Face959]
FEATURE [App::FeaturePython] Joint062  label="Fixed062"  # Assembly joint (typed FeaturePython)
  Activated = true
  AngleMax = 0
  AngleMin = 0
  Detach1 = false
  Detach2 = false
  Distance = 0
  Distance2 = 0
  EnableAngleMax = false
  EnableAngleMin = false
  EnableLengthMax = false
  EnableLengthMin = false
  JointType = 0 (Fixed)
  LengthMax = 0
  LengthMin = 0
  Placement1 = pos=(3.35,2.5,-13.5) rot=(0.57735,-0.57735,-0.57735;4.18879rad)
  Placement2 = pos=(0,-9.4,0) rot=(-0.57735,0.57735,0.57735;2.0944rad)
  Reference1 = -> Assembly [BreadBoard.Face680,BreadBoard.Face680]
  Reference2 = -> Assembly [Pin001.Part__Feature177.Face10,Pin001.Part__Feature177.Face10]
FEATURE [App::FeaturePython] Joint063  label="Fixed063"  # Assembly joint (typed FeaturePython)
  Activated = true
  AngleMax = 0
  AngleMin = 0
  Detach1 = false
  Detach2 = false
  Distance = 0
  Distance2 = 0
  EnableAngleMax = false
  EnableAngleMin = false
  EnableLengthMax = false
  EnableLengthMin = false
  JointType = 0 (Fixed)
  LengthMax = 0
  LengthMin = 0
  Offset2 = pos=(0,0,13) rot=(0,0,1;3.14159rad)
  Placement1 = pos=(0.325,7.05,0.325) rot=(-0.57735,-0.57735,0.57735;4.18879rad)
  Placement2 = pos=(0.325,-4.1,-0.325) rot=(-0.57735,0.57735,-0.57735;4.18879rad)
  Reference1 = -> Assembly [Socket007.Part__Feature178.Face11,Socket007.Part__Feature178.Vertex52]
  Reference2 = -> Assembly [Pin001.Part__Feature177.Edge2,Pin001.Part__Feature177.Vertex3]
FEATURE [App::FeaturePython] Joint064  label="Fixed064"  # Assembly joint (typed FeaturePython)
  Activated = true
  AngleMax = 0
  AngleMin = 0
  Detach1 = false
  Detach2 = false
  Distance = 0
  Distance2 = 0
  EnableAngleMax = false
  EnableAngleMin = false
  EnableLengthMax = false
  EnableLengthMin = false
  JointType = 0 (Fixed)
  LengthMax = 0
  LengthMin = 0
  Placement1 = pos=(0,-9.4,0) rot=(-0.57735,0.57735,0.57735;2.0944rad)
  Placement2 = pos=(5.85,2.5,-13.5) rot=(0.57735,-0.57735,-0.57735;4.18879rad)
  Reference1 = -> Assembly [Pin002.Part__Feature177.Face10,Pin002.Part__Feature177.Face10]
  Reference2 = -> Assembly [BreadBoard.Face686,BreadBoard.Face686]
FEATURE [App::FeaturePython] Joint065  label="Fixed065"  # Assembly joint (typed FeaturePython)
  Activated = true
  AngleMax = 0
  AngleMin = 0
  Detach1 = false
  Detach2 = false
  Distance = 0
  Distance2 = 0
  EnableAngleMax = false
  EnableAngleMin = false
  EnableLengthMax = false
  EnableLengthMin = false
  JointType = 0 (Fixed)
  LengthMax = 0
  LengthMin = 0
  Offset2 = pos=(0,0,13) rot=(0,0,1;3.14159rad)
  Placement1 = pos=(0.325,8.9,-0.325) rot=(-0.57735,-0.57735,0.57735;4.18879rad)
  Placement2 = pos=(0.325,-5.95,0.325) rot=(-0.57735,0.57735,-0.57735;4.18879rad)
  Reference1 = -> Assembly [Pin002.Part__Feature177.Edge2,Pin002.Part__Feature177.Vertex3]
  Reference2 = -> Assembly [Socket008.Part__Feature178.Face11,Socket008.Part__Feature178.Vertex52]
FEATURE [App::FeaturePython] Joint066  label="Fixed066"  # Assembly joint (typed FeaturePython)
  Activated = true
  AngleMax = 0
  AngleMin = 0
  Detach1 = false
  Detach2 = false
  Distance = 0
  Distance2 = 0
  EnableAngleMax = false
  EnableAngleMin = false
  EnableLengthMax = false
  EnableLengthMin = false
  JointType = 0 (Fixed)
  LengthMax = 0
  LengthMin = 0
  Placement1 = pos=(20.85,2.5,-13.5) rot=(0.57735,-0.57735,-0.57735;4.18879rad)
  Placement2 = pos=(0,-9.4,0) rot=(-0.57735,0.57735,0.57735;2.0944rad)
  Reference1 = -> Assembly [BreadBoard.Face648,BreadBoard.Face648]
  Reference2 = -> Assembly [Pin003.Part__Feature177.Face10,Pin003.Part__Feature177.Face10]
FEATURE [App::FeaturePython] Joint067  label="Fixed067"  # Assembly joint (typed FeaturePython)
  Activated = true
  AngleMax = 0
  AngleMin = 0
  Detach1 = false
  Detach2 = false
  Distance = 0
  Distance2 = 0
  EnableAngleMax = false
  EnableAngleMin = false
  EnableLengthMax = false
  EnableLengthMin = false
  JointType = 0 (Fixed)
  LengthMax = 0
  LengthMin = 0
  Offset2 = pos=(0,0,13) rot=(0,0,1;3.14159rad)
  Placement1 = pos=(0.325,7.05,0.325) rot=(-0.57735,-0.57735,0.57735;4.18879rad)
  Placement2 = pos=(0.325,-4.1,-0.325) rot=(-0.57735,0.57735,-0.57735;4.18879rad)
  Reference1 = -> Assembly [Socket009.Part__Feature178.Face11,Socket009.Part__Feature178.Vertex52]
  Reference2 = -> Assembly [Pin003.Part__Feature177.Edge2,Pin003.Part__Feature177.Vertex3]
FEATURE [App::Link] Socket010  label="067_Socket010"
  LinkPlacement = pos=(163.5,-18.43,-213.85) rot=(-0.57735,0.57735,-0.57735;2.0944rad)
  LinkedObject = -> Socket
  Placement = pos=(163.5,-18.43,-213.85) rot=(-0.57735,0.57735,-0.57735;2.0944rad)
FEATURE [App::Link] Pin004  label="068_Pin004"
  LinkPlacement = pos=(163.5,-18.43,-216.8) rot=(0.57735,-0.57735,-0.57735;2.0944rad)
  LinkedObject = -> Pin
  Placement = pos=(163.5,-18.43,-216.8) rot=(0.57735,-0.57735,-0.57735;2.0944rad)
FEATURE [App::FeaturePython] Joint068  label="Fixed068"  # Assembly joint (typed FeaturePython)
  Activated = true
  AngleMax = 0
  AngleMin = 0
  Detach1 = false
  Detach2 = false
  Distance = 0
  Distance2 = 0
  EnableAngleMax = false
  EnableAngleMin = false
  EnableLengthMax = false
  EnableLengthMin = false
  JointType = 0 (Fixed)
  LengthMax = 0
  LengthMin = 0
  Placement1 = pos=(0,-9.4,0) rot=(-0.57735,0.57735,0.57735;2.0944rad)
  Placement2 = pos=(18.35,2.5,-13.5) rot=(0.57735,-0.57735,-0.57735;4.18879rad)
  Reference1 = -> Assembly [Pin004.Part__Feature177.Face10,Pin004.Part__Feature177.Face10]
  Reference2 = -> Assembly [BreadBoard.Face651,BreadBoard.Face651]
FEATURE [App::FeaturePython] Joint069  label="Fixed069"  # Assembly joint (typed FeaturePython)
  Activated = true
  AngleMax = 0
  AngleMin = 0
  Detach1 = false
  Detach2 = false
  Distance = 0
  Distance2 = 0
  EnableAngleMax = false
  EnableAngleMin = false
  EnableLengthMax = false
  EnableLengthMin = false
  JointType = 0 (Fixed)
  LengthMax = 0
  LengthMin = 0
  Offset2 = pos=(0,0,13) rot=(0,0,1;3.14159rad)
  Placement1 = pos=(0.325,8.9,-0.325) rot=(-0.57735,-0.57735,0.57735;4.18879rad)
  Placement2 = pos=(0.325,-5.95,0.325) rot=(-0.57735,0.57735,-0.57735;4.18879rad)
  Reference1 = -> Assembly [Pin004.Part__Feature177.Edge2,Pin004.Part__Feature177.Vertex3]
  Reference2 = -> Assembly [Socket010.Part__Feature178.Face11,Socket010.Part__Feature178.Vertex52]
FEATURE [App::Link] Pin005  label="069_Pin005"
  LinkPlacement = pos=(136.5,-35.93,-216.8) rot=(0.57735,0.57735,0.57735;2.0944rad)
  LinkedObject = -> Pin
  Placement = pos=(136.5,-35.93,-216.8) rot=(0.57735,0.57735,0.57735;2.0944rad)
FEATURE [App::FeaturePython] Joint070  label="Fixed070"  # Assembly joint (typed FeaturePython)
  Activated = true
  AngleMax = 0
  AngleMin = 0
  Detach1 = false
  Detach2 = false
  Distance = 0
  Distance2 = 0
  EnableAngleMax = false
  EnableAngleMin = false
  EnableLengthMax = false
  EnableLengthMin = false
  JointType = 0 (Fixed)
  LengthMax = 0
  LengthMin = 0
  Placement1 = pos=(0,-9.4,0) rot=(-0.57735,0.57735,0.57735;2.0944rad)
  Placement2 = pos=(35.85,2.5,13.5) rot=(-0.57735,-0.57735,-0.57735;2.0944rad)
  Reference1 = -> Assembly [Pin005.Part__Feature177.Face10,Pin005.Part__Feature177.Face10]
  Reference2 = -> Assembly [BreadBoard.Face902,BreadBoard.Face902]
FEATURE [App::Link] Socket011  label="070_Socket011"
  LinkPlacement = pos=(136.5,-35.93,-213.85) rot=(-0.57735,-0.57735,0.57735;2.0944rad)
  LinkedObject = -> Socket
  Placement = pos=(136.5,-35.93,-213.85) rot=(-0.57735,-0.57735,0.57735;2.0944rad)
FEATURE [App::FeaturePython] Joint071  label="Fixed071"  # Assembly joint (typed FeaturePython)
  Activated = true
  AngleMax = 0
  AngleMin = 0
  Detach1 = false
  Detach2 = false
  Distance = 0
  Distance2 = 0
  EnableAngleMax = false
  EnableAngleMin = false
  EnableLengthMax = false
  EnableLengthMin = false
  JointType = 0 (Fixed)
  LengthMax = 0
  LengthMin = 0
  Offset2 = pos=(0,0,13) rot=(0,0,1;3.14159rad)
  Placement1 = pos=(0.325,8.9,-0.325) rot=(-0.57735,-0.57735,0.57735;4.18879rad)
  Placement2 = pos=(0.325,-5.95,0.325) rot=(-0.57735,0.57735,-0.57735;4.18879rad)
  Reference1 = -> Assembly [Pin005.Part__Feature177.Edge2,Pin005.Part__Feature177.Vertex3]
  Reference2 = -> Assembly [Socket011.Part__Feature178.Face11,Socket011.Part__Feature178.Vertex52]
FEATURE [App::Link] Pin006  label="071_Pin006"
  LinkPlacement = pos=(136.5,-33.43,-216.8) rot=(0.57735,0.57735,0.57735;2.0944rad)
  LinkedObject = -> Pin
  Placement = pos=(136.5,-33.43,-216.8) rot=(0.57735,0.57735,0.57735;2.0944rad)
FEATURE [App::Link] Socket012  label="072_Socket012"
  LinkPlacement = pos=(136.5,-33.43,-213.85) rot=(-0.57735,-0.57735,0.57735;2.0944rad)
  LinkedObject = -> Socket
  Placement = pos=(136.5,-33.43,-213.85) rot=(-0.57735,-0.57735,0.57735;2.0944rad)
FEATURE [App::FeaturePython] Joint072  label="Fixed072"  # Assembly joint (typed FeaturePython)
  Activated = true
  AngleMax = 0
  AngleMin = 0
  Detach1 = false
  Detach2 = false
  Distance = 0
  Distance2 = 0
  EnableAngleMax = false
  EnableAngleMin = false
  EnableLengthMax = false
  EnableLengthMin = false
  JointType = 0 (Fixed)
  LengthMax = 0
  LengthMin = 0
  Placement1 = pos=(0,-9.4,0) rot=(-0.57735,0.57735,0.57735;2.0944rad)
  Placement2 = pos=(33.35,2.5,13.5) rot=(-0.57735,-0.57735,-0.57735;2.0944rad)
  Reference1 = -> Assembly [Pin006.Part__Feature177.Face10,Pin006.Part__Feature177.Face10]
  Reference2 = -> Assembly [BreadBoard.Face911,BreadBoard.Face911]
FEATURE [App::FeaturePython] Joint073  label="Fixed073"  # Assembly joint (typed FeaturePython)
  Activated = true
  AngleMax = 0
  AngleMin = 0
  Detach1 = false
  Detach2 = false
  Distance = 0
  Distance2 = 0
  EnableAngleMax = false
  EnableAngleMin = false
  EnableLengthMax = false
  EnableLengthMin = false
  JointType = 0 (Fixed)
  LengthMax = 0
  LengthMin = 0
  Offset2 = pos=(0,0,13) rot=(0,0,1;3.14159rad)
  Placement1 = pos=(0.325,8.9,-0.325) rot=(-0.57735,-0.57735,0.57735;4.18879rad)
  Placement2 = pos=(0.325,-5.95,0.325) rot=(-0.57735,0.57735,-0.57735;4.18879rad)
  Reference1 = -> Assembly [Pin006.Part__Feature177.Edge2,Pin006.Part__Feature177.Vertex3]
  Reference2 = -> Assembly [Socket012.Part__Feature178.Face11,Socket012.Part__Feature178.Vertex52]
FEATURE [App::Link] Pin007  label="073_Pin007"
  LinkPlacement = pos=(128.5,-34.43,-216.8) rot=(0.57735,-0.57735,-0.57735;2.0944rad)
  LinkedObject = -> Pin
  Placement = pos=(128.5,-34.43,-216.8) rot=(0.57735,-0.57735,-0.57735;2.0944rad)
FEATURE [App::Link] Socket013  label="074_Socket013"
  LinkPlacement = pos=(128.5,-34.43,-213.85) rot=(-0.57735,-0.57735,0.57735;2.0944rad)
  LinkedObject = -> Socket
  Placement = pos=(128.5,-34.43,-213.85) rot=(-0.57735,-0.57735,0.57735;2.0944rad)
FEATURE [App::FeaturePython] Joint074  label="Fixed074"  # Assembly joint (typed FeaturePython)
  Activated = true
  AngleMax = 0
  AngleMin = 0
  Detach1 = false
  Detach2 = false
  Distance = 0
  Distance2 = 0
  EnableAngleMax = false
  EnableAngleMin = false
  EnableLengthMax = false
  EnableLengthMin = false
  JointType = 0 (Fixed)
  LengthMax = 0
  LengthMin = 0
  Placement1 = pos=(0,-9.4,0) rot=(-0.57735,0.57735,0.57735;2.0944rad)
  Placement2 = pos=(34.35,2.5,21.5) rot=(-0.57735,-0.57735,0.57735;4.18879rad)
  Reference1 = -> Assembly [Pin007.Part__Feature177.Face10,Pin007.Part__Feature177.Face10]
  Reference2 = -> Assembly [BreadBoard.Face27,BreadBoard.Face27]
FEATURE [App::FeaturePython] Joint075  label="Fixed075"  # Assembly joint (typed FeaturePython)
  Activated = true
  AngleMax = 0
  AngleMin = 0
  Detach1 = false
  Detach2 = false
  Distance = 0
  Distance2 = 0
  EnableAngleMax = false
  EnableAngleMin = false
  EnableLengthMax = false
  EnableLengthMin = false
  JointType = 0 (Fixed)
  LengthMax = 0
  LengthMin = 0
  Offset2 = pos=(0,0,13) rot=(0,0,1;0rad)
  Placement1 = pos=(-0.325,8.9,0.325) rot=(-0.57735,-0.57735,0.57735;4.18879rad)
  Placement2 = pos=(0.325,-5.95,0.325) rot=(-0.57735,-0.57735,0.57735;4.18879rad)
  Reference1 = -> Assembly [Pin007.Part__Feature177.Edge9,Pin007.Part__Feature177.Vertex8]
  Reference2 = -> Assembly [Socket013.Part__Feature178.Face11,Socket013.Part__Feature178.Vertex52]
FEATURE [App::Link] Pin008  label="075_Pin008"
  LinkPlacement = pos=(126,-31.93,-216.8) rot=(0.57735,-0.57735,-0.57735;2.0944rad)
  LinkedObject = -> Pin
  Placement = pos=(126,-31.93,-216.8) rot=(0.57735,-0.57735,-0.57735;2.0944rad)
FEATURE [App::Link] Socket014  label="076_Socket014"
  LinkPlacement = pos=(126,-31.93,-213.85) rot=(-0.57735,-0.57735,0.57735;2.0944rad)
  LinkedObject = -> Socket
  Placement = pos=(126,-31.93,-213.85) rot=(-0.57735,-0.57735,0.57735;2.0944rad)
FEATURE [App::FeaturePython] Joint076  label="Fixed076"  # Assembly joint (typed FeaturePython)
  Activated = true
  AngleMax = 0
  AngleMin = 0
  Detach1 = false
  Detach2 = false
  Distance = 0
  Distance2 = 0
  EnableAngleMax = false
  EnableAngleMin = false
  EnableLengthMax = false
  EnableLengthMin = false
  JointType = 0 (Fixed)
  LengthMax = 0
  LengthMin = 0
  Placement1 = pos=(0,-9.4,0) rot=(-0.57735,0.57735,0.57735;2.0944rad)
  Placement2 = pos=(31.85,2.5,24) rot=(-0.57735,-0.57735,0.57735;4.18879rad)
  Reference1 = -> Assembly [Pin008.Part__Feature177.Face10,Pin008.Part__Feature177.Face10]
  Reference2 = -> Assembly [BreadBoard.Face7,BreadBoard.Face7]
FEATURE [App::FeaturePython] Joint077  label="Fixed077"  # Assembly joint (typed FeaturePython)
  Activated = true
  AngleMax = 0
  AngleMin = 0
  Detach1 = false
  Detach2 = false
  Distance = 0
  Distance2 = 0
  EnableAngleMax = false
  EnableAngleMin = false
  EnableLengthMax = false
  EnableLengthMin = false
  JointType = 0 (Fixed)
  LengthMax = 0
  LengthMin = 0
  Offset2 = pos=(0,0,13) rot=(0,0,1;0rad)
  Placement1 = pos=(-0.325,8.9,0.325) rot=(-0.57735,-0.57735,0.57735;4.18879rad)
  Placement2 = pos=(0.325,-5.95,0.325) rot=(-0.57735,-0.57735,0.57735;4.18879rad)
  Reference1 = -> Assembly [Pin008.Part__Feature177.Edge9,Pin008.Part__Feature177.Vertex8]
  Reference2 = -> Assembly [Socket014.Part__Feature178.Face11,Socket014.Part__Feature178.Vertex52]
FEATURE [App::Link] Pin009  label="077_Pin009"
  LinkPlacement = pos=(126,10.57,-216.8) rot=(0.57735,-0.57735,-0.57735;2.0944rad)
  LinkedObject = -> Pin
  Placement = pos=(126,10.57,-216.8) rot=(0.57735,-0.57735,-0.57735;2.0944rad)
FEATURE [App::Link] Socket015  label="078_Socket015"
  LinkPlacement = pos=(126,10.57,-213.85) rot=(-0.57735,-0.57735,0.57735;2.0944rad)
  LinkedObject = -> Socket
  Placement = pos=(126,10.57,-213.85) rot=(-0.57735,-0.57735,0.57735;2.0944rad)
FEATURE [App::FeaturePython] Joint078  label="Fixed078"  # Assembly joint (typed FeaturePython)
  Activated = true
  AngleMax = 0
  AngleMin = 0
  Detach1 = false
  Detach2 = false
  Distance = 0
  Distance2 = 0
  EnableAngleMax = false
  EnableAngleMin = false
  EnableLengthMax = false
  EnableLengthMin = false
  JointType = 0 (Fixed)
  LengthMax = 0
  LengthMin = 0
  Placement1 = pos=(0,-9.4,0) rot=(-0.57735,0.57735,0.57735;2.0944rad)
  Placement2 = pos=(-10.65,2.5,24) rot=(-0.57735,-0.57735,0.57735;4.18879rad)
  Reference1 = -> Assembly [Pin009.Part__Feature177.Face10,Pin009.Part__Feature177.Face10]
  Reference2 = -> Assembly [BreadBoard.Face37,BreadBoard.Face37]
FEATURE [App::FeaturePython] Joint079  label="Fixed079"  # Assembly joint (typed FeaturePython)
  Activated = true
  AngleMax = 0
  AngleMin = 0
  Detach1 = false
  Detach2 = false
  Distance = 0
  Distance2 = 0
  EnableAngleMax = false
  EnableAngleMin = false
  EnableLengthMax = false
  EnableLengthMin = false
  JointType = 0 (Fixed)
  LengthMax = 0
  LengthMin = 0
  Offset2 = pos=(0,0,13) rot=(0,0,1;0rad)
  Placement1 = pos=(-0.325,8.9,0.325) rot=(-0.57735,-0.57735,0.57735;4.18879rad)
  Placement2 = pos=(0.325,-5.95,0.325) rot=(-0.57735,-0.57735,0.57735;4.18879rad)
  Reference1 = -> Assembly [Pin009.Part__Feature177.Edge9,Pin009.Part__Feature177.Vertex8]
  Reference2 = -> Assembly [Socket015.Part__Feature178.Face11,Socket015.Part__Feature178.Vertex52]
FEATURE [App::Link] Pin010  label="079_Pin010"
  LinkPlacement = pos=(126,13.07,-216.8) rot=(0.57735,-0.57735,-0.57735;2.0944rad)
  LinkedObject = -> Pin
  Placement = pos=(126,13.07,-216.8) rot=(0.57735,-0.57735,-0.57735;2.0944rad)
FEATURE [App::Link] Socket016  label="080_Socket016"
  LinkPlacement = pos=(126,13.07,-213.85) rot=(-0.57735,-0.57735,0.57735;2.0944rad)
  LinkedObject = -> Socket
  Placement = pos=(126,13.07,-213.85) rot=(-0.57735,-0.57735,0.57735;2.0944rad)
FEATURE [App::FeaturePython] Joint080  label="Fixed080"  # Assembly joint (typed FeaturePython)
  Activated = true
  AngleMax = 0
  AngleMin = 0
  Detach1 = false
  Detach2 = false
  Distance = 0
  Distance2 = 0
  EnableAngleMax = false
  EnableAngleMin = false
  EnableLengthMax = false
  EnableLengthMin = false
  JointType = 0 (Fixed)
  LengthMax = 0
  LengthMin = 0
  Placement1 = pos=(0,-9.4,0) rot=(-0.57735,0.57735,0.57735;2.0944rad)
  Placement2 = pos=(-13.15,2.5,24) rot=(-0.57735,-0.57735,0.57735;4.18879rad)
  Reference1 = -> Assembly [Pin010.Part__Feature177.Face10,Pin010.Part__Feature177.Face10]
  Reference2 = -> Assembly [BreadBoard.Face40,BreadBoard.Face40]
FEATURE [App::FeaturePython] Joint081  label="Fixed081"  # Assembly joint (typed FeaturePython)
  Activated = true
  AngleMax = 0
  AngleMin = 0
  Detach1 = false
  Detach2 = false
  Distance = 0
  Distance2 = 0
  EnableAngleMax = false
  EnableAngleMin = false
  EnableLengthMax = false
  EnableLengthMin = false
  JointType = 0 (Fixed)
  LengthMax = 0
  LengthMin = 0
  Offset2 = pos=(0,0,13) rot=(0,0,1;0rad)
  Placement1 = pos=(-0.325,8.9,0.325) rot=(-0.57735,-0.57735,0.57735;4.18879rad)
  Placement2 = pos=(0.325,-5.95,0.325) rot=(-0.57735,-0.57735,0.57735;4.18879rad)
  Reference1 = -> Assembly [Pin010.Part__Feature177.Edge9,Pin010.Part__Feature177.Vertex8]
  Reference2 = -> Assembly [Socket016.Part__Feature178.Face11,Socket016.Part__Feature178.Vertex52]
FEATURE [App::Link] Pin011  label="081_Pin011"
  LinkPlacement = pos=(128.5,15.57,-216.8) rot=(0.57735,-0.57735,-0.57735;2.0944rad)
  LinkedObject = -> Pin
  Placement = pos=(128.5,15.57,-216.8) rot=(0.57735,-0.57735,-0.57735;2.0944rad)
FEATURE [App::Link] Socket017  label="082_Socket017"
  LinkPlacement = pos=(128.5,15.57,-213.85) rot=(-0.57735,-0.57735,0.57735;2.0944rad)
  LinkedObject = -> Socket
  Placement = pos=(128.5,15.57,-213.85) rot=(-0.57735,-0.57735,0.57735;2.0944rad)
FEATURE [App::FeaturePython] Joint082  label="Fixed082"  # Assembly joint (typed FeaturePython)
  Activated = true
  AngleMax = 0
  AngleMin = 0
  Detach1 = false
  Detach2 = false
  Distance = 0
  Distance2 = 0
  EnableAngleMax = false
  EnableAngleMin = false
  EnableLengthMax = false
  EnableLengthMin = false
  JointType = 0 (Fixed)
  LengthMax = 0
  LengthMin = 0
  Placement1 = pos=(0,-9.4,0) rot=(-0.57735,0.57735,0.57735;2.0944rad)
  Placement2 = pos=(-15.65,2.5,21.5) rot=(-0.57735,-0.57735,0.57735;4.18879rad)
  Reference1 = -> Assembly [Pin011.Part__Feature177.Face10,Pin011.Part__Feature177.Face10]
  Reference2 = -> Assembly [BreadBoard.Face19,BreadBoard.Face19]
FEATURE [App::FeaturePython] Joint083  label="Fixed083"  # Assembly joint (typed FeaturePython)
  Activated = true
  AngleMax = 0
  AngleMin = 0
  Detach1 = false
  Detach2 = false
  Distance = 0
  Distance2 = 0
  EnableAngleMax = false
  EnableAngleMin = false
  EnableLengthMax = false
  EnableLengthMin = false
  JointType = 0 (Fixed)
  LengthMax = 0
  LengthMin = 0
  Offset2 = pos=(0,0,13) rot=(0,0,1;0rad)
  Placement1 = pos=(-0.325,8.9,0.325) rot=(-0.57735,-0.57735,0.57735;4.18879rad)
  Placement2 = pos=(0.325,-5.95,0.325) rot=(-0.57735,-0.57735,0.57735;4.18879rad)
  Reference1 = -> Assembly [Pin011.Part__Feature177.Edge9,Pin011.Part__Feature177.Vertex8]
  Reference2 = -> Assembly [Socket017.Part__Feature178.Face11,Socket017.Part__Feature178.Vertex52]
FEATURE [App::Link] Pin012  label="083_Pin012"
  LinkPlacement = pos=(128.5,18.07,-216.8) rot=(0.57735,-0.57735,-0.57735;2.0944rad)
  LinkedObject = -> Pin
  Placement = pos=(128.5,18.07,-216.8) rot=(0.57735,-0.57735,-0.57735;2.0944rad)
FEATURE [App::Link] Socket018  label="084_Socket018"
  LinkPlacement = pos=(128.5,18.07,-213.85) rot=(-0.57735,-0.57735,0.57735;2.0944rad)
  LinkedObject = -> Socket
  Placement = pos=(128.5,18.07,-213.85) rot=(-0.57735,-0.57735,0.57735;2.0944rad)
FEATURE [App::FeaturePython] Joint084  label="Fixed084"  # Assembly joint (typed FeaturePython)
  Activated = true
  AngleMax = 0
  AngleMin = 0
  Detach1 = false
  Detach2 = false
  Distance = 0
  Distance2 = 0
  EnableAngleMax = false
  EnableAngleMin = false
  EnableLengthMax = false
  EnableLengthMin = false
  JointType = 0 (Fixed)
  LengthMax = 0
  LengthMin = 0
  Placement1 = pos=(-18.15,2.5,21.5) rot=(-0.57735,-0.57735,0.57735;4.18879rad)
  Placement2 = pos=(0,-9.4,0) rot=(-0.57735,0.57735,0.57735;2.0944rad)
  Reference1 = -> Assembly [BreadBoard.Face18,BreadBoard.Face18]
  Reference2 = -> Assembly [Pin012.Part__Feature177.Face10,Pin012.Part__Feature177.Face10]
FEATURE [App::FeaturePython] Joint085  label="Fixed085"  # Assembly joint (typed FeaturePython)
  Activated = true
  AngleMax = 0
  AngleMin = 0
  Detach1 = false
  Detach2 = false
  Distance = 0
  Distance2 = 0
  EnableAngleMax = false
  EnableAngleMin = false
  EnableLengthMax = false
  EnableLengthMin = false
  JointType = 0 (Fixed)
  LengthMax = 0
  LengthMin = 0
  Offset2 = pos=(0,0,13) rot=(0,0,1;0rad)
  Placement1 = pos=(-0.325,8.9,0.325) rot=(-0.57735,-0.57735,0.57735;4.18879rad)
  Placement2 = pos=(0.325,-5.95,0.325) rot=(-0.57735,-0.57735,0.57735;4.18879rad)
  Reference1 = -> Assembly [Pin012.Part__Feature177.Edge9,Pin012.Part__Feature177.Vertex8]
  Reference2 = -> Assembly [Socket018.Part__Feature178.Face11,Socket018.Part__Feature178.Vertex52]
FEATURE [App::Link] Pin013  label="085_Pin013"
  LinkPlacement = pos=(128.5,20.57,-216.8) rot=(0.57735,0.57735,0.57735;2.0944rad)
  LinkedObject = -> Pin
  Placement = pos=(128.5,20.57,-216.8) rot=(0.57735,0.57735,0.57735;2.0944rad)
FEATURE [App::Link] Socket019  label="086_Socket019"
  LinkPlacement = pos=(128.5,20.57,-213.85) rot=(-0.57735,-0.57735,0.57735;2.0944rad)
  LinkedObject = -> Socket
  Placement = pos=(128.5,20.57,-213.85) rot=(-0.57735,-0.57735,0.57735;2.0944rad)
FEATURE [App::FeaturePython] Joint086  label="Fixed086"  # Assembly joint (typed FeaturePython)
  Activated = true
  AngleMax = 0
  AngleMin = 0
  Detach1 = false
  Detach2 = false
  Distance = 0
  Distance2 = 0
  EnableAngleMax = false
  EnableAngleMin = false
  EnableLengthMax = false
  EnableLengthMin = false
  JointType = 0 (Fixed)
  LengthMax = 0
  LengthMin = 0
  Placement1 = pos=(0,-9.4,0) rot=(-0.57735,0.57735,0.57735;2.0944rad)
  Placement2 = pos=(-20.65,2.5,21.5) rot=(-0.57735,-0.57735,-0.57735;2.0944rad)
  Reference1 = -> Assembly [Pin013.Part__Feature177.Face10,Pin013.Part__Feature177.Face10]
  Reference2 = -> Assembly [BreadBoard.Face8,BreadBoard.Face8]
FEATURE [App::FeaturePython] Joint087  label="Fixed087"  # Assembly joint (typed FeaturePython)
  Activated = true
  AngleMax = 0
  AngleMin = 0
  Detach1 = false
  Detach2 = false
  Distance = 0
  Distance2 = 0
  EnableAngleMax = false
  EnableAngleMin = false
  EnableLengthMax = false
  EnableLengthMin = false
  JointType = 0 (Fixed)
  LengthMax = 0
  LengthMin = 0
  Offset2 = pos=(0,0,13) rot=(0,0,1;3.14159rad)
  Placement1 = pos=(0.325,8.9,-0.325) rot=(-0.57735,-0.57735,0.57735;4.18879rad)
  Placement2 = pos=(0.325,-5.95,0.325) rot=(-0.57735,0.57735,-0.57735;4.18879rad)
  Reference1 = -> Assembly [Pin013.Part__Feature177.Edge2,Pin013.Part__Feature177.Vertex3]
  Reference2 = -> Assembly [Socket019.Part__Feature178.Face11,Socket019.Part__Feature178.Vertex52]
FEATURE [App::Link] Pin014  label="087_Pin014"
  LinkPlacement = pos=(126,25.57,-216.8) rot=(0.57735,-0.57735,-0.57735;2.0944rad)
  LinkedObject = -> Pin
  Placement = pos=(126,25.57,-216.8) rot=(0.57735,-0.57735,-0.57735;2.0944rad)
FEATURE [App::Link] Socket020  label="088_Socket020"
  LinkPlacement = pos=(126,25.57,-213.85) rot=(-0.57735,-0.57735,0.57735;2.0944rad)
  LinkedObject = -> Socket
  Placement = pos=(126,25.57,-213.85) rot=(-0.57735,-0.57735,0.57735;2.0944rad)
FEATURE [App::FeaturePython] Joint088  label="Fixed088"  # Assembly joint (typed FeaturePython)
  Activated = true
  AngleMax = 0
  AngleMin = 0
  Detach1 = false
  Detach2 = false
  Distance = 0
  Distance2 = 0
  EnableAngleMax = false
  EnableAngleMin = false
  EnableLengthMax = false
  EnableLengthMin = false
  JointType = 0 (Fixed)
  LengthMax = 0
  LengthMin = 0
  Placement1 = pos=(0,-9.4,0) rot=(-0.57735,0.57735,0.57735;2.0944rad)
  Placement2 = pos=(-25.65,2.5,24) rot=(-0.57735,-0.57735,0.57735;4.18879rad)
  Reference1 = -> Assembly [Pin014.Part__Feature177.Face10,Pin014.Part__Feature177.Face10]
  Reference2 = -> Assembly [BreadBoard.Face51,BreadBoard.Face51]
FEATURE [App::FeaturePython] Joint089  label="Fixed089"  # Assembly joint (typed FeaturePython)
  Activated = true
  AngleMax = 0
  AngleMin = 0
  Detach1 = false
  Detach2 = false
  Distance = 0
  Distance2 = 0
  EnableAngleMax = false
  EnableAngleMin = false
  EnableLengthMax = false
  EnableLengthMin = false
  JointType = 0 (Fixed)
  LengthMax = 0
  LengthMin = 0
  Offset2 = pos=(0,0,13) rot=(0,0,1;0rad)
  Placement1 = pos=(-0.325,8.9,0.325) rot=(-0.57735,-0.57735,0.57735;4.18879rad)
  Placement2 = pos=(0.325,-5.95,0.325) rot=(-0.57735,-0.57735,0.57735;4.18879rad)
  Reference1 = -> Assembly [Pin014.Part__Feature177.Edge9,Pin014.Part__Feature177.Vertex8]
  Reference2 = -> Assembly [Socket020.Part__Feature178.Face11,Socket020.Part__Feature178.Vertex52]
FEATURE [App::Link] Pin015  label="089_Pin015"
  LinkPlacement = pos=(98.5,-2.64766,-164.475) rot=(0,0,1;4.71239rad)
  LinkedObject = -> Pin
  Placement = pos=(98.5,-2.64766,-164.475) rot=(0,0,1;4.71239rad)
FEATURE [App::FeaturePython] Joint090  label="Fixed090"  # Assembly joint (typed FeaturePython)
  Activated = true
  AngleMax = 0
  AngleMin = 0
  Detach1 = false
  Detach2 = false
  Distance = 0
  Distance2 = 0
  EnableAngleMax = false
  EnableAngleMin = false
  EnableLengthMax = false
  EnableLengthMin = false
  JointType = 0 (Fixed)
  LengthMax = 0
  LengthMin = 0
  Offset2 = pos=(0,0,-9) rot=(0,0,1;3.14159rad)
  Placement1 = pos=(0.325,7.05,-0.325) rot=(0.57735,0.57735,0.57735;4.18879rad)
  Placement2 = pos=(0.325,0.1,-0.325) rot=(-0.57735,0.57735,-0.57735;4.18879rad)
  Reference1 = -> Assembly [Socket001.Part__Feature178.Edge10,Socket001.Part__Feature178.Vertex11]
  Reference2 = -> Assembly [Pin015.Part__Feature177.Edge2,Pin015.Part__Feature177.Vertex2]
FEATURE [App::Link] Socket021  label="090_Socket021"
  LinkPlacement = pos=(105.45,-2.64766,-164.475) rot=(0,0,-1;4.71239rad)
  LinkedObject = -> Socket
  Placement = pos=(105.45,-2.64766,-164.475) rot=(0,0,-1;4.71239rad)
FEATURE [App::FeaturePython] Joint091  label="Fixed091"  # Assembly joint (typed FeaturePython)
  Activated = true
  AngleMax = 0
  AngleMin = 0
  Detach1 = false
  Detach2 = false
  Distance = 0
  Distance2 = 0
  EnableAngleMax = false
  EnableAngleMin = false
  EnableLengthMax = false
  EnableLengthMin = false
  JointType = 0 (Fixed)
  LengthMax = 0
  LengthMin = 0
  Offset2 = pos=(0,0,9) rot=(0,0,1;0rad)
  Placement1 = pos=(-0.325,8.9,0.325) rot=(-0.57735,-0.57735,0.57735;4.18879rad)
  Placement2 = pos=(0.325,-1.95,0.325) rot=(-0.57735,-0.57735,0.57735;4.18879rad)
  Reference1 = -> Assembly [Pin015.Part__Feature177.Edge9,Pin015.Part__Feature177.Vertex8]
  Reference2 = -> Assembly [Socket021.Part__Feature178.Face11,Socket021.Part__Feature178.Vertex52]
FEATURE [App::Link] Pin016  label="091_Pin016"
  LinkPlacement = pos=(98.5,-0.447661,-164.475) rot=(0,0,1;4.71239rad)
  LinkedObject = -> Pin
  Placement = pos=(98.5,-0.447661,-164.475) rot=(0,0,1;4.71239rad)
FEATURE [App::Link] Socket022  label="092_Socket022"
  LinkPlacement = pos=(105.45,-0.447661,-164.475) rot=(0,0,-1;4.71239rad)
  LinkedObject = -> Socket
  Placement = pos=(105.45,-0.447661,-164.475) rot=(0,0,-1;4.71239rad)
FEATURE [App::FeaturePython] Joint092  label="Fixed092"  # Assembly joint (typed FeaturePython)
  Activated = true
  AngleMax = 0
  AngleMin = 0
  Detach1 = false
  Detach2 = false
  Distance = 0
  Distance2 = 0
  EnableAngleMax = false
  EnableAngleMin = false
  EnableLengthMax = false
  EnableLengthMin = false
  JointType = 0 (Fixed)
  LengthMax = 0
  LengthMin = 0
  Offset2 = pos=(0,0,-9) rot=(0,0,1;0rad)
  Placement1 = pos=(-0.325,7.05,0.325) rot=(-0.57735,-0.57735,0.57735;4.18879rad)
  Placement2 = pos=(-0.325,0.1,0.325) rot=(-0.57735,-0.57735,0.57735;4.18879rad)
  Reference1 = -> Assembly [Socket002.Part__Feature178.Face11,Socket002.Part__Feature178.Vertex51]
  Reference2 = -> Assembly [Pin016.Part__Feature177.Edge9,Pin016.Part__Feature177.Vertex7]
FEATURE [App::FeaturePython] Joint093  label="Fixed093"  # Assembly joint (typed FeaturePython)
  Activated = true
  AngleMax = 0
  AngleMin = 0
  Detach1 = false
  Detach2 = false
  Distance = 0
  Distance2 = 0
  EnableAngleMax = false
  EnableAngleMin = false
  EnableLengthMax = false
  EnableLengthMin = false
  JointType = 0 (Fixed)
  LengthMax = 0
  LengthMin = 0
  Offset2 = pos=(0,0,9) rot=(0,0,1;0rad)
  Placement1 = pos=(-0.325,8.9,0.325) rot=(-0.57735,-0.57735,0.57735;4.18879rad)
  Placement2 = pos=(0.325,-1.95,0.325) rot=(-0.57735,-0.57735,0.57735;4.18879rad)
  Reference1 = -> Assembly [Pin016.Part__Feature177.Edge9,Pin016.Part__Feature177.Vertex8]
  Reference2 = -> Assembly [Socket022.Part__Feature178.Face11,Socket022.Part__Feature178.Vertex52]
FEATURE [App::Link] Pin017  label="093_Pin017"
  LinkPlacement = pos=(98.5,1.75234,-164.475) rot=(0,0,1;4.71239rad)
  LinkedObject = -> Pin
  Placement = pos=(98.5,1.75234,-164.475) rot=(0,0,1;4.71239rad)
FEATURE [App::Link] Socket023  label="094_Socket023"
  LinkPlacement = pos=(105.45,1.75234,-164.475) rot=(0,0,-1;4.71239rad)
  LinkedObject = -> Socket
  Placement = pos=(105.45,1.75234,-164.475) rot=(0,0,-1;4.71239rad)
FEATURE [App::FeaturePython] Joint094  label="Fixed094"  # Assembly joint (typed FeaturePython)
  Activated = true
  AngleMax = 0
  AngleMin = 0
  Detach1 = false
  Detach2 = false
  Distance = 0
  Distance2 = 0
  EnableAngleMax = false
  EnableAngleMin = false
  EnableLengthMax = false
  EnableLengthMin = false
  JointType = 0 (Fixed)
  LengthMax = 0
  LengthMin = 0
  Offset2 = pos=(0,0,9) rot=(0,0,1;0rad)
  Placement1 = pos=(-0.325,-8.9,0.325) rot=(-0.57735,-0.57735,0.57735;4.18879rad)
  Placement2 = pos=(-0.325,-1.95,0.325) rot=(-0.57735,-0.57735,0.57735;4.18879rad)
  Reference1 = -> Assembly [Pin017.Part__Feature177.Edge9,Pin017.Part__Feature177.Vertex7]
  Reference2 = -> Assembly [Socket003.Part__Feature178.Face11,Socket003.Part__Feature178.Vertex51]
FEATURE [App::FeaturePython] Joint095  label="Fixed095"  # Assembly joint (typed FeaturePython)
  Activated = true
  AngleMax = 0
  AngleMin = 0
  Detach1 = false
  Detach2 = false
  Distance = 0
  Distance2 = 0
  EnableAngleMax = false
  EnableAngleMin = false
  EnableLengthMax = false
  EnableLengthMin = false
  JointType = 0 (Fixed)
  LengthMax = 0
  LengthMin = 0
  Offset2 = pos=(0,0,9) rot=(0,0,1;0rad)
  Placement1 = pos=(-0.325,8.9,0.325) rot=(-0.57735,-0.57735,0.57735;4.18879rad)
  Placement2 = pos=(0.325,-1.95,0.325) rot=(-0.57735,-0.57735,0.57735;4.18879rad)
  Reference1 = -> Assembly [Pin017.Part__Feature177.Edge9,Pin017.Part__Feature177.Vertex8]
  Reference2 = -> Assembly [Socket023.Part__Feature178.Face11,Socket023.Part__Feature178.Vertex52]
FEATURE [App::Link] Pin018  label="095_Pin018"
  LinkPlacement = pos=(57.475,-78.4,18.825) rot=(0,0,1;3.14159rad)
  LinkedObject = -> Pin
  Placement = pos=(57.475,-78.4,18.825) rot=(0,0,1;3.14159rad)
FEATURE [App::Link] Socket024  label="096_Socket024"
  LinkPlacement = pos=(57.475,-85.35,18.825) rot=(0,0,1;0rad)
  LinkedObject = -> Socket
  Placement = pos=(57.475,-85.35,18.825) rot=(0,0,1;0rad)
FEATURE [App::FeaturePython] Joint096  label="Fixed096"  # Assembly joint (typed FeaturePython)
  Activated = true
  AngleMax = 0
  AngleMin = 0
  Detach1 = false
  Detach2 = false
  Distance = 0
  Distance2 = 0
  EnableAngleMax = false
  EnableAngleMin = false
  EnableLengthMax = false
  EnableLengthMin = false
  JointType = 0 (Fixed)
  LengthMax = 0
  LengthMin = 0
  Offset2 = pos=(0,0,9) rot=(0,0,1;0rad)
  Placement1 = pos=(-0.325,-8.9,0.325) rot=(-0.57735,-0.57735,0.57735;4.18879rad)
  Placement2 = pos=(-0.325,-1.95,0.325) rot=(-0.57735,-0.57735,0.57735;4.18879rad)
  Reference1 = -> Assembly [Pin018.Part__Feature177.Edge9,Pin018.Part__Feature177.Vertex7]
  Reference2 = -> Assembly [Socket004.Part__Feature178.Face11,Socket004.Part__Feature178.Vertex51]
FEATURE [App::FeaturePython] Joint097  label="Fixed097"  # Assembly joint (typed FeaturePython)
  Activated = true
  AngleMax = 0
  AngleMin = 0
  Detach1 = false
  Detach2 = false
  Distance = 0
  Distance2 = 0
  EnableAngleMax = false
  EnableAngleMin = false
  EnableLengthMax = false
  EnableLengthMin = false
  JointType = 0 (Fixed)
  LengthMax = 0
  LengthMin = 0
  Offset2 = pos=(0,0,9) rot=(0,0,1;0rad)
  Placement1 = pos=(-0.325,8.9,0.325) rot=(-0.57735,-0.57735,0.57735;4.18879rad)
  Placement2 = pos=(0.325,-1.95,0.325) rot=(-0.57735,-0.57735,0.57735;4.18879rad)
  Reference1 = -> Assembly [Pin018.Part__Feature177.Edge9,Pin018.Part__Feature177.Vertex8]
  Reference2 = -> Assembly [Socket024.Part__Feature178.Face11,Socket024.Part__Feature178.Vertex52]
FEATURE [App::Link] Pin019  label="097_Pin019"
  LinkPlacement = pos=(59.675,-78.4,18.825) rot=(0,0,1;3.14159rad)
  LinkedObject = -> Pin
  Placement = pos=(59.675,-78.4,18.825) rot=(0,0,1;3.14159rad)
FEATURE [App::Link] Socket025  label="098_Socket025"
  LinkPlacement = pos=(59.675,-85.35,18.825) rot=(0,0,1;0rad)
  LinkedObject = -> Socket
  Placement = pos=(59.675,-85.35,18.825) rot=(0,0,1;0rad)
FEATURE [App::FeaturePython] Joint098  label="Fixed098"  # Assembly joint (typed FeaturePython)
  Activated = true
  AngleMax = 0
  AngleMin = 0
  Detach1 = false
  Detach2 = false
  Distance = 0
  Distance2 = 0
  EnableAngleMax = false
  EnableAngleMin = false
  EnableLengthMax = false
  EnableLengthMin = false
  JointType = 0 (Fixed)
  LengthMax = 0
  LengthMin = 0
  Offset2 = pos=(0,0,9) rot=(0,0,1;0rad)
  Placement1 = pos=(-0.325,-8.9,0.325) rot=(-0.57735,-0.57735,0.57735;4.18879rad)
  Placement2 = pos=(-0.325,-1.95,0.325) rot=(-0.57735,-0.57735,0.57735;4.18879rad)
  Reference1 = -> Assembly [Pin019.Part__Feature177.Edge9,Pin019.Part__Feature177.Vertex7]
  Reference2 = -> Assembly [Socket005.Part__Feature178.Face11,Socket005.Part__Feature178.Vertex51]
FEATURE [App::FeaturePython] Joint099  label="Fixed099"  # Assembly joint (typed FeaturePython)
  Activated = true
  AngleMax = 0
  AngleMin = 0
  Detach1 = false
  Detach2 = false
  Distance = 0
  Distance2 = 0
  EnableAngleMax = false
  EnableAngleMin = false
  EnableLengthMax = false
  EnableLengthMin = false
  JointType = 0 (Fixed)
  LengthMax = 0
  LengthMin = 0
  Offset2 = pos=(0,0,9) rot=(0,0,1;0rad)
  Placement1 = pos=(-0.325,8.9,0.325) rot=(-0.57735,-0.57735,0.57735;4.18879rad)
  Placement2 = pos=(0.325,-1.95,0.325) rot=(-0.57735,-0.57735,0.57735;4.18879rad)
  Reference1 = -> Assembly [Pin019.Part__Feature177.Edge9,Pin019.Part__Feature177.Vertex8]
  Reference2 = -> Assembly [Socket025.Part__Feature178.Face11,Socket025.Part__Feature178.Vertex52]
FEATURE [App::Link] Pin020  label="099_Pin020"
  LinkPlacement = pos=(61.875,-78.4,18.825) rot=(0,0,1;3.14159rad)
  LinkedObject = -> Pin
  Placement = pos=(61.875,-78.4,18.825) rot=(0,0,1;3.14159rad)
FEATURE [App::Link] Socket026  label="100_Socket026"
  LinkPlacement = pos=(61.875,-85.35,18.825) rot=(0,0,1;0rad)
  LinkedObject = -> Socket
  Placement = pos=(61.875,-85.35,18.825) rot=(0,0,1;0rad)
FEATURE [App::FeaturePython] Joint100  label="Fixed100"  # Assembly joint (typed FeaturePython)
  Activated = true
  AngleMax = 0
  AngleMin = 0
  Detach1 = false
  Detach2 = false
  Distance = 0
  Distance2 = 0
  EnableAngleMax = false
  EnableAngleMin = false
  EnableLengthMax = false
  EnableLengthMin = false
  JointType = 0 (Fixed)
  LengthMax = 0
  LengthMin = 0
  Offset2 = pos=(0,0,9) rot=(0,0,1;0rad)
  Placement1 = pos=(-0.325,-8.9,0.325) rot=(-0.57735,-0.57735,0.57735;4.18879rad)
  Placement2 = pos=(-0.325,-1.95,0.325) rot=(-0.57735,-0.57735,0.57735;4.18879rad)
  Reference1 = -> Assembly [Pin020.Part__Feature177.Edge9,Pin020.Part__Feature177.Vertex7]
  Reference2 = -> Assembly [Socket006.Part__Feature178.Face11,Socket006.Part__Feature178.Vertex51]
FEATURE [App::FeaturePython] Joint101  label="Fixed101"  # Assembly joint (typed FeaturePython)
  Activated = true
  AngleMax = 0
  AngleMin = 0
  Detach1 = false
  Detach2 = false
  Distance = 0
  Distance2 = 0
  EnableAngleMax = false
  EnableAngleMin = false
  EnableLengthMax = false
  EnableLengthMin = false
  JointType = 0 (Fixed)
  LengthMax = 0
  LengthMin = 0
  Offset2 = pos=(0,0,9) rot=(0,0,1;0rad)
  Placement1 = pos=(-0.325,8.9,0.325) rot=(-0.57735,-0.57735,0.57735;4.18879rad)
  Placement2 = pos=(0.325,-1.95,0.325) rot=(-0.57735,-0.57735,0.57735;4.18879rad)
  Reference1 = -> Assembly [Pin020.Part__Feature177.Edge9,Pin020.Part__Feature177.Vertex8]
  Reference2 = -> Assembly [Socket026.Part__Feature178.Face11,Socket026.Part__Feature178.Vertex52]
FEATURE [App::Link] Socket027  label="101_Socket027"
  LinkPlacement = pos=(38.2608,7.425,-42.005) rot=(0,0,1;1.5708rad)
  LinkedObject = -> Socket
  Placement = pos=(38.2608,7.425,-42.005) rot=(0,0,1;1.5708rad)
FEATURE [App::Link] Socket028  label="102_Socket028"
  LinkPlacement = pos=(38.2608,4.885,-42.005) rot=(0,0,1;1.5708rad)
  LinkedObject = -> Socket
  Placement = pos=(38.2608,4.885,-42.005) rot=(0,0,1;1.5708rad)
FEATURE [App::Link] Socket029  label="103_Socket029"
  LinkPlacement = pos=(38.2608,-0.195,-42.005) rot=(0,0,1;1.5708rad)
  LinkedObject = -> Socket
  Placement = pos=(38.2608,-0.195,-42.005) rot=(0,0,1;1.5708rad)
FEATURE [App::Link] Socket030  label="104_Socket030"
  LinkPlacement = pos=(38.2608,-2.735,-42.005) rot=(0,0,1;1.5708rad)
  LinkedObject = -> Socket
  Placement = pos=(38.2608,-2.735,-42.005) rot=(0,0,1;1.5708rad)
FEATURE [App::FeaturePython] Joint102  label="Fixed102"  # Assembly joint (typed FeaturePython)
  Activated = true
  AngleMax = 0
  AngleMin = 0
  Detach1 = false
  Detach2 = false
  Distance = 0
  Distance2 = 0
  EnableAngleMax = false
  EnableAngleMin = false
  EnableLengthMax = false
  EnableLengthMin = false
  JointType = 0 (Fixed)
  LengthMax = 0
  LengthMin = 0
  Offset2 = pos=(0,0,7) rot=(0,0,1;3.14159rad)
  Placement1 = pos=(-0.325,7.05,0.325) rot=(-0.57735,-0.57735,0.57735;4.18879rad)
  Placement2 = pos=(14.92,2.97287,-0.32) rot=(-0.57735,0.57735,-0.57735;4.18879rad)
  Reference1 = -> Assembly [Socket027.Part__Feature178.Face11,Socket027.Part__Feature178.Vertex51]
  Reference2 = -> Assembly [_x7_Male_Pin_Header008.Part__Feature120.Edge9,_x7_Male_Pin_Header008.Part__Feature120.Vertex8]
FEATURE [App::FeaturePython] Joint103  label="Fixed103"  # Assembly joint (typed FeaturePython)
  Activated = true
  AngleMax = 0
  AngleMin = 0
  Detach1 = false
  Detach2 = false
  Distance = 0
  Distance2 = 0
  EnableAngleMax = false
  EnableAngleMin = false
  EnableLengthMax = false
  EnableLengthMin = false
  JointType = 0 (Fixed)
  LengthMax = 0
  LengthMin = 0
  Offset2 = pos=(0,0,7) rot=(0,0,1;3.14159rad)
  Placement1 = pos=(-0.325,7.05,0.325) rot=(-0.57735,-0.57735,0.57735;4.18879rad)
  Placement2 = pos=(12.38,2.97287,-0.32) rot=(-0.57735,0.57735,-0.57735;4.18879rad)
  Reference1 = -> Assembly [Socket028.Part__Feature178.Face11,Socket028.Part__Feature178.Vertex51]
  Reference2 = -> Assembly [_x7_Male_Pin_Header008.Part__Feature119.Edge9,_x7_Male_Pin_Header008.Part__Feature119.Vertex8]
FEATURE [App::FeaturePython] Joint104  label="Fixed104"  # Assembly joint (typed FeaturePython)
  Activated = true
  AngleMax = 0
  AngleMin = 0
  Detach1 = false
  Detach2 = false
  Distance = 0
  Distance2 = 0
  EnableAngleMax = false
  EnableAngleMin = false
  EnableLengthMax = false
  EnableLengthMin = false
  JointType = 0 (Fixed)
  LengthMax = 0
  LengthMin = 0
  Offset2 = pos=(0,0,7) rot=(0,0,1;3.14159rad)
  Placement1 = pos=(7.3,9.97287,-0.32) rot=(-0.57735,-0.57735,0.57735;4.18879rad)
  Placement2 = pos=(-0.325,0.05,0.325) rot=(-0.57735,0.57735,-0.57735;4.18879rad)
  Reference1 = -> Assembly [_x7_Male_Pin_Header008.Part__Feature117.Edge9,_x7_Male_Pin_Header008.Part__Feature117.Vertex8]
  Reference2 = -> Assembly [Socket029.Part__Feature178.Face11,Socket029.Part__Feature178.Vertex51]
FEATURE [App::FeaturePython] Joint105  label="Fixed105"  # Assembly joint (typed FeaturePython)
  Activated = true
  AngleMax = 0
  AngleMin = 0
  Detach1 = false
  Detach2 = false
  Distance = 0
  Distance2 = 0
  EnableAngleMax = false
  EnableAngleMin = false
  EnableLengthMax = false
  EnableLengthMin = false
  JointType = 0 (Fixed)
  LengthMax = 0
  LengthMin = 0
  Offset2 = pos=(0,0,7) rot=(0,0,1;3.14159rad)
  Placement1 = pos=(4.76,9.97287,-0.32) rot=(-0.57735,-0.57735,0.57735;4.18879rad)
  Placement2 = pos=(-0.325,0.05,0.325) rot=(-0.57735,0.57735,-0.57735;4.18879rad)
  Reference1 = -> Assembly [_x7_Male_Pin_Header008.Part__Feature116.Edge9,_x7_Male_Pin_Header008.Part__Feature116.Vertex8]
  Reference2 = -> Assembly [Socket030.Part__Feature178.Face11,Socket030.Part__Feature178.Vertex51]
FEATURE [Assembly::JointGroup] Joints
  Group = -> [GroundedJoint,Joint,Joint001,Joint002,Joint003,Joint004,Joint005,Joint006,Joint007,Joint008,Joint009,Joint010,Joint011,Joint012,Joint013,Joint014,Joint015,Joint016,Joint017,Joint018,Joint019,Joint020,Joint021,Joint022,Joint023,Joint024,Joint025,Joint026,Joint027,Joint028,Joint029,Joint030,Joint033,Joint034,Joint035,Joint036,Joint037,Joint038,Joint039,Joint040,Joint041,Joint042,Joint043,Joint044,+61 more]
FEATURE [Assembly::AssemblyObject] Assembly
  Group = -> [Joints,Body011,GroundedJoint,ring_spacer,Joint,_3x3_8in_Screw,_3x3_8in_Screw001,_3x3_8in_Screw002,Joint001,Joint002,Joint003,second_layer,Joint004,color_sensor_layer,Joint005,color_sensor,_x7_Male_Pin_Header008,_3x3_8in_Screw003,_3x3_8in_Screw004,_3x3_8in_Screw005,Joint006,Joint007,Joint008,Joint009,Joint010,_3x3_8in_Screw006,Joint011,first_layer,Joint012,shaft,M90S_ali001,Joint013,Joint014,+177 more]
  Origin = -> Origin016
  Type = Assembly

RESOLVED EXTERNAL PARTS (link-assembly join: the EXTERNAL_REF files above that resolve inside this repo's crawl, each included once):
---- part Pipe.FCStd = doc fcstd_39bdbda56d1d ----
FCSTD DOCUMENT  (FreeCAD 1.0R38641 +678 (Git))
Label: Pipe
License: All rights reserved
LicenseURL: https://en.wikipedia.org/wiki/All_rights_reserved
objects: Sketcher::SketchObject×4, PartDesign::Plane×3, PartDesign::Pocket×3, PartDesign::Pad×1, PartDesign::Body×1, App::VarSet×1
note: 24 computed .brp shape members not serialized (recipe doc carries the construction recipe); baked Part::Feature solids carry a one-line shape summary decoded from their .brp

FEATURE [Sketcher::SketchObject] Sketch
  ArcFitTolerance = 1e-06
  AttachmentSupport = -> [XY_Plane]
  FullyConstrained = true
  MakeInternals = false
  MapMode = 5
  expr: Constraints[0] = VarSet.pipe_ID
  expr: Constraints[2] = VarSet.pipe_OD
  sketch-geometry (2):
    g0: Circle CenterX=0 CenterY=0 CenterZ=0 NormalX=0 NormalY=0 NormalZ=1 AngleXU=0 Radius=42.665
    g1: Circle CenterX=0 CenterY=0 CenterZ=0 NormalX=0 NormalY=0 NormalZ=1 AngleXU=0 Radius=45.32
  constraints (4):
    c: Diameter(g0) = 85.33
    c: Coincident(g0,g-1)
    c: Diameter(g1) = 90.64
    c: Coincident(g1,g0)
FEATURE [PartDesign::Pad] Pad
  Direction = (0,0,1)
  Length = 60
  Length2 = 10
  Profile = -> Sketch
  ReferenceAxis = -> Sketch [N_Axis]
  Refine = true
  Suppressed = false
  Type = 0
FEATURE [PartDesign::Plane] DatumPlane
  AttachmentOffset = pos=(0,-45.32,0) rot=(-1,0,0;1.5708rad)
  AttachmentSupport = -> [Pad]
  Length = 63.0384
  MapMode = 11
  Placement = pos=(45.32,-1.01e-14,60) rot=(-0.57735,-0.57735,0.57735;2.0944rad)
  ResizeMode = 0
  Width = 98.0384
  expr: .AttachmentOffset.Base.y = VarSet.pipe_OD / 2 * -1
FEATURE [Sketcher::SketchObject] Sketch002
  ArcFitTolerance = 1e-06
  AttachmentSupport = -> [DatumPlane]
  FullyConstrained = true
  MakeInternals = false
  MapMode = 5
  Placement = pos=(45.32,-1.01e-14,60) rot=(0.57735,0.57735,-0.57735;4.18879rad)
  sketch-geometry (15):
    g0: Circle CenterX=0 CenterY=3.8 CenterZ=0 NormalX=0 NormalY=0 NormalZ=1 AngleXU=0 Radius=1.5
    g1: LineSegment StartX=6e-16 StartY=47.6 StartZ=0 EndX=0.0005 EndY=47.6 EndZ=0
    g2: LineSegment StartX=1.5 StartY=49.0995 StartZ=0 EndX=1.5 EndY=52.1005 EndZ=0
    g3: LineSegment StartX=0.0005 StartY=53.6 StartZ=0 EndX=1.1e-15 EndY=53.6 EndZ=0
    g4: LineSegment StartX=-1.5 StartY=52.1 StartZ=0 EndX=-1.5 EndY=49.1 EndZ=0
    g5: GeomPoint [constr] X=0 Y=50.6 Z=0
    g6: ArcOfCircle CenterX=1e-15 CenterY=52.1 CenterZ=0 NormalX=0 NormalY=0 NormalZ=1 AngleXU=0 Radius=1.5 StartAngle=1.5708 EndAngle=3.14159
    g7: GeomPoint [constr] X=-1.5 Y=53.6 Z=0
    g8: ArcOfCircle CenterX=0.0005 CenterY=52.1005 CenterZ=0 NormalX=0 NormalY=0 NormalZ=1 AngleXU=0 Radius=1.4995 StartAngle=0 EndAngle=1.5708
    g9: GeomPoint [constr] X=1.5 Y=53.6 Z=0
    g10: ArcOfCircle CenterX=0.0005 CenterY=49.0995 CenterZ=0 NormalX=0 NormalY=0 NormalZ=1 AngleXU=0 Radius=1.4995 StartAngle=4.71239 EndAngle=6.28319
    g11: GeomPoint [constr] X=1.5 Y=47.6 Z=0
    g12: ArcOfCircle CenterX=9e-16 CenterY=49.1 CenterZ=0 NormalX=0 NormalY=0 NormalZ=1 AngleXU=0 Radius=1.5 StartAngle=3.14159 EndAngle=4.71239
    g13: GeomPoint [constr] X=-1.5 Y=47.6 Z=0
    g14: Circle CenterX=0 CenterY=18 CenterZ=0 NormalX=0 NormalY=0 NormalZ=1 AngleXU=0 Radius=10
  constraints (35):
    c: Diameter(g0) = 3
    c: PointOnObject(g0,g-2)
    c: DistanceY(g-1,g0) = 3.8
    c: Horizontal(g1)
    c: Horizontal(g3)
    c: Vertical(g2)
    c: Vertical(g4)
    c: Symmetric(g9,g13,g5)
    c: Distance(g11,g13) = 3
    c: Distance(g13,g7) = 6
    c: PointOnObject(g5,g-2)
    c: PointOnObject(g7,g4)
    c: PointOnObject(g7,g3)
    c: Tangent(g4,g6) = -1.5708
    c: Tangent(g3,g6) = -1.5708
    c: PointOnObject(g9,g2)
    c: PointOnObject(g9,g3)
    c: Tangent(g2,g8) = -1.5708
    c: Tangent(g3,g8) = -1.5708
    c: PointOnObject(g11,g2)
    c: PointOnObject(g11,g1)
    c: Tangent(g2,g10) = -1.5708
    c: Tangent(g1,g10) = -1.5708
    c: PointOnObject(g13,g4)
    c: PointOnObject(g13,g1)
    c: Tangent(g4,g12) = -1.5708
    c: Tangent(g1,g12) = -1.5708
    c: Diameter(g6) = 3
    c: Diameter(g8) = 2.999
    c: Diameter(g10) = 2.999
    c: Diameter(g12) = 3
    c: DistanceY(g-1,g5) = 50.6
    c: Diameter(g14) = 20
    c: PointOnObject(g14,g-2)
    c: DistanceY(g-1,g14) = 18
FEATURE [PartDesign::Pocket] Pocket
  BaseFeature = -> Pad
  Direction = (1,0,0)
  Length = 8
  Length2 = 5
  Profile = -> Sketch002
  ReferenceAxis = -> Sketch002 [N_Axis]
  Refine = true
  Reversed = true
  Suppressed = false
  Type = 0
FEATURE [PartDesign::Plane] DatumPlane001
  AttachmentOffset = pos=(45.32,0,0) rot=(0,1,0;1.5708rad)
  AttachmentSupport = -> [Pocket]
  Length = 98.0384
  MapMode = 11
  Placement = pos=(1.01e-14,45.32,60) rot=(-0.57735,0.57735,0.57735;2.0944rad)
  ResizeMode = 0
  Width = 63.0384
  expr: .AttachmentOffset.Base.x = VarSet.pipe_OD / 2
FEATURE [Sketcher::SketchObject] Sketch003
  ArcFitTolerance = 1e-06
  AttachmentSupport = -> [DatumPlane001]
  ExternalGeometry = -> [Pocket]
  FullyConstrained = true
  MakeInternals = false
  MapMode = 5
  Placement = pos=(1.01e-14,45.32,60) rot=(0.57735,-0.57735,-0.57735;4.18879rad)
  sketch-geometry (2):
    g0: Circle CenterX=3.8 CenterY=0 CenterZ=0 NormalX=0 NormalY=0 NormalZ=1 AngleXU=0 Radius=1.5
    g1: Circle CenterX=24.8 CenterY=0 CenterZ=0 NormalX=0 NormalY=0 NormalZ=1 AngleXU=0 Radius=1.5
  constraints (8):
    c: Diameter(g0) = 3
    c: PointOnObject(g0,g-1)
    c: Diameter(g1) = 3
    c: PointOnObject(g1,g-1)
    c: DistanceX(g-1,g0) = 3.8
    c: DistanceX(g-1,g1) = 24.8
    c: DistanceX(g-3,g-3) = 0
    c: DistanceX(g-3,g-3) = 0
FEATURE [PartDesign::Pocket] Pocket001
  BaseFeature = -> Pocket
  Direction = (0,-1,0)
  Length = 8
  Length2 = 5
  Profile = -> Sketch003
  ReferenceAxis = -> Sketch003 [N_Axis]
  Refine = true
  Suppressed = false
  Type = 0
FEATURE [PartDesign::Plane] DatumPlane002
  AttachmentOffset = pos=(-45.32,0,0) rot=(0,-1,0;1.5708rad)
  AttachmentSupport = -> [Pocket001]
  Length = 98.0384
  MapMode = 11
  Placement = pos=(-1.01e-14,-45.32,60) rot=(0.57735,-0.57735,0.57735;2.0944rad)
  ResizeMode = 0
  Width = 63.0384
  expr: .AttachmentOffset.Base.x = VarSet.pipe_OD / 2 * -1
FEATURE [Sketcher::SketchObject] Sketch004
  ArcFitTolerance = 1e-06
  AttachmentSupport = -> [DatumPlane002]
  ExternalGeometry = -> [Pocket001]
  FullyConstrained = true
  MakeInternals = false
  MapMode = 5
  Placement = pos=(-1.01e-14,-45.32,60) rot=(0.57735,-0.57735,0.57735;2.0944rad)
  sketch-geometry (15):
    g0: Circle CenterX=-3.8 CenterY=0 CenterZ=0 NormalX=0 NormalY=0 NormalZ=1 AngleXU=0 Radius=1.5
    g1: Circle CenterX=-24.8 CenterY=0 CenterZ=0 NormalX=0 NormalY=0 NormalZ=1 AngleXU=0 Radius=1.5
    g2: LineSegment StartX=-52.1 StartY=-1.5 StartZ=0 EndX=-49.095 EndY=-1.5 EndZ=0
    g3: LineSegment StartX=-47.6 StartY=-0.005 StartZ=0 EndX=-47.6 EndY=-7e-16 EndZ=0
    g4: LineSegment StartX=-49.1 StartY=1.5 StartZ=0 EndX=-52.105 EndY=1.5 EndZ=0
    g5: LineSegment StartX=-53.6 StartY=0.005 StartZ=0 EndX=-53.6 EndY=-2e-16 EndZ=0
    g6: GeomPoint [constr] X=-50.6 Y=0 Z=0
    g7: ArcOfCircle CenterX=-52.1 CenterY=-4e-16 CenterZ=0 NormalX=0 NormalY=0 NormalZ=1 AngleXU=0 Radius=1.5 StartAngle=3.14159 EndAngle=4.71239
    g8: GeomPoint [constr] X=-53.6 Y=-1.5 Z=0
    g9: ArcOfCircle CenterX=-52.105 CenterY=0.005 CenterZ=0 NormalX=0 NormalY=0 NormalZ=1 AngleXU=0 Radius=1.495 StartAngle=1.5708 EndAngle=3.14159
    g10: GeomPoint [constr] X=-53.6 Y=1.5 Z=0
    g11: ArcOfCircle CenterX=-49.1 CenterY=-7e-16 CenterZ=0 NormalX=0 NormalY=0 NormalZ=1 AngleXU=0 Radius=1.5 StartAngle=0 EndAngle=1.5708
    g12: GeomPoint [constr] X=-47.6 Y=1.5 Z=0
    g13: ArcOfCircle CenterX=-49.095 CenterY=-0.005 CenterZ=0 NormalX=0 NormalY=0 NormalZ=1 AngleXU=0 Radius=1.495 StartAngle=4.71239 EndAngle=6.28319
    g14: GeomPoint [constr] X=-47.6 Y=-1.5 Z=0
  constraints (35):
    c: Diameter(g0) = 3
    c: PointOnObject(g0,g-1)
    c: Distance(g-1,g0) = 3.8
    c: Diameter(g1) = 3
    c: PointOnObject(g1,g-1)
    c: Distance(g1,g-1) = 24.8
    c: Horizontal(g2)
    c: Horizontal(g4)
    c: Vertical(g3)
    c: Vertical(g5)
    c: Symmetric(g12,g8,g6)
    c: Distance(g14,g8) = 6
    c: Distance(g8,g10) = 3
    c: PointOnObject(g6,g-1)
    c: PointOnObject(g8,g2)
    c: PointOnObject(g8,g5)
    c: Tangent(g2,g7) = -1.5708
    c: Tangent(g5,g7) = -1.5708
    c: PointOnObject(g10,g4)
    c: PointOnObject(g10,g5)
    c: Tangent(g4,g9) = -1.5708
    c: Tangent(g5,g9) = -1.5708
    c: PointOnObject(g12,g4)
    c: PointOnObject(g12,g3)
    c: Tangent(g4,g11) = -1.5708
    c: Tangent(g3,g11) = -1.5708
    c: PointOnObject(g14,g3)
    c: PointOnObject(g14,g2)
    c: Tangent(g3,g13) = -1.5708
    c: Tangent(g2,g13) = -1.5708
    c: Diameter(g7) = 3
    c: Diameter(g9) = 2.99
    c: Diameter(g11) = 3
    c: Diameter(g13) = 2.99
    c: DistanceX(g6,g-1) = 50.6
FEATURE [PartDesign::Pocket] Pocket002
  BaseFeature = -> Pocket001
  Direction = (0,1,0)
  Length = 5
  Length2 = 5
  Profile = -> Sketch004
  ReferenceAxis = -> Sketch004 [N_Axis]
  Refine = true
  Suppressed = false
  Type = 0
FEATURE [PartDesign::Body] Body
  AllowCompound = false
  Group = -> [Sketch,Pad,DatumPlane,Sketch002,Pocket,DatumPlane001,Sketch003,Pocket001,DatumPlane002,Sketch004,Pocket002]
  Origin = -> Origin
  Placement = pos=(0,0,0) rot=(1,0,0;3.14159rad)
  Tip = -> Pocket002
FEATURE [App::VarSet] VarSet
  pipe_ID = 85.33
  pipe_OD = 90.64
---- part Slide.FCStd = doc fcstd_13b7b13e91a8 ----
FCSTD DOCUMENT  (FreeCAD 1.0R38641 +678 (Git))
Label: Slide
License: All rights reserved
LicenseURL: https://en.wikipedia.org/wiki/All_rights_reserved
objects: Sketcher::SketchObject×2, PartDesign::Pad×1, PartDesign::Thickness×1, PartDesign::Pocket×1, PartDesign::Fillet×1, PartDesign::Body×1
note: 17 computed .brp shape members not serialized (recipe doc carries the construction recipe); baked Part::Feature solids carry a one-line shape summary decoded from their .brp

FEATURE [Sketcher::SketchObject] Sketch
  ArcFitTolerance = 1e-06
  AttachmentSupport = -> [XY_Plane]
  FullyConstrained = true
  MakeInternals = false
  MapMode = 5
  sketch-geometry (11):
    g0: LineSegment StartX=-64.9169 StartY=-10 StartZ=0 EndX=4.58312 EndY=-10 EndZ=0
    g1: LineSegment StartX=9.58312 StartY=-5 StartZ=0 EndX=9.58312 EndY=5 EndZ=0
    g2: LineSegment StartX=4.58312 StartY=10 StartZ=0 EndX=-64.9169 EndY=10 EndZ=0
    g3: GeomPoint [constr] X=0 Y=0 Z=0
    g4: ArcOfCircle CenterX=-81.5 CenterY=0 CenterZ=0 NormalX=0 NormalY=0 NormalZ=1 AngleXU=0 Radius=15 StartAngle=0.985111 EndAngle=5.29807
    g5: ArcOfCircle CenterX=-64.9169 CenterY=-25 CenterZ=0 NormalX=0 NormalY=0 NormalZ=1 AngleXU=0 Radius=15 StartAngle=1.5708 EndAngle=2.15648
    g6: ArcOfCircle CenterX=-64.9169 CenterY=25 CenterZ=0 NormalX=0 NormalY=0 NormalZ=1 AngleXU=0 Radius=15 StartAngle=4.1267 EndAngle=4.71239
    g7: ArcOfCircle CenterX=4.58312 CenterY=5 CenterZ=0 NormalX=0 NormalY=0 NormalZ=1 AngleXU=0 Radius=5 StartAngle=0 EndAngle=1.5708
    g8: GeomPoint [constr] X=9.58312 Y=10 Z=0
    g9: ArcOfCircle CenterX=4.58312 CenterY=-5 CenterZ=0 NormalX=0 NormalY=0 NormalZ=1 AngleXU=0 Radius=5 StartAngle=4.71239 EndAngle=6.28319
    g10: GeomPoint [constr] X=9.58312 Y=-10 Z=0
  constraints (26):
    c: Horizontal(g0)
    c: Horizontal(g2)
    c: Vertical(g1)
    c: Coincident(g3,g-1)
    c: Diameter(g4) = 30
    c: PointOnObject(g4,g-1)
    c: DistanceX(g4,g3) = 81.5
    c: Tangent(g4,g5) = 1.5708
    c: Tangent(g0,g5) = 1.5708
    c: Tangent(g2,g6) = 1.5708
    c: Tangent(g4,g6) = 1.5708
    c: Radius(g5) = 15
    c: Radius(g6) = 15
    c: DistanceX(g0,g10) = 74.5
    c: DistanceY(g10,g8) = 20
    c: Distance(g2,g8) = 74.5
    c: PointOnObject(g8,g2)
    c: PointOnObject(g8,g1)
    c: Tangent(g2,g7) = -1.5708
    c: Tangent(g1,g7) = -1.5708
    c: PointOnObject(g10,g1)
    c: PointOnObject(g10,g0)
    c: Tangent(g1,g9) = -1.5708
    c: Tangent(g0,g9) = -1.5708
    c: Diameter(g7) = 10
    c: Diameter(g9) = 10
FEATURE [PartDesign::Pad] Pad
  Direction = (0,0,1)
  Length = 8
  Length2 = 10
  Profile = -> Sketch
  ReferenceAxis = -> Sketch [N_Axis]
  Refine = true
  Suppressed = false
  Type = 0
FEATURE [PartDesign::Thickness] Thickness
  Base = -> Pad [Face10]
  BaseFeature = -> Pad
  Intersection = false
  Join = 0
  Mode = 0
  Refine = true
  Reversed = true
  SupportTransform = false
  Suppressed = false
  Value = 1.4
FEATURE [Sketcher::SketchObject] Sketch001
  ArcFitTolerance = 1e-06
  AttachmentSupport = -> [Thickness]
  FullyConstrained = true
  MakeInternals = false
  MapMode = 5
  Placement = pos=(0,0,1.4) rot=(0,0,1;0rad)
  sketch-geometry (1):
    g0: Circle CenterX=0 CenterY=0 CenterZ=0 NormalX=0 NormalY=0 NormalZ=1 AngleXU=0 Radius=8
  constraints (3):
    c: Diameter(g0) = 16
    c: PointOnObject(g0,g-1)
    c: DistanceX(g-1,g0) = 0
FEATURE [PartDesign::Pocket] Pocket
  BaseFeature = -> Thickness
  Direction = (0,0,-1)
  Length = 5
  Length2 = 5
  Profile = -> Sketch001
  ReferenceAxis = -> Sketch001 [N_Axis]
  Refine = true
  Suppressed = false
  Type = 0
FEATURE [PartDesign::Fillet] Fillet001
  Base = -> Pocket [Edge38]
  BaseFeature = -> Pocket
  Radius = 0.5
  Refine = true
  SupportTransform = false
  Suppressed = false
  UseAllEdges = false
FEATURE [PartDesign::Body] Body
  AllowCompound = false
  Group = -> [Sketch,Pad,Thickness,Sketch001,Pocket,Fillet001]
  Origin = -> Origin
  Tip = -> Fillet001
---- part testube.FCStd = doc fcstd_2d823b3dfcec ----
FCSTD DOCUMENT  (FreeCAD 1.0R38641 +678 (Git))
Label: testube
License: All rights reserved
LicenseURL: https://en.wikipedia.org/wiki/All_rights_reserved
objects: Sketcher::SketchObject×1, PartDesign::Revolution×1, PartDesign::Body×1
note: 6 computed .brp shape members not serialized (recipe doc carries the construction recipe); baked Part::Feature solids carry a one-line shape summary decoded from their .brp

FEATURE [Sketcher::SketchObject] Sketch
  ArcFitTolerance = 1e-06
  AttachmentSupport = -> [XZ_Plane]
  FullyConstrained = true
  MakeInternals = false
  MapMode = 5
  Placement = pos=(0,0,0) rot=(1,0,0;1.5708rad)
  sketch-geometry (13):
    g0: LineSegment StartX=8.5 StartY=94 StartZ=0 EndX=9.5 EndY=94 EndZ=0
    g1: LineSegment StartX=9.5 StartY=94 StartZ=0 EndX=9.5 EndY=95 EndZ=0
    g2: LineSegment StartX=9.5 StartY=95 StartZ=0 EndX=8.5 EndY=95 EndZ=0
    g3: LineSegment StartX=8.5 StartY=95 StartZ=0 EndX=8.5 EndY=100 EndZ=0
    g4: LineSegment StartX=8.5 StartY=100 StartZ=0 EndX=7.5 EndY=100 EndZ=0
    g5: LineSegment StartX=7.5 StartY=100 StartZ=0 EndX=7.5 EndY=13.5557 EndZ=0
    g6: LineSegment StartX=7.5 StartY=13.5557 StartZ=0 EndX=9e-16 EndY=4.61757 EndZ=0
    g7: LineSegment StartX=1.53209 StartY=4.88772 StartZ=0 EndX=7.5 EndY=12 EndZ=0
    g8: LineSegment StartX=7.5 StartY=12 StartZ=0 EndX=7.5 EndY=0 EndZ=0
    g9: LineSegment StartX=7.5 StartY=0 StartZ=0 EndX=8.5 EndY=0 EndZ=0
    g10: LineSegment StartX=8.5 StartY=0 StartZ=0 EndX=8.5 EndY=94 EndZ=0
    g11: ArcOfCircle CenterX=0 CenterY=6.1733 CenterZ=0 NormalX=0 NormalY=0 NormalZ=1 AngleXU=0 Radius=2 StartAngle=4.71239 EndAngle=5.58505
    g12: LineSegment StartX=-4e-16 StartY=4.1733 StartZ=0 EndX=9e-16 EndY=4.61757 EndZ=0
  constraints (39):
    c: Horizontal(g0)
    c: Coincident(g0,g1)
    c: Coincident(g1,g2)
    c: Coincident(g2,g3)
    c: Vertical(g3)
    c: Coincident(g3,g4)
    c: Coincident(g4,g5)
    c: Vertical(g5)
    c: Coincident(g5,g6)
    c: Coincident(g7,g8)
    c: Coincident(g8,g9)
    c: Horizontal(g9)
    c: Coincident(g9,g10)
    c: Coincident(g10,g0)
    c: Vertical(g10)
    c: Horizontal(g4)
    c: Vertical(g2,g0)
    c: Vertical(g1)
    c: Horizontal(g2)
    c: PointOnObject(g9,g-1)
    c: Vertical(g8)
    c: Vertical(g7,g5)
    c: Parallel(g6,g7)
    c: PointOnObject(g11,g-2)
    c: Tangent(g11,g7) = -1.5708
    c: PointOnObject(g6,g-2)
    c: Distance(g9,g9) = 1
    c: Distance(g6,g7) = 1
    c: Radius(g11) = 2
    c: Distance(g1,g1) = 1
    c: Distance(g3,g3) = 5
    c: DistanceY(g9,g3) = 100
    c: Coincident(g12,g6)
    c: Distance(g0,g0) = 1
    c: Distance(g3,g-2) = 8.5
    c: PointOnObject(g12,g-2)
    c: Coincident(g12,g11)
    c: DistanceY(g8,g8) = 12
    c: Angle(g-1,g7) = 0.872665
FEATURE [PartDesign::Revolution] Revolution
  Angle = 360
  Angle2 = 60
  Axis = (0,2e-16,1)
  Base = (0,0,0)
  Placement = pos=(0,0,0) rot=(1,0,0;1.5708rad)
  Profile = -> Sketch
  ReferenceAxis = -> Sketch [V_Axis]
  Refine = true
  Reversed = true
  Suppressed = false
  Type = 0
FEATURE [PartDesign::Body] Body  label="testube"
  AllowCompound = false
  Group = -> [Sketch,Revolution]
  Origin = -> Origin
  Tip = -> Revolution
